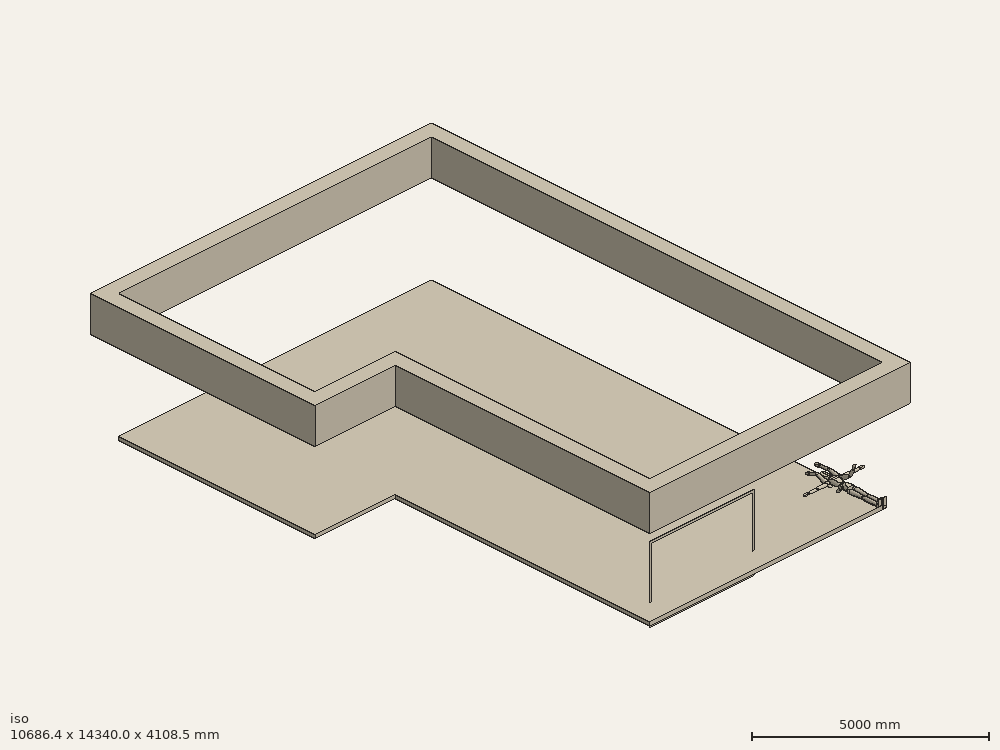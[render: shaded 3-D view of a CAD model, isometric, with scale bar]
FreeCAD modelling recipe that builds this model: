
FCSTD DOCUMENT  (FreeCAD 1.0R39109 (Git))
Label: 69
License: All rights reserved
LicenseURL: http://en.wikipedia.org/wiki/All_rights_reserved
objects: Sketcher::SketchObject×156, PartDesign::CoordinateSystem×87, PartDesign::Fillet×81, PartDesign::Groove×78, PartDesign::Revolution×75, PartDesign::Body×45, PartDesign::Pocket×27, Part::FeaturePython×6, PartDesign::Pad×6, App::Part×3, App::FeaturePython×2, Part::Part2DObjectPython×2, TechDraw::DrawSVGTemplate×1, TechDraw::DrawViewImage×1, TechDraw::DrawViewArch×1, TechDraw::DrawPage×1, App::Link×1, Assembly::JointGroup×1, Assembly::AssemblyObject×1
note: 1254 computed .brp shape members not serialized (recipe doc carries the construction recipe); baked Part::Feature solids carry a one-line shape summary decoded from their .brp
EXTERNAL_REF file=shed_shelves.FCStd obj=Assembly

FEATURE [Sketcher::SketchObject] Sketch
  ArcFitTolerance = 0
  FullyConstrained = true
  MakeInternals = false
  sketch-geometry (6):
    g0: LineSegment StartX=-9360 StartY=7620 StartZ=0 EndX=-9360 EndY=13500 EndZ=0
    g1: LineSegment StartX=-9360 StartY=13500 StartZ=0 EndX=0 EndY=13500 EndZ=0
    g2: LineSegment StartX=0 StartY=13500 StartZ=0 EndX=0 EndY=0 EndZ=0
    g3: LineSegment StartX=0 StartY=0 StartZ=0 EndX=-6960 EndY=0 EndZ=0
    g4: LineSegment StartX=-6960 StartY=0 StartZ=0 EndX=-6960 EndY=7620 EndZ=0
    g5: LineSegment StartX=-6960 StartY=7620 StartZ=0 EndX=-9360 EndY=7620 EndZ=0
  constraints (17):
    c: Vertical(g0)
    c: Horizontal(g1)
    c: Coincident(g1,g2)
    c: Vertical(g2)
    c: Coincident(g2,g3)
    c: Horizontal(g3)
    c: Coincident(g3,g4)
    c: Vertical(g4)
    c: Coincident(g4,g5)
    c: Horizontal(g5)
    c: Coincident(g5,g0)
    c: Coincident(g0,g1)
    c: DistanceX(g3,g3) = 6960
    c: Coincident(g2,g-1)
    c: DistanceY(g0,g0) = 5880
    c: DistanceX(g5,g5) = 2400
    c: DistanceY(g2,g2) = 13500
FEATURE [Part::FeaturePython] Wall001  label="Wall_Outer"  # Arch/BIM 166 (typed FeaturePython)
  Align = 1
  ArchSketchData = true
  Area = 114300000
  Base = -> Sketch
  BlockHeight = 0
  BlockLength = 0
  CountBroken = 0
  CountEntire = 0
  Face = 0
  Height = 2500
  HorizontalArea = 19908000
  IfcType = 166
  Joint = 0
  Length = 45720
  MakeBlocks = false
  MoveBase = false
  MoveWithHost = false
  Normal = (0,0,0)
  OffsetFirst = 0
  OffsetSecond = 0
  PerimeterLength = 94800
  PredefinedType = 0
  VerticalArea = 237000000
  Width = 420
FEATURE [Sketcher::SketchObject] Sketch001
  ArcFitTolerance = 0
  ExternalGeometry = -> [Sketch]
  FullyConstrained = true
  MakeInternals = false
  expr: Constraints[42] = .Constraints.a + 10 cm
  sketch-geometry (16):
    g0: LineSegment StartX=-2960 StartY=11375 StartZ=0 EndX=-2960 EndY=7865 EndZ=0
    g1: LineSegment StartX=-2960 StartY=7865 StartZ=0 EndX=0 EndY=7865 EndZ=0
    g2: LineSegment StartX=-2960 StartY=10365 StartZ=0 EndX=0 EndY=10365 EndZ=0
    g3: LineSegment StartX=-2960 StartY=0 StartZ=0 EndX=-2960 EndY=3630 EndZ=0
    g4: LineSegment StartX=-2960 StartY=3630 StartZ=0 EndX=0 EndY=3630 EndZ=0
    g5: LineSegment StartX=-4540 StartY=13500 StartZ=0 EndX=-4540 EndY=11100 EndZ=0
    g6: LineSegment StartX=-4540 StartY=11100 StartZ=0 EndX=-7060 EndY=11100 EndZ=0
    g7: LineSegment StartX=-7060 StartY=11100 StartZ=0 EndX=-7060 EndY=7620 EndZ=0
    g8: LineSegment StartX=-4540 StartY=9765 StartZ=0 EndX=-7060 EndY=9765 EndZ=0
    g9: LineSegment StartX=-2960 StartY=11375 StartZ=0 EndX=-2355 EndY=11375 EndZ=0
    g10: LineSegment StartX=-2355 StartY=11375 StartZ=0 EndX=-2355 EndY=13500 EndZ=0
    g11: LineSegment StartX=-2355 StartY=12705 StartZ=0 EndX=-3060 EndY=12705 EndZ=0
    g12: LineSegment StartX=-4540 StartY=9765 StartZ=0 EndX=-4540 EndY=9000 EndZ=0
    g13: LineSegment StartX=-2200 StartY=7865 StartZ=0 EndX=-2200 EndY=8525 EndZ=0
    g14: LineSegment StartX=-1070 StartY=7865 StartZ=0 EndX=-1070 EndY=8375 EndZ=0
    g15: LineSegment StartX=0 StartY=9145 StartZ=0 EndX=-510 EndY=9145 EndZ=0
  constraints (60):
    c: Vertical(g0)
    c: Coincident(g1,g0)
    c: PointOnObject(g1,g-4)
    c: Horizontal(g1)
    c: PointOnObject(g2,g0)
    c: Horizontal(g2)
    c: PointOnObject(g2,g-4)
    c: PointOnObject(g3,g-3)
    c: Vertical(g3)
    c: Coincident(g4,g3)
    c: PointOnObject(g4,g-4)
    c: Horizontal(g4)
    c: Vertical(g3,g0)
    c: PointOnObject(g5,g-8)
    c: Vertical(g5)
    c: Coincident(g6,g5)
    c: Horizontal(g6)
    c: Coincident(g7,g6)
    c: Vertical(g7)
    c: PointOnObject(g7,g-6)
    c: Horizontal(g8)
    c: PointOnObject(g8,g7)
    c: Vertical(g8,g5)
    c: Horizontal(g9)
    c: Coincident(g0,g9)
    c: Coincident(g9,g10)
    c: PointOnObject(g10,g-8)
    c: Vertical(g10)
    c: PointOnObject(g11,g10)
    c: Horizontal(g11)
    c: DistanceX(g3,g-4) = 2960
    c: DistanceX(g-5,g3) = 4000
    c: DistanceY(g3,g3) = 3630
    c: Coincident(g12,g8)
    c: Vertical(g12)
    c: DistanceX(g8,g8) = 2520
    c: DistanceY(g12,g12) = 765
    c: DistanceY(g8,g5) = 1335
    c: DistanceX(g12,g2) = 1580
    c: DistanceX(g-6,g7) = -100
    c: DistanceX(g9,g9) = 605  'a'
    c: DistanceY(g0,g11) = 1330
    c: DistanceX(g11,g11) = 705
    c: DistanceY(g11,g10) = 795
    c: DistanceY(g5,g5) = 2400
    c: DistanceY(g2,g0) = 1010
    c: PointOnObject(g13,g1)
    c: Vertical(g13)
    c: PointOnObject(g14,g1)
    c: Vertical(g14)
    c: PointOnObject(g15,g-4)
    c: Horizontal(g15)
    c: DistanceX(g15,g15) = 510
    c: DistanceY(g14,g14) = 510
    c: DistanceY(g13,g13) = 660
    c: DistanceX(g0,g13) = 760
    c: DistanceX(g14,g15) = 1070
    c: DistanceY(g1,g15) = 1280
    c: DistanceY(g0,g2) = 2500
    c: DistanceY(g3,g0) = 4235
FEATURE [Part::FeaturePython] Wall002  label="Wall_Inner"  # Arch/BIM 166 (typed FeaturePython)
  Align = 1
  ArchSketchData = true
  Area = 82050000
  Base = -> Sketch001
  BlockHeight = 0
  BlockLength = 0
  CountBroken = 0
  CountEntire = 0
  Face = 0
  Height = 2500
  HorizontalArea = 0
  IfcType = 166
  Joint = 0
  Length = 32820
  MakeBlocks = false
  MoveBase = false
  MoveWithHost = false
  Normal = (0,0,0)
  OffsetFirst = 0
  OffsetSecond = 0
  PerimeterLength = 0
  PredefinedType = 0
  VerticalArea = 0
  Width = 100
FEATURE [Sketcher::SketchObject] Sketch004
  ArcFitTolerance = 0
  ExternalGeometry = -> [Wall001]
  FullyConstrained = false
  MakeInternals = false
  MapMode = 5
  Placement = pos=(0,567.773,0) rot=(1,0,0;1.5708rad)
  sketch-geometry (10):
    g0: LineSegment StartX=-42527.4 StartY=2392.27 StartZ=0 EndX=-39377.4 EndY=2392.27 EndZ=0
    g1: LineSegment StartX=-39377.4 StartY=2392.27 StartZ=0 EndX=-39377.4 EndY=0 EndZ=0
    g2: LineSegment StartX=-39377.4 StartY=0 StartZ=0 EndX=-42527.4 EndY=0 EndZ=0
    g3: LineSegment StartX=-42527.4 StartY=0 StartZ=0 EndX=-42527.4 EndY=2392.27 EndZ=0
    g4: LineSegment StartX=-42457.4 StartY=2322.27 StartZ=0 EndX=-39447.4 EndY=2322.27 EndZ=0
    g5: LineSegment StartX=-39447.4 StartY=2322.27 StartZ=0 EndX=-39447.4 EndY=70 EndZ=0
    g6: LineSegment StartX=-39447.4 StartY=70 StartZ=0 EndX=-42457.4 EndY=70 EndZ=0
    g7: LineSegment StartX=-42457.4 StartY=70 StartZ=0 EndX=-42457.4 EndY=2322.27 EndZ=0
    g8: GeomPoint [constr] X=-40952.4 Y=1196.13 Z=0
    g9: GeomPoint [constr] X=-40952.4 Y=1196.13 Z=0
  constraints (22):
    c: Coincident(g0,g1)
    c: Coincident(g1,g2)
    c: Coincident(g2,g3)
    c: Coincident(g3,g0)
    c: Horizontal(g0)
    c: Horizontal(g2)
    c: Vertical(g1)
    c: Vertical(g3)
    c: Coincident(g4,g5)
    c: Coincident(g5,g6)
    c: Coincident(g6,g7)
    c: Coincident(g7,g4)
    c: Horizontal(g4)
    c: Horizontal(g6)
    c: Vertical(g5)
    c: Vertical(g7)
    c: DistanceX(g4,g0) = 70
    c: DistanceY(g4,g0) = 70
    c: Symmetric(g2,g0,g9)
    c: Symmetric(g6,g4,g8)
    c: Coincident(g8,g9)
    c: DistanceX(g2,g2) = 3150
FEATURE [Sketcher::SketchObject] Sketch002
  ArcFitTolerance = 0
  ExternalGeometry = -> [Wall001]
  FullyConstrained = false
  MakeInternals = false
  MapMode = 5
  Placement = pos=(0,567.773,0) rot=(1,0,0;1.5708rad)
  sketch-geometry (22):
    g0: LineSegment StartX=-6400 StartY=-608.511 StartZ=0 EndX=-3250 EndY=-608.511 EndZ=0
    g1: LineSegment StartX=-3250 StartY=-608.511 StartZ=0 EndX=-3250 EndY=1501.64 EndZ=0
    g2: LineSegment StartX=-3250 StartY=1501.64 StartZ=0 EndX=-6400 EndY=1501.64 EndZ=0
    g3: LineSegment StartX=-6400 StartY=1501.64 StartZ=0 EndX=-6400 EndY=-608.511 EndZ=0
    g4: LineSegment StartX=-6330 StartY=1431.64 StartZ=0 EndX=-3320 EndY=1431.64 EndZ=0
    g5: LineSegment StartX=-3320 StartY=1431.64 StartZ=0 EndX=-3320 EndY=-538.511 EndZ=0
    g6: LineSegment StartX=-3320 StartY=-538.511 StartZ=0 EndX=-6330 EndY=-538.511 EndZ=0
    g7: LineSegment StartX=-6330 StartY=-538.511 StartZ=0 EndX=-6330 EndY=1431.64 EndZ=0
    g8: GeomPoint [constr] X=-4825 Y=446.564 Z=0
    g9: GeomPoint [constr] X=-4825 Y=446.564 Z=0
    g10: LineSegment StartX=-5469.54 StartY=1431.64 StartZ=0 EndX=-5329.54 EndY=1431.64 EndZ=0
    g11: LineSegment StartX=-5329.54 StartY=1431.64 StartZ=0 EndX=-5329.54 EndY=-538.511 EndZ=0
    g12: LineSegment StartX=-5329.54 StartY=-538.511 StartZ=0 EndX=-5469.54 EndY=-538.511 EndZ=0
    g13: LineSegment StartX=-5469.54 StartY=-538.511 StartZ=0 EndX=-5469.54 EndY=1431.64 EndZ=0
    g14: LineSegment StartX=-4500.16 StartY=1431.64 StartZ=0 EndX=-4360.16 EndY=1431.64 EndZ=0
    g15: LineSegment StartX=-4360.16 StartY=1431.64 StartZ=0 EndX=-4360.16 EndY=-538.511 EndZ=0
    g16: LineSegment StartX=-4360.16 StartY=-538.511 StartZ=0 EndX=-4500.16 EndY=-538.511 EndZ=0
    g17: LineSegment StartX=-4500.16 StartY=-538.511 StartZ=0 EndX=-4500.16 EndY=1431.64 EndZ=0
    g18: LineSegment StartX=-5469.54 StartY=394.079 StartZ=0 EndX=-6330 EndY=394.079 EndZ=0
    g19: LineSegment StartX=-6330 StartY=394.079 StartZ=0 EndX=-6330 EndY=534.079 EndZ=0
    g20: LineSegment StartX=-6330 StartY=534.079 StartZ=0 EndX=-5469.54 EndY=534.079 EndZ=0
    g21: LineSegment StartX=-5469.54 StartY=534.079 StartZ=0 EndX=-5469.54 EndY=394.079 EndZ=0
  constraints (59):
    c: Coincident(g0,g1)
    c: Coincident(g1,g2)
    c: Coincident(g2,g3)
    c: Coincident(g3,g0)
    c: Horizontal(g0)
    c: Horizontal(g2)
    c: Vertical(g1)
    c: Vertical(g3)
    c: Coincident(g4,g5)
    c: Coincident(g5,g6)
    c: Coincident(g6,g7)
    c: Coincident(g7,g4)
    c: Horizontal(g4)
    c: Horizontal(g6)
    c: Vertical(g5)
    c: Vertical(g7)
    c: Symmetric(g6,g4,g8)
    c: Symmetric(g1,g0,g9)
    c: Coincident(g9,g8)
    c: DistanceX(g4,g1) = 70
    c: DistanceY(g4,g1) = 70
    c: Coincident(g10,g11)
    c: Coincident(g11,g12)
    c: Coincident(g12,g13)
    c: Coincident(g13,g10)
    c: Horizontal(g10)
    c: Horizontal(g12)
    c: Vertical(g11)
    c: Vertical(g13)
    c: PointOnObject(g10,g4)
    c: PointOnObject(g11,g6)
    c: Coincident(g14,g15)
    c: Coincident(g15,g16)
    c: Coincident(g16,g17)
    c: Coincident(g17,g14)
    c: Horizontal(g14)
    c: Horizontal(g16)
    c: Vertical(g15)
    c: Vertical(g17)
    c: PointOnObject(g14,g4)
    c: PointOnObject(g15,g6)
    c: Coincident(g18,g19)
    c: Coincident(g19,g20)
    c: Coincident(g20,g21)
    c: Coincident(g21,g18)
    c: Horizontal(g18)
    c: Horizontal(g20)
    c: Vertical(g19)
    c: Vertical(g21)
    c: PointOnObject(g18,g13)
    c: PointOnObject(g19,g7)
    c: DistanceX(g12,g11) = 140
    c: DistanceX(g16,g15) = 140
    c: DistanceY(g18,g20) = 140
    c: DistanceX(g0,g0) = 3150
    c: DistanceX(g20,g20) = 860.46
    c: DistanceY(g0,g18) = 1002.59
    c: DistanceY(g3,g3) = 2110.15
    c: DistanceX(g15,g5) = 1040.16
FEATURE [Part::FeaturePython] Window  # Arch/BIM 170 (typed FeaturePython)
  Area = 0
  Base = -> Sketch002
  Frame = 0
  Height = 0
  HoleDepth = 0
  HoleWire = 0
  HorizontalArea = 0
  IfcData = attributes={"OverallHeight": {"value": 0.0}, "OverallWidth": {"value": 0.0}}
  IfcType = 170
  LouvreSpacing = 0
  LouvreWidth = 0
  MoveBase = false
  MoveWithHost = true
  Normal = (0,1,-2e-16)
  Opening = 0
  OverallHeight = 0
  OverallWidth = 0
  PartitioningType = 0
  PerimeterLength = 0
  PredefinedType = 0
  Preset = 0
  SymbolElevation = false
  SymbolPlan = false
  VerticalArea = 0
  Width = 0
  WindowParts = Default | Frame | Wire0,Wire1,Wire2,Wire3,Wire4 | 1 | 0
  expr: OverallHeight = .Height.Value
  expr: OverallWidth = .Width.Value
FEATURE [Part::FeaturePython] Structure  # Arch/BIM 172 (typed FeaturePython)
  Base = -> Sketch
  BaseMirror = false
  BaseOffsetX = 0
  BaseOffsetY = 0
  BasePerpendicularToTool = false
  BaseRotation = 0
  ComputedLength = 100
  FaceMaker = 0
  Height = 100
  HorizontalArea = 108072000
  IfcType = 172
  Length = 0
  MoveBase = false
  MoveWithHost = false
  Nodes = (2) [(-4091.11,7247.51,0),(-4091.11,7247.51,-100)]
  NodesOffset = 0
  Normal = (0,0,0)
  PerimeterLength = 45720
  PredefinedType = 0
  ToolOffsetFirst = 0
  ToolOffsetLast = 0
  VerticalArea = 4572000
  Width = 1000
FEATURE [Part::FeaturePython] Wall  label="Wall_Roof"  # Arch/BIM 166 (typed FeaturePython)
  Align = 1
  ArchSketchData = true
  Area = 45720000
  Base = -> Sketch
  BlockHeight = 0
  BlockLength = 0
  CountBroken = 0
  CountEntire = 0
  Face = 0
  Height = 1000
  HorizontalArea = 19908000
  IfcType = 166
  Joint = 0
  Length = 45720
  MakeBlocks = false
  MoveBase = false
  MoveWithHost = false
  Normal = (0,0,0)
  OffsetFirst = 0
  OffsetSecond = 0
  PerimeterLength = 94800
  Placement = pos=(0,0,2500) rot=(0,0,1;0rad)
  PredefinedType = 0
  VerticalArea = 94800000
  Width = 420
FEATURE [TechDraw::DrawSVGTemplate] Template
  Height = 304.8
  Orientation = 1
  Template = <path>
  Width = 457.2
FEATURE [TechDraw::DrawViewImage] ActiveView
  Height = 102.4
  ImageFile = <userpath>/.cache/FreeCAD/Cache/FreeCAD_Doc_a79d04ec-db21-4fb2-806d-f2524595e8da_78bda8_607707/PageActiveViewpjV7xk.png
  LockPosition = false
  Rotation = 0
  Scale = 0.5
  ScaleType = 2
  Width = 128
  X = 369.736
  Y = 89.5228
FEATURE [Sketcher::SketchObject] Sketch005
  ArcFitTolerance = 1e-06
  ExternalGeometry = -> [Wall]
  FullyConstrained = true
  MakeInternals = false
  sketch-geometry (3):
    g0: LineSegment StartX=-8800 StartY=13920 StartZ=0 EndX=-8800 EndY=16770 EndZ=0
    g1: LineSegment StartX=-8800 StartY=16770 StartZ=0 EndX=-7510 EndY=16770 EndZ=0
    g2: LineSegment StartX=-7510 StartY=16770 StartZ=0 EndX=-7510 EndY=13920 EndZ=0
  constraints (10):
    c: Distance(g0) = 2850
    c: Vertical(g0)
    c: Distance(g1) = 1290
    c: Horizontal(g1)
    c: Coincident(g1,g0)
    c: Coincident(g2,g1)
    c: Vertical(g2)
    c: Horizontal(g2,g0)
    c: Horizontal(g0,g-3)
    c: Distance(g0,g-3) = 980
FEATURE [Part::FeaturePython] Wall003  label="Wall_Shed"  # Arch/BIM 166 (typed FeaturePython)
  Align = 1
  ArchSketchData = true
  Area = 16146900
  Base = -> Sketch005
  BlockHeight = 0
  BlockLength = 0
  CountBroken = 0
  CountEntire = 0
  Face = 0
  Height = 2310
  HorizontalArea = 1.478e+06
  IfcData = attributes={"GlobalId": {"name": "GlobalId", "type": "IfcGloballyUniqueId", "is_enum": false, "enum_values": []}, "Description": {"... (+533 chars omitted),+1 more (map truncated)
  IfcType = 166
  Joint = 0
  Length = 6990
  MakeBlocks = false
  MoveBase = false
  MoveWithHost = false
  Normal = (0,0,0)
  OffsetFirst = 0
  OffsetSecond = 0
  PerimeterLength = 15180
  PredefinedType = 0
  VerticalArea = 35065800
  Width = 200
FEATURE [App::FeaturePython] Section  # WARN: FeaturePython — macro-defined, semantics opaque (R4)
  Clip = false
  Depth = 0
  Objects = -> [Wall001,Wall002,Wall003]
  OnlySolids = true
  Placement = pos=(-4687.81,6742.19,1250) rot=(0.759144,0.1826,0.624786;0rad)
  UseMaterialColorForFill = false
FEATURE [Part::Part2DObjectPython] Shape2DView  # Draft 2D object (typed FeaturePython)
  AutoUpdate = true
  Base = -> Section
  Clip = false
  FuseArch = false
  HiddenLines = false
  InPlace = true
  OnlySolids = false
  Projection = (0.361718,-0.400925,0.841677)
  ProjectionMode = 0
  SegmentLength = 0.05
  Tessellation = false
  VisibleOnly = false
FEATURE [Part::Part2DObjectPython] Shape2DView001  # Draft 2D object (typed FeaturePython)
  AutoUpdate = true
  Base = -> Section
  Clip = false
  FuseArch = false
  HiddenLines = false
  InPlace = true
  OnlySolids = false
  Placement = pos=(0,0,3051.7) rot=(0,0,1;0rad)
  Projection = (0.361718,-0.400925,0.841677)
  ProjectionMode = 0
  SegmentLength = 0.05
  Tessellation = false
  VisibleOnly = false
FEATURE [TechDraw::DrawViewArch] ArchView  label="TopViewStue"
  AllOn = false
  Caption = TopViewStue
  CutLineWidth = 0.5
  FillSpaces = true
  FontSize = 12
  JoinArch = false
  LineSpacing = 1
  LineWidth = 0.25
  LockPosition = false
  RenderMode = 2
  Rotation = 0
  Scale = 0.01
  ScaleType = 2
  ShowFill = false
  ShowHidden = false
  Source = -> Section
  Symbol = <blob: 39801 chars omitted>
  X = 81.0502
  Y = 207.25
  expr: Caption = Label
FEATURE [TechDraw::DrawPage] Page
  KeepUpdated = true
  NextBalloonIndex = 1
  ProjectionType = 0
  Scale = 0.01
  Template = -> Template
  Views = -> [ArchView,ActiveView]
FEATURE [Sketcher::SketchObject] Sketch006
  ArcFitTolerance = 0
  FullyConstrained = true
  MakeInternals = false
  MapMode = 5
  sketch-geometry (12):
    g0: LineSegment StartX=0 StartY=0 StartZ=0 EndX=90 EndY=0 EndZ=0
    g1: LineSegment StartX=90 StartY=0 StartZ=0 EndX=90 EndY=215 EndZ=0
    g2: LineSegment StartX=90 StartY=215 StartZ=0 EndX=0 EndY=215 EndZ=0
    g3: LineSegment StartX=0 StartY=215 StartZ=0 EndX=0 EndY=0 EndZ=0
    g4: LineSegment StartX=3.5 StartY=0 StartZ=0 EndX=86.5 EndY=0 EndZ=0
    g5: LineSegment StartX=86.5 StartY=0 StartZ=0 EndX=86.5 EndY=211.5 EndZ=0
    g6: LineSegment StartX=86.5 StartY=211.5 StartZ=0 EndX=3.5 EndY=211.5 EndZ=0
    g7: LineSegment StartX=3.5 StartY=211.5 StartZ=0 EndX=3.5 EndY=0 EndZ=0
    g8: LineSegment StartX=-2 StartY=0 StartZ=0 EndX=92 EndY=0 EndZ=0
    g9: LineSegment StartX=92 StartY=0 StartZ=0 EndX=92 EndY=217 EndZ=0
    g10: LineSegment StartX=92 StartY=217 StartZ=0 EndX=-2 EndY=217 EndZ=0
    g11: LineSegment StartX=-2 StartY=217 StartZ=0 EndX=-2 EndY=0 EndZ=0
  constraints (36):
    c: Coincident(g0,g1)
    c: Coincident(g1,g2)
    c: Coincident(g2,g3)
    c: Coincident(g3,g0)
    c: Horizontal(g0)
    c: Horizontal(g2)
    c: Vertical(g1)
    c: Vertical(g3)
    c: DistanceX(g0) = 0
    c: DistanceY(g0) = 0
    c: DistanceX(g0) = 90
    c: DistanceY(g1) = 215
    c: Coincident(g4,g5)
    c: Coincident(g5,g6)
    c: Coincident(g6,g7)
    c: Coincident(g7,g4)
    c: Horizontal(g4)
    c: Horizontal(g6)
    c: Vertical(g5)
    c: Vertical(g7)
    c: DistanceY(g6,g2) = 3.5
    c: DistanceX(g6,g2) = -3.5
    c: DistanceX(g5,g1) = 3.5
    c: DistanceY(g4,g0) = 0
    c: Coincident(g8,g9)
    c: Coincident(g9,g10)
    c: Coincident(g10,g11)
    c: Coincident(g11,g8)
    c: Horizontal(g8)
    c: Horizontal(g10)
    c: Vertical(g9)
    c: Vertical(g11)
    c: DistanceX(g2,g10) = -2
    c: DistanceX(g1,g9) = 2
    c: DistanceY(g2,g10) = 2
    c: DistanceY(g8,g0) = 0
FEATURE [PartDesign::CoordinateSystem] LCS_0
  AttacherType = Attacher::AttachEngine3D
  AttachmentSupport = -> [X_Axis020]
  MapMode = 2
FEATURE [Sketcher::SketchObject] Sketch061
  ArcFitTolerance = 0
  AttachmentSupport = -> [XY_Plane021]
  FullyConstrained = true
  MakeInternals = false
  MapMode = 5
  sketch-geometry (14):
    g0: LineSegment StartX=0 StartY=0 StartZ=0 EndX=0 EndY=296.299 EndZ=0
    g1-g7: Circle [constr] x7 (B-spline internal-alignment scaffolding for g8; pole/knot coordinates omitted)
    g8: BSplineCurve PolesCount=7 KnotsCount=5 Degree=3 IsPeriodic=0
    g9-g13: GeomPoint [constr] x5 (B-spline internal-alignment scaffolding for g8; pole/knot coordinates omitted)
  constraints (12):
    c: Coincident(g0,g-1)
    c: Vertical(g0)
    c: Weight(g1) = 1
    c: Coincident(g8,g0)
    c: Equal(g1, g2-g7) x6
    c: Coincident(g8,g0)
    c: InternalAlignment(g1-g7 -> g8) x7
    c: InternalAlignment(g9-g13 -> g8) x5
    c: Horizontal(g0,g2)
    c: Horizontal(g0,g6)
    c: Block(g0)
    c: Block(g8)
FEATURE [PartDesign::Revolution] Revolution033
  Angle = 360
  Angle2 = 60
  Axis = (0,1,0)
  Base = (0,0,0)
  Profile = -> Sketch061
  ReferenceAxis = -> Sketch061 [V_Axis]
  Reversed = true
  Suppressed = false
  Type = 0
FEATURE [PartDesign::CoordinateSystem] Local_CS033  label="Head/Neck LCS"
  AttacherType = Attacher::AttachEngine3D
  AttachmentSupport = -> [Revolution033]
  MapMode = 2
FEATURE [Sketcher::SketchObject] Sketch062
  ArcFitTolerance = 0
  AttachmentSupport = -> [XY_Plane022]
  FullyConstrained = true
  MakeInternals = false
  MapMode = 5
  sketch-geometry (18):
    g0: LineSegment StartX=0 StartY=322.019 StartZ=0 EndX=0 EndY=20.3719 EndZ=0
    g1-g9: Circle [constr] x9 (B-spline internal-alignment scaffolding for g10; pole/knot coordinates omitted)
    g10: BSplineCurve PolesCount=9 KnotsCount=7 Degree=3 IsPeriodic=0
    g11-g17: GeomPoint [constr] x7 (B-spline internal-alignment scaffolding for g10; pole/knot coordinates omitted)
  constraints (12):
    c: Vertical(g0)
    c: PointOnObject(g0,g-2)
    c: Weight(g1) = 1
    c: Coincident(g10,g0)
    c: Equal(g1, g2-g9) x8
    c: Coincident(g10,g0)
    c: InternalAlignment(g1-g9 -> g10) x9
    c: InternalAlignment(g11-g17 -> g10) x7
    c: Horizontal(g0,g2)
    c: Horizontal(g0,g8)
    c: Block(g0)
    c: Block(g10)
FEATURE [PartDesign::Revolution] Revolution034  label="Base shape"
  Angle = 360
  Angle2 = 60
  Axis = (0,1,0)
  Base = (0,0,0)
  Profile = -> Sketch062
  ReferenceAxis = -> Sketch062 [V_Axis]
  Reversed = true
  Suppressed = false
  Type = 0
FEATURE [PartDesign::CoordinateSystem] Local_CS028  label="Chest/Neck LCS"
  AttacherType = Attacher::AttachEngine3D
  AttachmentOffset = pos=(354,0,0) rot=(0,0,1;0rad)
  AttachmentSupport = -> [Revolution034]
  MapMode = 4
  Placement = pos=(0,354,0) rot=(0.57735,0.57735,0.57735;2.0944rad)
FEATURE [PartDesign::CoordinateSystem] Local_CS029  label="Chest/Waist LCS"
  AttacherType = Attacher::AttachEngine3D
  AttachmentSupport = -> [Revolution034]
  MapMode = 2
FEATURE [PartDesign::CoordinateSystem] Local_CS030  label="Chest/Left shoulder LCS"
  AttacherType = Attacher::AttachEngine3D
  AttachmentOffset = pos=(184,257,0) rot=(0,0,1;0rad)
  AttachmentSupport = -> [Revolution034]
  MapMode = 2
  Placement = pos=(184,257,0) rot=(0,0,1;0rad)
FEATURE [PartDesign::CoordinateSystem] Local_CS031  label="Chest/Right shoulder LCS"
  AttacherType = Attacher::AttachEngine3D
  AttachmentOffset = pos=(-184,257,0) rot=(0,0,1;0rad)
  AttachmentSupport = -> [Revolution034]
  MapMode = 2
  Placement = pos=(-184,257,0) rot=(0,0,1;0rad)
FEATURE [Sketcher::SketchObject] Sketch063
  ArcFitTolerance = 0
  AttachmentSupport = -> [XY_Plane021]
  FullyConstrained = true
  MakeInternals = false
  MapMode = 5
  sketch-geometry (2):
    g0: LineSegment StartX=-1.01e-14 StartY=55 StartZ=0 EndX=-1.01e-14 EndY=-55 EndZ=0
    g1: ArcOfCircle CenterX=0 CenterY=0 CenterZ=0 NormalX=0 NormalY=0 NormalZ=1 AngleXU=0 Radius=55 StartAngle=4.71239 EndAngle=7.85398
  constraints (6):
    c: Vertical(g0)
    c: Coincident(g1,g-1)
    c: Coincident(g1,g0)
    c: Coincident(g1,g0)
    c: PointOnObject(g0,g-2)
    c: Radius(g1) = 55
FEATURE [PartDesign::Groove] Groove026
  Angle = 360
  Angle2 = 60
  Axis = (0,1,0)
  Base = (0,0,0)
  BaseFeature = -> Revolution033
  Profile = -> Sketch063
  ReferenceAxis = -> Sketch063 [V_Axis]
  Suppressed = false
  Type = 0
FEATURE [Sketcher::SketchObject] Sketch064
  ArcFitTolerance = 0
  AttachmentSupport = -> [XZ_Plane021]
  FullyConstrained = true
  MakeInternals = false
  MapMode = 5
  Placement = pos=(0,0,0) rot=(1,0,0;1.5708rad)
  sketch-geometry (5):
    g0: LineSegment StartX=-125 StartY=125 StartZ=0 EndX=125 EndY=125 EndZ=0
    g1: LineSegment StartX=125 StartY=125 StartZ=0 EndX=125 EndY=50 EndZ=0
    g2: LineSegment StartX=125 StartY=50 StartZ=0 EndX=0 EndY=75 EndZ=0
    g3: LineSegment StartX=0 StartY=75 StartZ=0 EndX=-125 EndY=50 EndZ=0
    g4: LineSegment StartX=-125 StartY=50 StartZ=0 EndX=-125 EndY=125 EndZ=0
  constraints (15):
    c: Horizontal(g0)
    c: Coincident(g0,g1)
    c: Vertical(g1)
    c: Coincident(g1,g2)
    c: Coincident(g2,g3)
    c: Coincident(g3,g4)
    c: Coincident(g4,g0)
    c: Vertical(g4)
    c: Horizontal(g3,g1)
    c: PointOnObject(g2,g-2)
    c: DistanceX(g0,g0) = 250
    c: DistanceX(g0,g-1) = 125
    c: DistanceY(g4,g4) = 75
    c: DistanceY(g-1,g2) = 75
    c: DistanceY(g-1,g0) = 125
FEATURE [PartDesign::Pocket] Pocket009
  BaseFeature = -> Groove026
  Direction = (0,1,0.05)
  Length = 300
  Length2 = 5
  Profile = -> Sketch064
  ReferenceAxis = -> Sketch064 [N_Axis]
  Suppressed = false
  Type = 0
  UseCustomVector = true
FEATURE [PartDesign::Fillet] Fillet027
  Base = -> Pocket009 [Edge3]
  BaseFeature = -> Pocket009
  Radius = 3
  SupportTransform = false
  Suppressed = false
  UseAllEdges = false
FEATURE [PartDesign::Body] Body019  label="Head"
  AllowCompound = false
  Group = -> [Sketch061,Revolution033,Sketch063,Groove026,Sketch064,Pocket009,Fillet027,Local_CS033]
  Origin = -> Origin021
  Placement = pos=(0,1552,0) rot=(0,0,1;0rad)
  Tip = -> Fillet027
FEATURE [Sketcher::SketchObject] Sketch065
  ArcFitTolerance = 0
  AttachmentSupport = -> [YZ_Plane022]
  FullyConstrained = true
  MakeInternals = false
  MapMode = 5
  Placement = pos=(0,0,0) rot=(0.57735,0.57735,0.57735;2.0944rad)
  sketch-geometry (6):
    g0: LineSegment StartX=0 StartY=76.0576 StartZ=0 EndX=164.705 EndY=107.04 EndZ=0
    g1: LineSegment StartX=230.198 StartY=103.732 StartZ=0 EndX=327.121 EndY=75.1407 EndZ=0
    g2: LineSegment StartX=327.121 StartY=75.1407 StartZ=0 EndX=327.121 EndY=181.805 EndZ=0
    g3: LineSegment StartX=327.121 StartY=181.805 StartZ=0 EndX=0 EndY=181.805 EndZ=0
    g4: LineSegment StartX=0 StartY=181.805 StartZ=0 EndX=0 EndY=76.0576 EndZ=0
    g5: ArcOfCircle CenterX=190.587 CenterY=-30.5467 CenterZ=0 NormalX=0 NormalY=0 NormalZ=1 AngleXU=0 Radius=140 StartAngle=1.28394 EndAngle=1.75673
  constraints (14):
    c: Coincident(g1,g2)
    c: Vertical(g2)
    c: Coincident(g2,g3)
    c: Horizontal(g3)
    c: Coincident(g3,g4)
    c: Coincident(g4,g0)
    c: Vertical(g4)
    c: PointOnObject(g3,g-2)
    c: Tangent(g1,g5) = 1.5708
    c: Tangent(g0,g5) = 1.5708
    c: Radius(g5) = 140
    c: Block(g0)
    c: Block(g1)
    c: Block(g3)
FEATURE [PartDesign::Pocket] Pocket010  label="Front cut"
  BaseFeature = -> Revolution034
  Direction = (-1,0,0)
  Length = 5
  Length2 = 5
  Midplane = true
  Profile = -> Sketch065
  ReferenceAxis = -> Sketch065 [N_Axis]
  Suppressed = false
  Type = 1
FEATURE [Sketcher::SketchObject] Sketch066
  ArcFitTolerance = 0
  AttachmentSupport = -> [YZ_Plane022]
  FullyConstrained = true
  MakeInternals = false
  MapMode = 5
  Placement = pos=(0,0,0) rot=(0.57735,0.57735,0.57735;2.0944rad)
  sketch-geometry (8):
    g0: LineSegment StartX=0 StartY=-87.996 StartZ=0 EndX=81.1566 EndY=-77.888 EndZ=0
    g1: LineSegment StartX=139.259 StartY=-78.9913 StartZ=0 EndX=245.223 EndY=-96.2967 EndZ=0
    g2: LineSegment StartX=281.434 StartY=-93.8397 StartZ=0 EndX=341.01 EndY=-75.582 EndZ=0
    g3: LineSegment StartX=341.01 StartY=-75.582 StartZ=0 EndX=341.01 EndY=-197.004 EndZ=0
    g4: LineSegment StartX=341.01 StartY=-197.004 StartZ=0 EndX=0 EndY=-197.004 EndZ=0
    g5: LineSegment StartX=0 StartY=-197.004 StartZ=0 EndX=0 EndY=-87.996 EndZ=0
    g6: ArcOfCircle CenterX=106.373 CenterY=-280.353 CenterZ=0 NormalX=0 NormalY=0 NormalZ=1 AngleXU=0 Radius=204.029 StartAngle=1.40891 EndAngle=1.69471
    g7: ArcOfCircle CenterX=258.073 CenterY=-17.6116 CenterZ=0 NormalX=0 NormalY=0 NormalZ=1 AngleXU=0 Radius=79.7275 StartAngle=4.5505 EndAngle=5.00977
  constraints (16):
    c: Coincident(g2,g3)
    c: Coincident(g3,g4)
    c: Horizontal(g4)
    c: Coincident(g4,g5)
    c: Coincident(g5,g0)
    c: Vertical(g5)
    c: Vertical(g3)
    c: PointOnObject(g4,g-2)
    c: Tangent(g1,g6) = 1.5708
    c: Tangent(g0,g6) = 1.5708
    c: Tangent(g1,g7) = -1.5708
    c: Tangent(g2,g7) = -1.5708
    c: Block(g0)
    c: Block(g2)
    c: Block(g1)
    c: Block(g4)
FEATURE [PartDesign::Pocket] Pocket011  label="Back cut"
  BaseFeature = -> Pocket010
  Direction = (-1,0,0)
  Length = 5
  Length2 = 5
  Midplane = true
  Profile = -> Sketch066
  ReferenceAxis = -> Sketch066 [N_Axis]
  Suppressed = false
  Type = 1
FEATURE [Sketcher::SketchObject] Sketch067
  ArcFitTolerance = 0
  AttachmentSupport = -> [XY_Plane022]
  FullyConstrained = true
  MakeInternals = false
  MapMode = 5
  sketch-geometry (2):
    g0: LineSegment StartX=0 StartY=409 StartZ=0 EndX=0 EndY=299 EndZ=0
    g1: ArcOfCircle CenterX=0 CenterY=354 CenterZ=0 NormalX=0 NormalY=0 NormalZ=1 AngleXU=0 Radius=55 StartAngle=4.71239 EndAngle=7.85398
  constraints (7):
    c: Vertical(g0)
    c: PointOnObject(g1,g0)
    c: Coincident(g1,g0)
    c: PointOnObject(g1,g-2)
    c: Coincident(g1,g0)
    c: Radius(g1) = 55
    c: DistanceY(g-1,g1) = 354
FEATURE [PartDesign::Groove] Groove027  label="Neck cut"
  Angle = 360
  Angle2 = 60
  Axis = (0,1,0)
  Base = (0,0,0)
  BaseFeature = -> Pocket011
  Profile = -> Sketch067
  ReferenceAxis = -> Sketch067 [V_Axis]
  Suppressed = false
  Type = 0
FEATURE [PartDesign::Fillet] Fillet028  label="Neck fillet"
  Base = -> Groove027 [Edge1]
  BaseFeature = -> Groove027
  Radius = 6
  SupportTransform = false
  Suppressed = false
  UseAllEdges = false
FEATURE [Sketcher::SketchObject] Sketch068
  ArcFitTolerance = 0
  AttachmentSupport = -> [XY_Plane022]
  FullyConstrained = true
  MakeInternals = false
  MapMode = 5
  sketch-geometry (2):
    g0: LineSegment StartX=-1.38e-14 StartY=75 StartZ=0 EndX=-1.38e-14 EndY=-75 EndZ=0
    g1: ArcOfCircle CenterX=0 CenterY=0 CenterZ=0 NormalX=0 NormalY=0 NormalZ=1 AngleXU=0 Radius=75 StartAngle=4.71239 EndAngle=7.85398
  constraints (6):
    c: Vertical(g0)
    c: Coincident(g1,g-1)
    c: Coincident(g1,g0)
    c: Coincident(g1,g0)
    c: PointOnObject(g0,g-2)
    c: Radius(g1) = 75
FEATURE [PartDesign::Groove] Groove028  label="Waist cut"
  Angle = 360
  Angle2 = 60
  Axis = (0,1,0)
  Base = (0,0,0)
  BaseFeature = -> Fillet028
  Profile = -> Sketch068
  ReferenceAxis = -> Sketch068 [V_Axis]
  Suppressed = false
  Type = 0
FEATURE [PartDesign::Fillet] Fillet029  label="Waist fillet"
  Base = -> Groove028 [Edge3]
  BaseFeature = -> Groove028
  Radius = 5
  SupportTransform = false
  Suppressed = false
  UseAllEdges = false
FEATURE [Sketcher::SketchObject] Sketch069
  ArcFitTolerance = 0
  AttachmentSupport = -> [XY_Plane022]
  FullyConstrained = true
  MakeInternals = false
  MapMode = 5
  sketch-geometry (4):
    g0: LineSegment StartX=124 StartY=257 StartZ=0 EndX=244 EndY=257 EndZ=0
    g1: ArcOfCircle CenterX=184 CenterY=257 CenterZ=0 NormalX=0 NormalY=0 NormalZ=1 AngleXU=0 Radius=60 StartAngle=0 EndAngle=3.14159
    g2: LineSegment StartX=-244 StartY=257 StartZ=0 EndX=-124 EndY=257 EndZ=0
    g3: ArcOfCircle CenterX=-184 CenterY=257 CenterZ=0 NormalX=0 NormalY=0 NormalZ=1 AngleXU=0 Radius=60 StartAngle=4e-16 EndAngle=3.14159
  constraints (14):
    c: Horizontal(g0)
    c: PointOnObject(g1,g0)
    c: Coincident(g1,g0)
    c: Coincident(g1,g0)
    c: DistanceY(g-1,g1) = 257
    c: Radius(g1) = 60
    c: DistanceX(g-1,g1) = 184
    c: Horizontal(g2)
    c: PointOnObject(g3,g2)
    c: Coincident(g3,g2)
    c: Coincident(g3,g2)
    c: Horizontal(g2,g0)
    c: Radius(g3) = 60
    c: DistanceX(g3,g-1) = 184
FEATURE [PartDesign::Groove] Groove029  label="Shoulders cut"
  Angle = 360
  Angle2 = 60
  Axis = (1,0,0)
  Base = (124,257,0)
  BaseFeature = -> Fillet029
  Profile = -> Sketch069
  ReferenceAxis = -> Sketch069 [Edge1]
  Suppressed = false
  Type = 0
FEATURE [PartDesign::Fillet] Fillet030  label="Shoulders fillet"
  Base = -> Groove029 [Edge6,Edge3,Edge12,Edge13]
  BaseFeature = -> Groove029
  Radius = 6
  SupportTransform = false
  Suppressed = false
  UseAllEdges = false
FEATURE [PartDesign::Revolution] Revolution035  label="Neck add"
  Angle = 360
  Angle2 = 60
  Axis = (0,1,0)
  Base = (0,0,0)
  BaseFeature = -> Fillet030
  Profile = -> Sketch067
  ReferenceAxis = -> Sketch067 [V_Axis]
  Reversed = true
  Suppressed = false
  Type = 0
FEATURE [PartDesign::Revolution] Revolution036  label="waist add"
  Angle = 360
  Angle2 = 60
  Axis = (0,1,0)
  Base = (0,0,0)
  BaseFeature = -> Revolution035
  Profile = -> Sketch068
  ReferenceAxis = -> Sketch068 [V_Axis]
  Reversed = true
  Suppressed = false
  Type = 0
FEATURE [PartDesign::Revolution] Revolution037  label="Shoulders"
  Angle = 360
  Angle2 = 60
  Axis = (1,0,0)
  Base = (-244,257,0)
  BaseFeature = -> Revolution036
  Profile = -> Sketch069
  ReferenceAxis = -> Sketch069 [Edge3]
  Suppressed = false
  Type = 0
FEATURE [PartDesign::Body] Body020  label="Chest"
  AllowCompound = false
  Group = -> [Sketch062,Revolution034,Sketch065,Pocket010,Sketch066,Pocket011,Sketch067,Groove027,Fillet028,Sketch068,Groove028,Fillet029,Sketch069,Groove029,Fillet030,Revolution035,Revolution036,Revolution037,Local_CS028,Local_CS029,Local_CS030,Local_CS031]
  Origin = -> Origin022
  Placement = pos=(0,1198,0) rot=(0,0,1;0rad)
  Tip = -> Revolution037
FEATURE [Sketcher::SketchObject] Sketch070
  ArcFitTolerance = 0
  AttachmentSupport = -> [XY_Plane023]
  FullyConstrained = true
  MakeInternals = false
  MapMode = 5
  sketch-geometry (21):
    g0: LineSegment StartX=0 StartY=-29.4305 StartZ=0 EndX=0 EndY=-256.068 EndZ=0
    g1-g7: Circle [constr] x7 (B-spline internal-alignment scaffolding for g8; pole/knot coordinates omitted)
    g8: BSplineCurve PolesCount=7 KnotsCount=5 Degree=3 IsPeriodic=0
    g9-g13: GeomPoint [constr] x5 (B-spline internal-alignment scaffolding for g8; pole/knot coordinates omitted)
    g14-g17: Circle [constr] x4 (B-spline internal-alignment scaffolding for g18; pole/knot coordinates omitted)
    g18: BSplineCurve PolesCount=4 KnotsCount=2 Degree=3 IsPeriodic=0
    g19: GeomPoint [constr] X=118.087 Y=-247.149 Z=0
    g20: GeomPoint [constr] X=0 Y=-256.068 Z=0
  constraints (21):
    c: PointOnObject(g0,g-2)
    c: Vertical(g0)
    c: Weight(g1) = 1
    c: Coincident(g8,g0)
    c: Equal(g1, g2-g7) x6
    c: InternalAlignment(g1-g7 -> g8) x7
    c: InternalAlignment(g9-g13 -> g8) x5
    c: Weight(g14) = 1
    c: Coincident(g18,g8)
    c: Equal(g14,g15)
    c: Equal(g14,g16)
    c: Equal(g14,g17)
    c: Coincident(g18,g0)
    c: InternalAlignment(g14-g17 -> g18) x4
    c: InternalAlignment(g19,g18)
    c: InternalAlignment(g20,g18)
    c: Horizontal(g16,g0)
    c: Horizontal(g0,g2)
    c: Block(g0)
    c: Block(g8)
    c: Block(g18)
FEATURE [PartDesign::Revolution] Revolution038  label="Main body of hip"
  Angle = 360
  Angle2 = 60
  Axis = (0,1,0)
  Base = (0,0,0)
  Profile = -> Sketch070
  ReferenceAxis = -> Sketch070 [V_Axis]
  Reversed = true
  Suppressed = false
  Type = 0
FEATURE [PartDesign::CoordinateSystem] Local_CS032  label="Hip/Waist LCS"
  AttacherType = Attacher::AttachEngine3D
  AttachmentSupport = -> [Revolution038]
  MapMode = 2
FEATURE [PartDesign::CoordinateSystem] Local_CS034  label="Hip/Leg joint left"
  AttacherType = Attacher::AttachEngine3D
  AttachmentOffset = pos=(75,-298,0) rot=(0,0,1;0rad)
  AttachmentSupport = -> [Revolution038]
  MapMode = 2
  Placement = pos=(75,-298,0) rot=(0,0,1;0rad)
FEATURE [PartDesign::CoordinateSystem] Local_CS035  label="Hip/Leg joint right"
  AttacherType = Attacher::AttachEngine3D
  AttachmentOffset = pos=(-75,-298,0) rot=(0,0,1;0rad)
  AttachmentSupport = -> [Revolution038]
  MapMode = 2
  Placement = pos=(-75,-298,0) rot=(0,0,1;0rad)
FEATURE [Sketcher::SketchObject] Sketch071
  ArcFitTolerance = 0
  AttachmentSupport = -> [XY_Plane023]
  FullyConstrained = true
  MakeInternals = false
  MapMode = 5
  sketch-geometry (2):
    g0: LineSegment StartX=-1.38e-14 StartY=75 StartZ=0 EndX=-1.38e-14 EndY=-75 EndZ=0
    g1: ArcOfCircle CenterX=0 CenterY=0 CenterZ=0 NormalX=0 NormalY=0 NormalZ=1 AngleXU=0 Radius=75 StartAngle=4.71239 EndAngle=7.85398
  constraints (6):
    c: Vertical(g0)
    c: PointOnObject(g1,g0)
    c: Coincident(g1,g0)
    c: Coincident(g1,g0)
    c: Coincident(g1,g-1)
    c: Radius(g1) = 75
FEATURE [PartDesign::Groove] Groove030  label="Waist cut of hip"
  Angle = 360
  Angle2 = 60
  Axis = (0,1,0)
  Base = (0,0,0)
  BaseFeature = -> Revolution038
  Profile = -> Sketch071
  ReferenceAxis = -> Sketch071 [V_Axis]
  Suppressed = false
  Type = 0
FEATURE [PartDesign::Fillet] Fillet031  label="waist"
  Base = -> Groove030 [Edge4]
  BaseFeature = -> Groove030
  Radius = 6
  SupportTransform = false
  Suppressed = false
  UseAllEdges = false
FEATURE [Sketcher::SketchObject] Sketch072
  ArcFitTolerance = 0
  AttachmentSupport = -> [XY_Plane023]
  FullyConstrained = true
  MakeInternals = false
  MapMode = 5
  sketch-geometry (4):
    g0: LineSegment StartX=15 StartY=-298 StartZ=0 EndX=135 EndY=-298 EndZ=0
    g1: ArcOfCircle CenterX=75 CenterY=-298 CenterZ=0 NormalX=0 NormalY=0 NormalZ=1 AngleXU=0 Radius=60 StartAngle=0 EndAngle=3.14159
    g2: LineSegment StartX=-135 StartY=-298 StartZ=0 EndX=-15 EndY=-298 EndZ=0
    g3: ArcOfCircle CenterX=-75 CenterY=-298 CenterZ=0 NormalX=0 NormalY=0 NormalZ=1 AngleXU=0 Radius=60 StartAngle=3e-16 EndAngle=3.14159
  constraints (14):
    c: PointOnObject(g1,g0)
    c: Coincident(g1,g0)
    c: Coincident(g1,g0)
    c: Horizontal(g0)
    c: DistanceX(g-1,g1) = 75
    c: DistanceY(g1,g-1) = 298
    c: Radius(g1) = 60
    c: Horizontal(g2)
    c: PointOnObject(g3,g2)
    c: Coincident(g3,g2)
    c: Coincident(g3,g2)
    c: Horizontal(g2,g0)
    c: Equal(g3,g1)
    c: DistanceX(g3,g-1) = 75
FEATURE [PartDesign::Groove] Groove031  label="Hip joints cuts"
  Angle = 360
  Angle2 = 60
  Axis = (1,0,0)
  Base = (15,-298,0)
  BaseFeature = -> Fillet031
  Profile = -> Sketch072
  ReferenceAxis = -> Sketch072 [Edge1]
  Suppressed = false
  Type = 0
FEATURE [PartDesign::Revolution] Revolution039  label="Hip joints"
  Angle = 360
  Angle2 = 60
  Axis = (1,0,0)
  Base = (15,-298,0)
  BaseFeature = -> Groove031
  Profile = -> Sketch072
  ReferenceAxis = -> Sketch072 [Edge1]
  Reversed = true
  Suppressed = false
  Type = 0
FEATURE [Sketcher::SketchObject] Sketch073
  ArcFitTolerance = 0
  AttachmentSupport = -> [YZ_Plane023]
  FullyConstrained = true
  MakeInternals = false
  MapMode = 5
  Placement = pos=(0,0,0) rot=(0.57735,0.57735,0.57735;2.0944rad)
  sketch-geometry (4):
    g0: LineSegment StartX=-309.733 StartY=84.7574 StartZ=0 EndX=-36.256 EndY=111.745 EndZ=0
    g1: LineSegment StartX=-36.256 StartY=111.745 StartZ=0 EndX=-36.256 EndY=192.709 EndZ=0
    g2: LineSegment StartX=-36.256 StartY=192.709 StartZ=0 EndX=-309.733 EndY=192.709 EndZ=0
    g3: LineSegment StartX=-309.733 StartY=192.709 StartZ=0 EndX=-309.733 EndY=84.7574 EndZ=0
  constraints (9):
    c: Coincident(g0,g1)
    c: Coincident(g1,g2)
    c: Horizontal(g2)
    c: Coincident(g2,g3)
    c: Coincident(g3,g0)
    c: Vertical(g3)
    c: Vertical(g1)
    c: Block(g3)
    c: Block(g0)
FEATURE [PartDesign::Pocket] Pocket012  label="front cut"
  BaseFeature = -> Revolution039
  Direction = (-1,0,0)
  Length = 5
  Length2 = 5
  Midplane = true
  Profile = -> Sketch073
  ReferenceAxis = -> Sketch073 [N_Axis]
  Suppressed = false
  Type = 1
FEATURE [Sketcher::SketchObject] Sketch074
  ArcFitTolerance = 0
  AttachmentSupport = -> [YZ_Plane023]
  FullyConstrained = true
  MakeInternals = false
  MapMode = 5
  Placement = pos=(0,0,0) rot=(0.57735,0.57735,0.57735;2.0944rad)
  sketch-geometry (4):
    g0: LineSegment StartX=-276.336 StartY=-71.4724 StartZ=0 EndX=-109.323 EndY=-126.411 EndZ=0
    g1: LineSegment StartX=-109.323 StartY=-126.411 StartZ=0 EndX=-109.323 EndY=-220.905 EndZ=0
    g2: LineSegment StartX=-109.323 StartY=-220.905 StartZ=0 EndX=-276.336 EndY=-220.905 EndZ=0
    g3: LineSegment StartX=-276.336 StartY=-220.905 StartZ=0 EndX=-276.336 EndY=-71.4724 EndZ=0
  constraints (9):
    c: Coincident(g0,g1)
    c: Coincident(g1,g2)
    c: Horizontal(g2)
    c: Coincident(g2,g3)
    c: Coincident(g3,g0)
    c: Vertical(g3)
    c: Vertical(g1)
    c: Block(g0)
    c: Block(g2)
FEATURE [PartDesign::Pocket] Pocket013  label="rear cut"
  BaseFeature = -> Pocket012
  Direction = (-1,0,0)
  Length = 5
  Length2 = 5
  Midplane = true
  Profile = -> Sketch074
  ReferenceAxis = -> Sketch074 [N_Axis]
  Suppressed = false
  Type = 1
FEATURE [PartDesign::Body] Body021  label="Hip"
  AllowCompound = false
  Group = -> [Sketch070,Revolution038,Sketch071,Groove030,Fillet031,Sketch072,Groove031,Revolution039,Sketch073,Pocket012,Sketch074,Pocket013,Local_CS032,Local_CS034,Local_CS035]
  Origin = -> Origin023
  Placement = pos=(0,1198,0) rot=(0,0,1;0rad)
  Tip = -> Pocket013
FEATURE [Sketcher::SketchObject] Sketch075
  ArcFitTolerance = 0
  AttachmentSupport = -> [XY_Plane024]
  FullyConstrained = true
  MakeInternals = false
  MapMode = 5
  sketch-geometry (12):
    g0: LineSegment StartX=15.9442 StartY=0 StartZ=0 EndX=306.848 EndY=0 EndZ=0
    g1-g6: Circle [constr] x6 (B-spline internal-alignment scaffolding for g7; pole/knot coordinates omitted)
    g7: BSplineCurve PolesCount=6 KnotsCount=4 Degree=3 IsPeriodic=0
    g8-g11: GeomPoint [constr] x4 (B-spline internal-alignment scaffolding for g7; pole/knot coordinates omitted)
  constraints (9):
    c: PointOnObject(g0,g-1)
    c: Horizontal(g0)
    c: Weight(g1) = 1
    c: Coincident(g7,g0)
    c: Equal(g1, g2-g6) x5
    c: Coincident(g7,g0)
    c: InternalAlignment(g1-g6 -> g7) x6
    c: InternalAlignment(g8-g11 -> g7) x4
    c: Block(g7)
FEATURE [PartDesign::Revolution] Revolution040  label="L Upper limb"
  Angle = 360
  Angle2 = 60
  Axis = (1,0,0)
  Base = (0,0,0)
  Profile = -> Sketch075
  ReferenceAxis = -> Sketch075 [H_Axis]
  Suppressed = false
  Type = 0
FEATURE [PartDesign::CoordinateSystem] Local_CS036  label="Left upper limb/Shoulder LCS"
  AttacherType = Attacher::AttachEngine3D
  AttachmentSupport = -> [Revolution040]
  MapMode = 2
FEATURE [PartDesign::CoordinateSystem] Local_CS037  label="Left upper limb/Elbow LCS"
  AttacherType = Attacher::AttachEngine3D
  AttachmentOffset = pos=(320,0,0) rot=(0,0,1;0rad)
  AttachmentSupport = -> [Revolution040]
  MapMode = 2
  Placement = pos=(320,0,0) rot=(0,0,1;0rad)
FEATURE [Sketcher::SketchObject] Sketch076
  ArcFitTolerance = 0
  AttachmentSupport = -> [XY_Plane024]
  FullyConstrained = true
  MakeInternals = false
  MapMode = 5
  sketch-geometry (2):
    g0: LineSegment StartX=-60 StartY=0 StartZ=0 EndX=60 EndY=0 EndZ=0
    g1: ArcOfCircle CenterX=0 CenterY=0 CenterZ=0 NormalX=0 NormalY=0 NormalZ=1 AngleXU=0 Radius=60 StartAngle=0 EndAngle=3.14159
  constraints (6):
    c: Horizontal(g0)
    c: PointOnObject(g1,g0)
    c: Coincident(g1,g0)
    c: Coincident(g1,g0)
    c: Coincident(g1,g-1)
    c: Radius(g1) = 60
FEATURE [PartDesign::Groove] Groove032  label="L Sloulder cut"
  Angle = 360
  Angle2 = 60
  Axis = (1,0,0)
  Base = (0,0,0)
  BaseFeature = -> Revolution040
  Profile = -> Sketch076
  ReferenceAxis = -> Sketch076 [H_Axis]
  Reversed = true
  Suppressed = false
  Type = 0
FEATURE [PartDesign::Fillet] Fillet032  label="L Shoulder fillet"
  Base = -> Groove032 [Edge2]
  BaseFeature = -> Groove032
  Radius = 6
  SupportTransform = false
  Suppressed = false
  UseAllEdges = false
FEATURE [Sketcher::SketchObject] Sketch077
  ArcFitTolerance = 0
  AttachmentSupport = -> [XY_Plane024]
  FullyConstrained = true
  MakeInternals = false
  MapMode = 5
  sketch-geometry (2):
    g0: LineSegment StartX=285 StartY=4.3e-15 StartZ=0 EndX=355 EndY=4.3e-15 EndZ=0
    g1: ArcOfCircle CenterX=320 CenterY=0 CenterZ=0 NormalX=0 NormalY=0 NormalZ=1 AngleXU=0 Radius=35 StartAngle=0 EndAngle=3.14159
  constraints (7):
    c: Horizontal(g0)
    c: PointOnObject(g1,g0)
    c: Coincident(g1,g0)
    c: Coincident(g1,g0)
    c: Horizontal(g1,g-1)
    c: DistanceX(g-1,g1) = 320
    c: Radius(g1) = 35
FEATURE [PartDesign::Groove] Groove033  label="L Elbow cut"
  Angle = 360
  Angle2 = 60
  Axis = (1,0,0)
  Base = (0,0,0)
  BaseFeature = -> Fillet032
  Profile = -> Sketch077
  ReferenceAxis = -> Sketch077 [H_Axis]
  Reversed = true
  Suppressed = false
  Type = 0
FEATURE [PartDesign::Fillet] Fillet033  label="L Elbow fillet"
  Base = -> Groove033 [Edge1]
  BaseFeature = -> Groove033
  Radius = 3
  SupportTransform = false
  Suppressed = false
  UseAllEdges = false
FEATURE [PartDesign::Revolution] Revolution041  label="L Elbow"
  Angle = 360
  Angle2 = 60
  Axis = (1,0,0)
  Base = (0,0,0)
  BaseFeature = -> Fillet033
  Profile = -> Sketch077
  ReferenceAxis = -> Sketch077 [H_Axis]
  Suppressed = false
  Type = 0
FEATURE [PartDesign::Body] Body022  label="Left Upper limb"
  AllowCompound = false
  Group = -> [Sketch075,Revolution040,Sketch076,Groove032,Fillet032,Sketch077,Groove033,Fillet033,Revolution041,Local_CS036,Local_CS037]
  Origin = -> Origin024
  Placement = pos=(184,1455,0) rot=(0,0,1;0rad)
  Tip = -> Revolution041
FEATURE [Sketcher::SketchObject] Sketch078
  ArcFitTolerance = 0
  AttachmentSupport = -> [XY_Plane025]
  FullyConstrained = true
  MakeInternals = false
  MapMode = 5
  sketch-geometry (12):
    g0: LineSegment StartX=5.14795 StartY=0 StartZ=0 EndX=267.265 EndY=0 EndZ=0
    g1-g6: Circle [constr] x6 (B-spline internal-alignment scaffolding for g7; pole/knot coordinates omitted)
    g7: BSplineCurve PolesCount=6 KnotsCount=4 Degree=3 IsPeriodic=0
    g8-g11: GeomPoint [constr] x4 (B-spline internal-alignment scaffolding for g7; pole/knot coordinates omitted)
  constraints (9):
    c: PointOnObject(g0,g-1)
    c: Horizontal(g0)
    c: Weight(g1) = 1
    c: Coincident(g7,g0)
    c: Equal(g1, g2-g6) x5
    c: Coincident(g7,g0)
    c: InternalAlignment(g1-g6 -> g7) x6
    c: InternalAlignment(g8-g11 -> g7) x4
    c: Block(g7)
FEATURE [PartDesign::Revolution] Revolution042  label="Left Forearm main body"
  Angle = 360
  Angle2 = 60
  Axis = (1,0,0)
  Base = (0,0,0)
  Profile = -> Sketch078
  ReferenceAxis = -> Sketch078 [H_Axis]
  Suppressed = false
  Type = 0
FEATURE [PartDesign::CoordinateSystem] Local_CS038  label="Left Forearm/Elbow"
  AttacherType = Attacher::AttachEngine3D
  AttachmentSupport = -> [Revolution042]
  MapMode = 2
FEATURE [PartDesign::CoordinateSystem] Local_CS039  label="Left Forearm/Wrist"
  AttacherType = Attacher::AttachEngine3D
  AttachmentOffset = pos=(253,0,0) rot=(0,0,1;0rad)
  AttachmentSupport = -> [Revolution042]
  MapMode = 2
  Placement = pos=(253,0,0) rot=(0,0,1;0rad)
FEATURE [Sketcher::SketchObject] Sketch079
  ArcFitTolerance = 0
  AttachmentSupport = -> [XY_Plane025]
  FullyConstrained = true
  MakeInternals = false
  MapMode = 5
  sketch-geometry (2):
    g0: LineSegment StartX=-35 StartY=4.3e-15 StartZ=0 EndX=35 EndY=4.3e-15 EndZ=0
    g1: ArcOfCircle CenterX=0 CenterY=0 CenterZ=0 NormalX=0 NormalY=0 NormalZ=1 AngleXU=0 Radius=35 StartAngle=0 EndAngle=3.14159
  constraints (6):
    c: Horizontal(g0)
    c: PointOnObject(g1,g0)
    c: Coincident(g1,g0)
    c: Coincident(g1,g0)
    c: Coincident(g1,g-1)
    c: Radius(g1) = 35
FEATURE [PartDesign::Groove] Groove034  label="Left elbow cut"
  Angle = 360
  Angle2 = 60
  Axis = (1,0,0)
  Base = (0,0,0)
  BaseFeature = -> Revolution042
  Profile = -> Sketch079
  ReferenceAxis = -> Sketch079 [H_Axis]
  Reversed = true
  Suppressed = false
  Type = 0
FEATURE [PartDesign::Fillet] Fillet034  label="Left elbow fillet"
  Base = -> Groove034 [Edge2]
  BaseFeature = -> Groove034
  Radius = 3
  SupportTransform = false
  Suppressed = false
  UseAllEdges = false
FEATURE [Sketcher::SketchObject] Sketch080
  ArcFitTolerance = 0
  AttachmentSupport = -> [XY_Plane025]
  FullyConstrained = true
  MakeInternals = false
  MapMode = 5
  sketch-geometry (2):
    g0: LineSegment StartX=228 StartY=0 StartZ=0 EndX=278 EndY=0 EndZ=0
    g1: ArcOfCircle CenterX=253 CenterY=0 CenterZ=0 NormalX=0 NormalY=0 NormalZ=1 AngleXU=0 Radius=25 StartAngle=-9e-16 EndAngle=3.14159
  constraints (7):
    c: Horizontal(g0)
    c: PointOnObject(g1,g0)
    c: Coincident(g1,g0)
    c: Coincident(g1,g0)
    c: Horizontal(g1,g-1)
    c: DistanceX(g-1,g1) = 253
    c: Radius(g1) = 25
FEATURE [PartDesign::Groove] Groove035  label="Left wrist cut"
  Angle = 360
  Angle2 = 60
  Axis = (1,0,0)
  Base = (0,0,0)
  BaseFeature = -> Fillet034
  Profile = -> Sketch080
  ReferenceAxis = -> Sketch080 [H_Axis]
  Reversed = true
  Suppressed = false
  Type = 0
FEATURE [PartDesign::Fillet] Fillet035  label="Left wrist fillet"
  Base = -> Groove035 [Edge1]
  BaseFeature = -> Groove035
  Radius = 3
  SupportTransform = false
  Suppressed = false
  UseAllEdges = false
FEATURE [PartDesign::Revolution] Revolution043  label="Left wrist"
  Angle = 360
  Angle2 = 60
  Axis = (1,0,0)
  Base = (0,0,0)
  BaseFeature = -> Fillet035
  Profile = -> Sketch080
  ReferenceAxis = -> Sketch080 [H_Axis]
  Suppressed = false
  Type = 0
FEATURE [PartDesign::Body] Body023  label="Left Forearm"
  AllowCompound = false
  Group = -> [Sketch078,Revolution042,Sketch079,Groove034,Fillet034,Sketch080,Groove035,Fillet035,Revolution043,Local_CS038,Local_CS039]
  Origin = -> Origin025
  Placement = pos=(504,1455,0) rot=(0,0,1;0rad)
  Tip = -> Revolution043
FEATURE [Sketcher::SketchObject] Sketch081
  ArcFitTolerance = 0
  AttachmentSupport = -> [XY_Plane026]
  FullyConstrained = true
  MakeInternals = false
  MapMode = 5
  sketch-geometry (10):
    g0: LineSegment StartX=6.14917 StartY=0 StartZ=0 EndX=149.382 EndY=0 EndZ=0
    g1-g5: Circle [constr] x5 (B-spline internal-alignment scaffolding for g6; pole/knot coordinates omitted)
    g6: BSplineCurve PolesCount=5 KnotsCount=3 Degree=3 IsPeriodic=0
    g7: GeomPoint [constr] X=6.14917 Y=0 Z=0
    g8: GeomPoint [constr] X=80.1264 Y=42.7238 Z=0
    g9: GeomPoint [constr] X=149.382 Y=0 Z=0
  constraints (12):
    c: PointOnObject(g0,g-1)
    c: Horizontal(g0)
    c: Weight(g1) = 1
    c: Coincident(g6,g0)
    c: Equal(g1, g2-g5) x4
    c: Coincident(g6,g0)
    c: InternalAlignment(g1-g5 -> g6) x5
    c: InternalAlignment(g7,g6)
    c: InternalAlignment(g8,g6)
    c: InternalAlignment(g9,g6)
    c: Vertical(g0,g4)
    c: Block(g6)
FEATURE [PartDesign::Revolution] Revolution044  label="L hand main body"
  Angle = 360
  Angle2 = 60
  Axis = (1,0,0)
  Base = (0,0,0)
  Profile = -> Sketch081
  ReferenceAxis = -> Sketch081 [H_Axis]
  Suppressed = false
  Type = 0
FEATURE [PartDesign::CoordinateSystem] Local_CS040  label="Left Hand/Wrist LCS"
  AttacherType = Attacher::AttachEngine3D
  AttachmentSupport = -> [Revolution044]
  MapMode = 2
FEATURE [Sketcher::SketchObject] Sketch082
  ArcFitTolerance = 0
  AttachmentSupport = -> [XY_Plane026]
  FullyConstrained = true
  MakeInternals = false
  MapMode = 5
  sketch-geometry (2):
    g0: LineSegment StartX=-25 StartY=3.1e-15 StartZ=0 EndX=25 EndY=3.1e-15 EndZ=0
    g1: ArcOfCircle CenterX=0 CenterY=0 CenterZ=0 NormalX=0 NormalY=0 NormalZ=1 AngleXU=0 Radius=25 StartAngle=0 EndAngle=3.14159
  constraints (6):
    c: Horizontal(g0)
    c: PointOnObject(g1,g0)
    c: Coincident(g1,g0)
    c: Coincident(g1,g0)
    c: Coincident(g1,g-1)
    c: Radius(g1) = 25
FEATURE [PartDesign::Groove] Groove036  label="wrist cut001"
  Angle = 360
  Angle2 = 60
  Axis = (1,0,0)
  Base = (0,0,0)
  BaseFeature = -> Revolution044
  Profile = -> Sketch082
  ReferenceAxis = -> Sketch082 [H_Axis]
  Reversed = true
  Suppressed = false
  Type = 0
FEATURE [PartDesign::Fillet] Fillet036  label="wrist fillet001"
  Base = -> Groove036 [Edge1]
  BaseFeature = -> Groove036
  Radius = 3
  SupportTransform = false
  Suppressed = false
  UseAllEdges = false
FEATURE [Sketcher::SketchObject] Sketch083
  ArcFitTolerance = 0
  AttachmentSupport = -> [YZ_Plane026]
  FullyConstrained = true
  MakeInternals = false
  MapMode = 5
  Placement = pos=(0,0,0) rot=(0.57735,0.57735,0.57735;2.0944rad)
  sketch-geometry (3):
    g0: ArcOfCircle CenterX=0 CenterY=125.857 CenterZ=0 NormalX=0 NormalY=0 NormalZ=1 AngleXU=0 Radius=99.8092 StartAngle=3.99571 EndAngle=5.39163
    g1: LineSegment StartX=-65.5632 StartY=50.6013 StartZ=0 EndX=0 EndY=125.857 EndZ=0
    g2: LineSegment StartX=0 StartY=125.857 StartZ=0 EndX=62.7007 EndY=48.2002 EndZ=0
  constraints (6):
    c: PointOnObject(g0,g-2)
    c: Coincident(g1,g0)
    c: Coincident(g1,g0)
    c: Coincident(g2,g0)
    c: Coincident(g2,g0)
    c: Block(g0)
FEATURE [PartDesign::Pocket] Pocket014
  BaseFeature = -> Fillet036
  Direction = (1,0,0)
  Length = 5
  Length2 = 5
  Profile = -> Sketch083
  ReferenceAxis = -> Sketch083 [N_Axis]
  Suppressed = false
  Type = 1
  UseCustomVector = true
FEATURE [Sketcher::SketchObject] Sketch084
  ArcFitTolerance = 0
  AttachmentSupport = -> [YZ_Plane026]
  FullyConstrained = true
  MakeInternals = false
  MapMode = 5
  Placement = pos=(0,0,0) rot=(0.57735,0.57735,0.57735;2.0944rad)
  sketch-geometry (4):
    g0: ArcOfCircle CenterX=0 CenterY=78.6838 CenterZ=0 NormalX=0 NormalY=0 NormalZ=1 AngleXU=0 Radius=107.987 StartAngle=3.91888 EndAngle=5.56935
    g1: LineSegment StartX=81.6221 StartY=7.98042 StartZ=0 EndX=81.6221 EndY=-69.912 EndZ=0
    g2: LineSegment StartX=81.6221 StartY=-69.912 StartZ=0 EndX=-76.9748 EndY=-69.912 EndZ=0
    g3: LineSegment StartX=-76.9748 StartY=-69.912 StartZ=0 EndX=-76.9748 EndY=2.94733 EndZ=0
  constraints (10):
    c: PointOnObject(g0,g-2)
    c: Coincident(g0,g1)
    c: Coincident(g1,g2)
    c: Horizontal(g2)
    c: Coincident(g2,g3)
    c: Coincident(g3,g0)
    c: Vertical(g3)
    c: Vertical(g1)
    c: Block(g0)
    c: Block(g2)
FEATURE [PartDesign::Pocket] Pocket015
  BaseFeature = -> Pocket014
  Direction = (1,0,0)
  Length = 5
  Length2 = 5
  Profile = -> Sketch084
  ReferenceAxis = -> Sketch084 [N_Axis]
  Suppressed = false
  Type = 1
  UseCustomVector = true
FEATURE [PartDesign::Body] Body024  label="Left hand"
  AllowCompound = false
  Group = -> [Sketch081,Revolution044,Sketch082,Groove036,Fillet036,Sketch083,Pocket014,Sketch084,Pocket015,Local_CS040]
  Origin = -> Origin026
  Placement = pos=(757,1455,0) rot=(0,0,1;0rad)
  Tip = -> Pocket015
FEATURE [Sketcher::SketchObject] Sketch085
  ArcFitTolerance = 0
  AttachmentSupport = -> [XY_Plane027]
  FullyConstrained = true
  MakeInternals = false
  MapMode = 5
  sketch-geometry (12):
    g0: LineSegment StartX=15.9442 StartY=0 StartZ=0 EndX=306.848 EndY=0 EndZ=0
    g1-g6: Circle [constr] x6 (B-spline internal-alignment scaffolding for g7; pole/knot coordinates omitted)
    g7: BSplineCurve PolesCount=6 KnotsCount=4 Degree=3 IsPeriodic=0
    g8-g11: GeomPoint [constr] x4 (B-spline internal-alignment scaffolding for g7; pole/knot coordinates omitted)
  constraints (9):
    c: PointOnObject(g0,g-1)
    c: Horizontal(g0)
    c: Weight(g1) = 1
    c: Coincident(g7,g0)
    c: Equal(g1, g2-g6) x5
    c: Coincident(g7,g0)
    c: InternalAlignment(g1-g6 -> g7) x6
    c: InternalAlignment(g8-g11 -> g7) x4
    c: Block(g7)
FEATURE [PartDesign::Revolution] Revolution045  label="R Upper limb"
  Angle = 360
  Angle2 = 60
  Axis = (1,0,0)
  Base = (0,0,0)
  Profile = -> Sketch085
  ReferenceAxis = -> Sketch085 [H_Axis]
  Suppressed = false
  Type = 0
FEATURE [PartDesign::CoordinateSystem] Local_CS041  label="Right upper limb/Shoulder LCS"
  AttacherType = Attacher::AttachEngine3D
  AttachmentOffset = pos=(0,0,0) rot=(0,0,1;3.14159rad)
  AttachmentSupport = -> [Revolution045]
  MapMode = 2
  Placement = pos=(0,0,0) rot=(0,0,1;3.14159rad)
FEATURE [PartDesign::CoordinateSystem] Local_CS042  label="Right upper limb/Elbow LCS"
  AttacherType = Attacher::AttachEngine3D
  AttachmentOffset = pos=(320,0,0) rot=(0,0,1;3.14159rad)
  AttachmentSupport = -> [Revolution045]
  MapMode = 2
  Placement = pos=(320,0,0) rot=(0,0,1;3.14159rad)
FEATURE [Sketcher::SketchObject] Sketch086
  ArcFitTolerance = 0
  AttachmentSupport = -> [XY_Plane027]
  FullyConstrained = true
  MakeInternals = false
  MapMode = 5
  sketch-geometry (2):
    g0: LineSegment StartX=-60 StartY=0 StartZ=0 EndX=60 EndY=0 EndZ=0
    g1: ArcOfCircle CenterX=0 CenterY=0 CenterZ=0 NormalX=0 NormalY=0 NormalZ=1 AngleXU=0 Radius=60 StartAngle=0 EndAngle=3.14159
  constraints (6):
    c: Horizontal(g0)
    c: PointOnObject(g1,g0)
    c: Coincident(g1,g0)
    c: Coincident(g1,g0)
    c: Coincident(g1,g-1)
    c: Radius(g1) = 60
FEATURE [PartDesign::Groove] Groove037  label="R Sloulder cut"
  Angle = 360
  Angle2 = 60
  Axis = (1,0,0)
  Base = (0,0,0)
  BaseFeature = -> Revolution045
  Profile = -> Sketch086
  ReferenceAxis = -> Sketch086 [H_Axis]
  Reversed = true
  Suppressed = false
  Type = 0
FEATURE [PartDesign::Fillet] Fillet037  label="R Shoulder fillet"
  Base = -> Groove037 [Edge2]
  BaseFeature = -> Groove037
  Radius = 6
  SupportTransform = false
  Suppressed = false
  UseAllEdges = false
FEATURE [Sketcher::SketchObject] Sketch087
  ArcFitTolerance = 0
  AttachmentSupport = -> [XY_Plane027]
  FullyConstrained = true
  MakeInternals = false
  MapMode = 5
  sketch-geometry (2):
    g0: LineSegment StartX=285 StartY=0 StartZ=0 EndX=355 EndY=0 EndZ=0
    g1: ArcOfCircle CenterX=320 CenterY=0 CenterZ=0 NormalX=0 NormalY=0 NormalZ=1 AngleXU=0 Radius=35 StartAngle=0 EndAngle=3.14159
  constraints (7):
    c: Horizontal(g0)
    c: PointOnObject(g1,g0)
    c: Coincident(g1,g0)
    c: Coincident(g1,g0)
    c: Horizontal(g1,g-1)
    c: DistanceX(g-1,g1) = 320
    c: Radius(g1) = 35
FEATURE [PartDesign::Groove] Groove038  label="R Elbow cut"
  Angle = 360
  Angle2 = 60
  Axis = (1,0,0)
  Base = (0,0,0)
  BaseFeature = -> Fillet037
  Profile = -> Sketch087
  ReferenceAxis = -> Sketch087 [H_Axis]
  Reversed = true
  Suppressed = false
  Type = 0
FEATURE [PartDesign::Fillet] Fillet038  label="R Elbow fillet"
  Base = -> Groove038 [Edge1]
  BaseFeature = -> Groove038
  Radius = 3
  SupportTransform = false
  Suppressed = false
  UseAllEdges = false
FEATURE [PartDesign::Revolution] Revolution046  label="R Elbow"
  Angle = 360
  Angle2 = 60
  Axis = (1,0,0)
  Base = (0,0,0)
  BaseFeature = -> Fillet038
  Profile = -> Sketch087
  ReferenceAxis = -> Sketch087 [H_Axis]
  Suppressed = false
  Type = 0
FEATURE [PartDesign::Body] Body025  label="Right Upper limb"
  AllowCompound = false
  Group = -> [Sketch085,Revolution045,Sketch086,Groove037,Fillet037,Sketch087,Groove038,Fillet038,Revolution046,Local_CS041,Local_CS042]
  Origin = -> Origin027
  Placement = pos=(-184,1455,0) rot=(0,0,1;3.14159rad)
  Tip = -> Revolution046
FEATURE [Sketcher::SketchObject] Sketch088
  ArcFitTolerance = 0
  AttachmentSupport = -> [XY_Plane028]
  FullyConstrained = true
  MakeInternals = false
  MapMode = 5
  sketch-geometry (12):
    g0: LineSegment StartX=5.14795 StartY=0 StartZ=0 EndX=267.265 EndY=0 EndZ=0
    g1-g6: Circle [constr] x6 (B-spline internal-alignment scaffolding for g7; pole/knot coordinates omitted)
    g7: BSplineCurve PolesCount=6 KnotsCount=4 Degree=3 IsPeriodic=0
    g8-g11: GeomPoint [constr] x4 (B-spline internal-alignment scaffolding for g7; pole/knot coordinates omitted)
  constraints (9):
    c: PointOnObject(g0,g-1)
    c: Horizontal(g0)
    c: Weight(g1) = 1
    c: Coincident(g7,g0)
    c: Equal(g1, g2-g6) x5
    c: Coincident(g7,g0)
    c: InternalAlignment(g1-g6 -> g7) x6
    c: InternalAlignment(g8-g11 -> g7) x4
    c: Block(g7)
FEATURE [PartDesign::Revolution] Revolution047  label="Right Forearm main body"
  Angle = 360
  Angle2 = 60
  Axis = (1,0,0)
  Base = (0,0,0)
  Profile = -> Sketch088
  ReferenceAxis = -> Sketch088 [H_Axis]
  Suppressed = false
  Type = 0
FEATURE [PartDesign::CoordinateSystem] Local_CS043  label="Right Forearm/Elbow"
  AttacherType = Attacher::AttachEngine3D
  AttachmentOffset = pos=(0,0,0) rot=(0,0,1;3.14159rad)
  AttachmentSupport = -> [Revolution047]
  MapMode = 2
  Placement = pos=(0,0,0) rot=(0,0,1;3.14159rad)
FEATURE [PartDesign::CoordinateSystem] Local_CS044  label="Right Forearm/Wrist"
  AttacherType = Attacher::AttachEngine3D
  AttachmentOffset = pos=(253,0,0) rot=(0,0,1;3.14159rad)
  AttachmentSupport = -> [Revolution047]
  MapMode = 2
  Placement = pos=(253,0,0) rot=(0,0,1;3.14159rad)
FEATURE [Sketcher::SketchObject] Sketch089
  ArcFitTolerance = 0
  AttachmentSupport = -> [XY_Plane028]
  FullyConstrained = true
  MakeInternals = false
  MapMode = 5
  sketch-geometry (2):
    g0: LineSegment StartX=-35 StartY=4.3e-15 StartZ=0 EndX=35 EndY=4.3e-15 EndZ=0
    g1: ArcOfCircle CenterX=0 CenterY=0 CenterZ=0 NormalX=0 NormalY=0 NormalZ=1 AngleXU=0 Radius=35 StartAngle=0 EndAngle=3.14159
  constraints (6):
    c: Horizontal(g0)
    c: PointOnObject(g1,g0)
    c: Coincident(g1,g0)
    c: Coincident(g1,g0)
    c: Coincident(g1,g-1)
    c: Radius(g1) = 35
FEATURE [PartDesign::Groove] Groove039  label="Right elbow cut"
  Angle = 360
  Angle2 = 60
  Axis = (1,0,0)
  Base = (0,0,0)
  BaseFeature = -> Revolution047
  Profile = -> Sketch089
  ReferenceAxis = -> Sketch089 [H_Axis]
  Reversed = true
  Suppressed = false
  Type = 0
FEATURE [PartDesign::Fillet] Fillet039  label="Right elbow fillet"
  Base = -> Groove039 [Edge2]
  BaseFeature = -> Groove039
  Radius = 3
  SupportTransform = false
  Suppressed = false
  UseAllEdges = false
FEATURE [Sketcher::SketchObject] Sketch090
  ArcFitTolerance = 0
  AttachmentSupport = -> [XY_Plane028]
  FullyConstrained = true
  MakeInternals = false
  MapMode = 5
  sketch-geometry (2):
    g0: LineSegment StartX=228 StartY=0 StartZ=0 EndX=278 EndY=0 EndZ=0
    g1: ArcOfCircle CenterX=253 CenterY=0 CenterZ=0 NormalX=0 NormalY=0 NormalZ=1 AngleXU=0 Radius=25 StartAngle=-9e-16 EndAngle=3.14159
  constraints (7):
    c: Horizontal(g0)
    c: PointOnObject(g1,g0)
    c: Coincident(g1,g0)
    c: Coincident(g1,g0)
    c: Horizontal(g1,g-1)
    c: DistanceX(g-1,g1) = 253
    c: Radius(g1) = 25
FEATURE [PartDesign::Groove] Groove040  label="Right wrist cut"
  Angle = 360
  Angle2 = 60
  Axis = (1,0,0)
  Base = (0,0,0)
  BaseFeature = -> Fillet039
  Profile = -> Sketch090
  ReferenceAxis = -> Sketch090 [H_Axis]
  Reversed = true
  Suppressed = false
  Type = 0
FEATURE [PartDesign::Fillet] Fillet040  label="Right wrist fillet"
  Base = -> Groove040 [Edge1]
  BaseFeature = -> Groove040
  Radius = 3
  SupportTransform = false
  Suppressed = false
  UseAllEdges = false
FEATURE [PartDesign::Revolution] Revolution048  label="Right wrist"
  Angle = 360
  Angle2 = 60
  Axis = (1,0,0)
  Base = (0,0,0)
  BaseFeature = -> Fillet040
  Profile = -> Sketch090
  ReferenceAxis = -> Sketch090 [H_Axis]
  Suppressed = false
  Type = 0
FEATURE [PartDesign::Body] Body026  label="Right Forearm"
  AllowCompound = false
  Group = -> [Sketch088,Revolution047,Sketch089,Groove039,Fillet039,Sketch090,Groove040,Fillet040,Revolution048,Local_CS043,Local_CS044]
  Origin = -> Origin028
  Placement = pos=(-504,1455,0) rot=(0,0,1;3.14159rad)
  Tip = -> Revolution048
FEATURE [Sketcher::SketchObject] Sketch091
  ArcFitTolerance = 0
  AttachmentSupport = -> [XY_Plane029]
  FullyConstrained = true
  MakeInternals = false
  MapMode = 5
  sketch-geometry (10):
    g0: LineSegment StartX=6.14917 StartY=0 StartZ=0 EndX=149.382 EndY=0 EndZ=0
    g1-g5: Circle [constr] x5 (B-spline internal-alignment scaffolding for g6; pole/knot coordinates omitted)
    g6: BSplineCurve PolesCount=5 KnotsCount=3 Degree=3 IsPeriodic=0
    g7: GeomPoint [constr] X=6.14917 Y=0 Z=0
    g8: GeomPoint [constr] X=80.1264 Y=42.7238 Z=0
    g9: GeomPoint [constr] X=149.382 Y=0 Z=0
  constraints (12):
    c: PointOnObject(g0,g-1)
    c: Horizontal(g0)
    c: Weight(g1) = 1
    c: Coincident(g6,g0)
    c: Equal(g1, g2-g5) x4
    c: Coincident(g6,g0)
    c: InternalAlignment(g1-g5 -> g6) x5
    c: InternalAlignment(g7,g6)
    c: InternalAlignment(g8,g6)
    c: InternalAlignment(g9,g6)
    c: Vertical(g0,g4)
    c: Block(g6)
FEATURE [PartDesign::Revolution] Revolution049  label="R hand main body"
  Angle = 360
  Angle2 = 60
  Axis = (1,0,0)
  Base = (0,0,0)
  Profile = -> Sketch091
  ReferenceAxis = -> Sketch091 [H_Axis]
  Suppressed = false
  Type = 0
FEATURE [PartDesign::CoordinateSystem] Local_CS045  label="Right Hand/Wrist LCS"
  AttacherType = Attacher::AttachEngine3D
  AttachmentOffset = pos=(0,0,0) rot=(0,0,1;3.14159rad)
  AttachmentSupport = -> [Revolution049]
  MapMode = 2
  Placement = pos=(0,0,0) rot=(0,0,1;3.14159rad)
FEATURE [Sketcher::SketchObject] Sketch092
  ArcFitTolerance = 0
  AttachmentSupport = -> [XY_Plane029]
  FullyConstrained = true
  MakeInternals = false
  MapMode = 5
  sketch-geometry (2):
    g0: LineSegment StartX=-25 StartY=0 StartZ=0 EndX=25 EndY=0 EndZ=0
    g1: ArcOfCircle CenterX=0 CenterY=0 CenterZ=0 NormalX=0 NormalY=0 NormalZ=1 AngleXU=0 Radius=25 StartAngle=0 EndAngle=3.14159
  constraints (6):
    c: Horizontal(g0)
    c: PointOnObject(g1,g0)
    c: Coincident(g1,g0)
    c: Coincident(g1,g0)
    c: Coincident(g1,g-1)
    c: Radius(g1) = 25
FEATURE [PartDesign::Groove] Groove041  label="wrist cut"
  Angle = 360
  Angle2 = 60
  Axis = (1,0,0)
  Base = (0,0,0)
  BaseFeature = -> Revolution049
  Profile = -> Sketch092
  ReferenceAxis = -> Sketch092 [H_Axis]
  Reversed = true
  Suppressed = false
  Type = 0
FEATURE [PartDesign::Fillet] Fillet041  label="wrist fillet"
  Base = -> Groove041 [Edge1]
  BaseFeature = -> Groove041
  Radius = 3
  SupportTransform = false
  Suppressed = false
  UseAllEdges = false
FEATURE [Sketcher::SketchObject] Sketch093
  ArcFitTolerance = 0
  AttachmentSupport = -> [YZ_Plane029]
  FullyConstrained = true
  MakeInternals = false
  MapMode = 5
  Placement = pos=(0,0,0) rot=(0.57735,0.57735,0.57735;2.0944rad)
  sketch-geometry (3):
    g0: ArcOfCircle CenterX=0 CenterY=125.857 CenterZ=0 NormalX=0 NormalY=0 NormalZ=1 AngleXU=0 Radius=99.8092 StartAngle=3.99571 EndAngle=5.39163
    g1: LineSegment StartX=-65.5632 StartY=50.6013 StartZ=0 EndX=0 EndY=125.857 EndZ=0
    g2: LineSegment StartX=0 StartY=125.857 StartZ=0 EndX=62.7007 EndY=48.2002 EndZ=0
  constraints (6):
    c: PointOnObject(g0,g-2)
    c: Coincident(g1,g0)
    c: Coincident(g1,g0)
    c: Coincident(g2,g0)
    c: Coincident(g2,g0)
    c: Block(g0)
FEATURE [PartDesign::Pocket] Pocket016
  BaseFeature = -> Fillet041
  Direction = (1,0,0)
  Length = 5
  Length2 = 5
  Profile = -> Sketch093
  ReferenceAxis = -> Sketch093 [N_Axis]
  Suppressed = false
  Type = 1
  UseCustomVector = true
FEATURE [Sketcher::SketchObject] Sketch094
  ArcFitTolerance = 0
  AttachmentSupport = -> [YZ_Plane029]
  FullyConstrained = true
  MakeInternals = false
  MapMode = 5
  Placement = pos=(0,0,0) rot=(0.57735,0.57735,0.57735;2.0944rad)
  sketch-geometry (4):
    g0: ArcOfCircle CenterX=0 CenterY=78.6838 CenterZ=0 NormalX=0 NormalY=0 NormalZ=1 AngleXU=0 Radius=107.987 StartAngle=3.91888 EndAngle=5.56935
    g1: LineSegment StartX=81.6221 StartY=7.98042 StartZ=0 EndX=81.6221 EndY=-69.912 EndZ=0
    g2: LineSegment StartX=81.6221 StartY=-69.912 StartZ=0 EndX=-76.9748 EndY=-69.912 EndZ=0
    g3: LineSegment StartX=-76.9748 StartY=-69.912 StartZ=0 EndX=-76.9748 EndY=2.94733 EndZ=0
  constraints (10):
    c: PointOnObject(g0,g-2)
    c: Coincident(g0,g1)
    c: Coincident(g1,g2)
    c: Horizontal(g2)
    c: Coincident(g2,g3)
    c: Coincident(g3,g0)
    c: Vertical(g3)
    c: Vertical(g1)
    c: Block(g0)
    c: Block(g2)
FEATURE [PartDesign::Pocket] Pocket017
  BaseFeature = -> Pocket016
  Direction = (1,0,0)
  Length = 5
  Length2 = 5
  Profile = -> Sketch094
  ReferenceAxis = -> Sketch094 [N_Axis]
  Suppressed = false
  Type = 1
  UseCustomVector = true
FEATURE [PartDesign::Body] Body027  label="Right hand"
  AllowCompound = false
  Group = -> [Sketch091,Revolution049,Sketch092,Groove041,Fillet041,Sketch093,Pocket016,Sketch094,Pocket017,Local_CS045]
  Origin = -> Origin029
  Placement = pos=(-757,1455,0) rot=(0,0,1;3.14159rad)
  Tip = -> Pocket017
FEATURE [Sketcher::SketchObject] Sketch095
  ArcFitTolerance = 0
  AttachmentSupport = -> [XY_Plane030]
  FullyConstrained = true
  MakeInternals = false
  MapMode = 5
  sketch-geometry (14):
    g0: LineSegment StartX=0 StartY=-29.246 StartZ=0 EndX=0 EndY=-395.97 EndZ=0
    g1-g7: Circle [constr] x7 (B-spline internal-alignment scaffolding for g8; pole/knot coordinates omitted)
    g8: BSplineCurve PolesCount=7 KnotsCount=5 Degree=3 IsPeriodic=0
    g9-g13: GeomPoint [constr] x5 (B-spline internal-alignment scaffolding for g8; pole/knot coordinates omitted)
  constraints (11):
    c: PointOnObject(g0,g-2)
    c: Vertical(g0)
    c: Weight(g1) = 1
    c: Coincident(g8,g0)
    c: Equal(g1, g2-g7) x6
    c: Coincident(g8,g0)
    c: InternalAlignment(g1-g7 -> g8) x7
    c: InternalAlignment(g9-g13 -> g8) x5
    c: Horizontal(g0,g6)
    c: Horizontal(g0,g2)
    c: Block(g8)
FEATURE [PartDesign::Revolution] Revolution050  label="L Thigh main body"
  Angle = 360
  Angle2 = 60
  Axis = (0,1,0)
  Base = (0,0,0)
  Profile = -> Sketch095
  ReferenceAxis = -> Sketch095 [V_Axis]
  Reversed = true
  Suppressed = false
  Type = 0
FEATURE [PartDesign::CoordinateSystem] Local_CS046  label="Left Thigh/Big joint LCS"
  AttacherType = Attacher::AttachEngine3D
  AttachmentSupport = -> [Revolution050]
  MapMode = 2
FEATURE [PartDesign::CoordinateSystem] Local_CS047  label="Left Thigh/Knee LCS"
  AttacherType = Attacher::AttachEngine3D
  AttachmentOffset = pos=(0,-403,0) rot=(0,0,1;0rad)
  AttachmentSupport = -> [Revolution050]
  MapMode = 2
  Placement = pos=(0,-403,0) rot=(0,0,1;0rad)
FEATURE [Sketcher::SketchObject] Sketch096
  ArcFitTolerance = 0
  AttachmentSupport = -> [XY_Plane030]
  FullyConstrained = true
  MakeInternals = false
  MapMode = 5
  sketch-geometry (2):
    g0: LineSegment StartX=-1.1e-14 StartY=60 StartZ=0 EndX=-1.1e-14 EndY=-60 EndZ=0
    g1: ArcOfCircle CenterX=0 CenterY=0 CenterZ=0 NormalX=0 NormalY=0 NormalZ=1 AngleXU=0 Radius=60 StartAngle=4.71239 EndAngle=7.85398
  constraints (6):
    c: Vertical(g0)
    c: PointOnObject(g1,g0)
    c: Coincident(g1,g0)
    c: Coincident(g1,g0)
    c: Coincident(g1,g-1)
    c: Radius(g1) = 60
FEATURE [PartDesign::Groove] Groove042  label="L Big joint"
  Angle = 360
  Angle2 = 60
  Axis = (0,1,0)
  Base = (0,0,0)
  BaseFeature = -> Revolution050
  Profile = -> Sketch096
  ReferenceAxis = -> Sketch096 [V_Axis]
  Suppressed = false
  Type = 0
FEATURE [PartDesign::Fillet] Fillet042
  Base = -> Groove042 [Edge1]
  BaseFeature = -> Groove042
  Radius = 6
  SupportTransform = false
  Suppressed = false
  UseAllEdges = false
FEATURE [Sketcher::SketchObject] Sketch097
  ArcFitTolerance = 0
  AttachmentSupport = -> [XY_Plane030]
  FullyConstrained = true
  MakeInternals = false
  MapMode = 5
  sketch-geometry (2):
    g0: LineSegment StartX=-6.4e-15 StartY=-368 StartZ=0 EndX=-6.4e-15 EndY=-438 EndZ=0
    g1: ArcOfCircle CenterX=0 CenterY=-403 CenterZ=0 NormalX=0 NormalY=0 NormalZ=1 AngleXU=0 Radius=35 StartAngle=4.71239 EndAngle=7.85398
  constraints (7):
    c: Vertical(g0)
    c: PointOnObject(g1,g0)
    c: Coincident(g1,g0)
    c: Coincident(g1,g0)
    c: PointOnObject(g1,g-2)
    c: DistanceY(g1,g-1) = 403
    c: Radius(g1) = 35
FEATURE [PartDesign::Groove] Groove043  label="L Knee cut"
  Angle = 360
  Angle2 = 60
  Axis = (0,1,0)
  Base = (0,0,0)
  BaseFeature = -> Fillet042
  Profile = -> Sketch097
  ReferenceAxis = -> Sketch097 [V_Axis]
  Suppressed = false
  Type = 0
FEATURE [PartDesign::Fillet] Fillet043
  Base = -> Groove043 [Edge1]
  BaseFeature = -> Groove043
  Radius = 3
  SupportTransform = false
  Suppressed = false
  UseAllEdges = false
FEATURE [PartDesign::Revolution] Revolution051  label="L Knee"
  Angle = 360
  Angle2 = 60
  Axis = (0,1,0)
  Base = (0,0,0)
  BaseFeature = -> Fillet043
  Profile = -> Sketch097
  ReferenceAxis = -> Sketch097 [V_Axis]
  Reversed = true
  Suppressed = false
  Type = 0
FEATURE [PartDesign::Body] Body028  label="Left Thigh"
  AllowCompound = false
  Group = -> [Sketch095,Revolution050,Sketch096,Groove042,Fillet042,Sketch097,Groove043,Fillet043,Revolution051,Local_CS046,Local_CS047]
  Origin = -> Origin030
  Placement = pos=(75,900,0) rot=(0,0,1;0rad)
  Tip = -> Revolution051
FEATURE [Sketcher::SketchObject] Sketch098
  ArcFitTolerance = 0
  AttachmentSupport = -> [XY_Plane031]
  FullyConstrained = true
  MakeInternals = false
  MapMode = 5
  sketch-geometry (14):
    g0: LineSegment StartX=0 StartY=0 StartZ=0 EndX=0 EndY=-428.766 EndZ=0
    g1-g7: Circle [constr] x7 (B-spline internal-alignment scaffolding for g8; pole/knot coordinates omitted)
    g8: BSplineCurve PolesCount=7 KnotsCount=5 Degree=3 IsPeriodic=0
    g9-g13: GeomPoint [constr] x5 (B-spline internal-alignment scaffolding for g8; pole/knot coordinates omitted)
  constraints (9):
    c: Vertical(g0)
    c: PointOnObject(g0,g-2)
    c: Weight(g1) = 1
    c: Coincident(g8,g0)
    c: Equal(g1, g2-g7) x6
    c: Coincident(g8,g0)
    c: InternalAlignment(g1-g7 -> g8) x7
    c: InternalAlignment(g9-g13 -> g8) x5
    c: Block(g8)
FEATURE [PartDesign::Revolution] Revolution052  label="L Shin main body"
  Angle = 360
  Angle2 = 60
  Axis = (0,1,0)
  Base = (0,0,0)
  Profile = -> Sketch098
  ReferenceAxis = -> Sketch098 [V_Axis]
  Reversed = true
  Suppressed = false
  Type = 0
FEATURE [PartDesign::CoordinateSystem] Local_CS048  label="Left Shin/Knee"
  AttacherType = Attacher::AttachEngine3D
  AttachmentSupport = -> [Revolution052]
  MapMode = 2
FEATURE [PartDesign::CoordinateSystem] Local_CS049  label="Left Shin/Ankle"
  AttacherType = Attacher::AttachEngine3D
  AttachmentOffset = pos=(0,-435,0) rot=(0,0,1;0rad)
  AttachmentSupport = -> [Revolution052]
  MapMode = 2
  Placement = pos=(0,-435,0) rot=(0,0,1;0rad)
FEATURE [Sketcher::SketchObject] Sketch099
  ArcFitTolerance = 0
  AttachmentSupport = -> [XY_Plane031]
  FullyConstrained = true
  MakeInternals = false
  MapMode = 5
  sketch-geometry (2):
    g0: LineSegment StartX=0 StartY=35 StartZ=0 EndX=0 EndY=-35 EndZ=0
    g1: ArcOfCircle CenterX=0 CenterY=0 CenterZ=0 NormalX=0 NormalY=0 NormalZ=1 AngleXU=0 Radius=35 StartAngle=4.71239 EndAngle=7.85398
  constraints (6):
    c: PointOnObject(g1,g0)
    c: Coincident(g1,g0)
    c: Coincident(g1,g0)
    c: Vertical(g0)
    c: Coincident(g1,g-1)
    c: Radius(g1) = 35
FEATURE [PartDesign::Groove] Groove044  label="L knee cut"
  Angle = 360
  Angle2 = 60
  Axis = (0,1,0)
  Base = (0,0,0)
  BaseFeature = -> Revolution052
  Profile = -> Sketch099
  ReferenceAxis = -> Sketch099 [V_Axis]
  Suppressed = false
  Type = 0
FEATURE [PartDesign::Fillet] Fillet044
  Base = -> Groove044 [Edge1]
  BaseFeature = -> Groove044
  Radius = 3
  SupportTransform = false
  Suppressed = false
  UseAllEdges = false
FEATURE [Sketcher::SketchObject] Sketch100
  ArcFitTolerance = 0
  AttachmentSupport = -> [XY_Plane031]
  FullyConstrained = true
  MakeInternals = false
  MapMode = 5
  sketch-geometry (2):
    g0: LineSegment StartX=0 StartY=-410 StartZ=0 EndX=0 EndY=-460 EndZ=0
    g1: ArcOfCircle CenterX=0 CenterY=-435 CenterZ=0 NormalX=0 NormalY=0 NormalZ=1 AngleXU=0 Radius=25 StartAngle=4.71239 EndAngle=7.85398
  constraints (7):
    c: Vertical(g0)
    c: PointOnObject(g1,g0)
    c: Coincident(g1,g0)
    c: Coincident(g1,g0)
    c: PointOnObject(g1,g-2)
    c: DistanceY(g1,g-1) = 435
    c: Radius(g1) = 25
FEATURE [PartDesign::Groove] Groove045  label="L Ankle cut"
  Angle = 360
  Angle2 = 60
  Axis = (0,1,0)
  Base = (0,0,0)
  BaseFeature = -> Fillet044
  Profile = -> Sketch100
  ReferenceAxis = -> Sketch100 [V_Axis]
  Suppressed = false
  Type = 0
FEATURE [PartDesign::Fillet] Fillet045
  Base = -> Groove045 [Edge3]
  BaseFeature = -> Groove045
  Radius = 3
  SupportTransform = false
  Suppressed = false
  UseAllEdges = false
FEATURE [PartDesign::Revolution] Revolution053  label="L Ankle"
  Angle = 360
  Angle2 = 60
  Axis = (0,1,0)
  Base = (0,0,0)
  BaseFeature = -> Fillet045
  Profile = -> Sketch100
  ReferenceAxis = -> Sketch100 [V_Axis]
  Reversed = true
  Suppressed = false
  Type = 0
FEATURE [PartDesign::Body] Body029  label="Left Shin"
  AllowCompound = false
  Group = -> [Sketch098,Revolution052,Sketch099,Groove044,Fillet044,Sketch100,Groove045,Fillet045,Revolution053,Local_CS048,Local_CS049]
  Origin = -> Origin031
  Placement = pos=(75,497,0) rot=(0,0,1;0rad)
  Tip = -> Revolution053
FEATURE [Sketcher::SketchObject] Sketch101
  ArcFitTolerance = 0
  AttachmentSupport = -> [YZ_Plane032]
  FullyConstrained = true
  MakeInternals = false
  MapMode = 5
  Placement = pos=(0,0,0) rot=(0.57735,0.57735,0.57735;2.0944rad)
  sketch-geometry (18):
    g0: LineSegment StartX=-62 StartY=180 StartZ=0 EndX=-62 EndY=-40 EndZ=0
    g1-g9: Circle [constr] x9 (B-spline internal-alignment scaffolding for g10; pole/knot coordinates omitted)
    g10: BSplineCurve PolesCount=9 KnotsCount=7 Degree=3 IsPeriodic=0
    g11-g17: GeomPoint [constr] x7 (B-spline internal-alignment scaffolding for g10; pole/knot coordinates omitted)
  constraints (13):
    c: Vertical(g0)
    c: DistanceX(g0,g-1) = 62
    c: DistanceY(g0,g-1) = 40
    c: DistanceY(g0,g0) = 220
    c: Weight(g1) = 1
    c: Coincident(g10,g0)
    c: Equal(g1, g2-g9) x8
    c: Coincident(g10,g0)
    c: InternalAlignment(g1-g9 -> g10) x9
    c: InternalAlignment(g11-g17 -> g10) x7
    c: Horizontal(g0,g8)
    c: Horizontal(g0,g2)
    c: Block(g10)
FEATURE [PartDesign::Pad] Pad002  label="L foot main body"
  Direction = (1,0,0)
  Length = 100
  Length2 = 10
  Midplane = true
  Placement = pos=(0,0,0) rot=(1,1,1;2.0944rad)
  Profile = -> Sketch101
  ReferenceAxis = -> Sketch101 [N_Axis]
  Suppressed = false
  Type = 0
FEATURE [PartDesign::Fillet] Fillet046
  Base = -> Pad002 [Edge4,Edge6,Edge1,Edge5,Edge2]
  BaseFeature = -> Pad002
  Placement = pos=(0,0,0) rot=(1,1,1;2.0944rad)
  Radius = 6
  SupportTransform = false
  Suppressed = false
  UseAllEdges = false
FEATURE [PartDesign::CoordinateSystem] Local_CS050  label="Left Foot/Ankle"
  AttacherType = Attacher::AttachEngine3D
  AttachmentSupport = -> [Pad002]
  MapMode = 2
  Placement = pos=(0,0,0) rot=(0.57735,0.57735,0.57735;2.0944rad)
FEATURE [Sketcher::SketchObject] Sketch102
  ArcFitTolerance = 0
  AttachmentSupport = -> [XY_Plane032]
  FullyConstrained = true
  MakeInternals = false
  MapMode = 5
  sketch-geometry (2):
    g0: LineSegment StartX=7.7e-15 StartY=25 StartZ=0 EndX=7.7e-15 EndY=-25 EndZ=0
    g1: ArcOfCircle CenterX=0 CenterY=0 CenterZ=0 NormalX=0 NormalY=0 NormalZ=1 AngleXU=0 Radius=25 StartAngle=4.71239 EndAngle=7.85398
  constraints (6):
    c: Vertical(g0)
    c: PointOnObject(g1,g0)
    c: Coincident(g1,g0)
    c: Coincident(g1,g0)
    c: Coincident(g1,g-1)
    c: Radius(g1) = 25
FEATURE [PartDesign::Groove] Groove046  label="Ankle cut"
  Angle = 360
  Angle2 = 60
  Axis = (0,1,0)
  Base = (0,0,0)
  BaseFeature = -> Fillet046
  Placement = pos=(0,0,0) rot=(1,1,1;2.0944rad)
  Profile = -> Sketch102
  ReferenceAxis = -> Sketch102 [V_Axis]
  Suppressed = false
  Type = 0
FEATURE [PartDesign::Fillet] Fillet047
  Base = -> Groove046 [Edge20,Edge19]
  BaseFeature = -> Groove046
  Placement = pos=(0,0,0) rot=(1,1,1;2.0944rad)
  Radius = 3
  SupportTransform = false
  Suppressed = false
  UseAllEdges = false
FEATURE [PartDesign::Body] Body030  label="Left foot"
  AllowCompound = false
  Group = -> [Sketch101,Pad002,Fillet046,Sketch102,Groove046,Fillet047,Local_CS050]
  Origin = -> Origin032
  Placement = pos=(75,62,0) rot=(0,0,1;0rad)
  Tip = -> Fillet047
FEATURE [Sketcher::SketchObject] Sketch103
  ArcFitTolerance = 0
  AttachmentSupport = -> [XY_Plane033]
  FullyConstrained = true
  MakeInternals = false
  MapMode = 5
  sketch-geometry (14):
    g0: LineSegment StartX=0 StartY=-29.246 StartZ=0 EndX=0 EndY=-395.97 EndZ=0
    g1-g7: Circle [constr] x7 (B-spline internal-alignment scaffolding for g8; pole/knot coordinates omitted)
    g8: BSplineCurve PolesCount=7 KnotsCount=5 Degree=3 IsPeriodic=0
    g9-g13: GeomPoint [constr] x5 (B-spline internal-alignment scaffolding for g8; pole/knot coordinates omitted)
  constraints (11):
    c: PointOnObject(g0,g-2)
    c: Vertical(g0)
    c: Weight(g1) = 1
    c: Coincident(g8,g0)
    c: Equal(g1, g2-g7) x6
    c: Coincident(g8,g0)
    c: InternalAlignment(g1-g7 -> g8) x7
    c: InternalAlignment(g9-g13 -> g8) x5
    c: Horizontal(g0,g6)
    c: Horizontal(g0,g2)
    c: Block(g8)
FEATURE [PartDesign::Revolution] Revolution054  label="R Thigh main body"
  Angle = 360
  Angle2 = 60
  Axis = (0,1,0)
  Base = (0,0,0)
  Profile = -> Sketch103
  ReferenceAxis = -> Sketch103 [V_Axis]
  Reversed = true
  Suppressed = false
  Type = 0
FEATURE [PartDesign::CoordinateSystem] Local_CS051  label="Right Thigh/Big joint LCS"
  AttacherType = Attacher::AttachEngine3D
  AttachmentSupport = -> [Revolution054]
  MapMode = 2
FEATURE [PartDesign::CoordinateSystem] Local_CS052  label="Right Thigh/Knee LCS"
  AttacherType = Attacher::AttachEngine3D
  AttachmentOffset = pos=(0,-403,0) rot=(0,0,1;0rad)
  AttachmentSupport = -> [Revolution054]
  MapMode = 2
  Placement = pos=(0,-403,0) rot=(0,0,1;0rad)
FEATURE [Sketcher::SketchObject] Sketch104
  ArcFitTolerance = 0
  AttachmentSupport = -> [XY_Plane033]
  FullyConstrained = true
  MakeInternals = false
  MapMode = 5
  sketch-geometry (2):
    g0: LineSegment StartX=1.84e-14 StartY=60 StartZ=0 EndX=1.84e-14 EndY=-60 EndZ=0
    g1: ArcOfCircle CenterX=0 CenterY=0 CenterZ=0 NormalX=0 NormalY=0 NormalZ=1 AngleXU=0 Radius=60 StartAngle=4.71239 EndAngle=7.85398
  constraints (6):
    c: Vertical(g0)
    c: PointOnObject(g1,g0)
    c: Coincident(g1,g0)
    c: Coincident(g1,g0)
    c: Coincident(g1,g-1)
    c: Radius(g1) = 60
FEATURE [PartDesign::Groove] Groove047  label="R Big joint"
  Angle = 360
  Angle2 = 60
  Axis = (0,1,0)
  Base = (0,0,0)
  BaseFeature = -> Revolution054
  Profile = -> Sketch104
  ReferenceAxis = -> Sketch104 [V_Axis]
  Suppressed = false
  Type = 0
FEATURE [PartDesign::Fillet] Fillet048
  Base = -> Groove047 [Edge1]
  BaseFeature = -> Groove047
  Radius = 6
  SupportTransform = false
  Suppressed = false
  UseAllEdges = false
FEATURE [Sketcher::SketchObject] Sketch105
  ArcFitTolerance = 0
  AttachmentSupport = -> [XY_Plane033]
  FullyConstrained = true
  MakeInternals = false
  MapMode = 5
  sketch-geometry (2):
    g0: LineSegment StartX=-6.4e-15 StartY=-368 StartZ=0 EndX=-6.4e-15 EndY=-438 EndZ=0
    g1: ArcOfCircle CenterX=0 CenterY=-403 CenterZ=0 NormalX=0 NormalY=0 NormalZ=1 AngleXU=0 Radius=35 StartAngle=4.71239 EndAngle=7.85398
  constraints (7):
    c: Vertical(g0)
    c: PointOnObject(g1,g0)
    c: Coincident(g1,g0)
    c: Coincident(g1,g0)
    c: PointOnObject(g1,g-2)
    c: DistanceY(g1,g-1) = 403
    c: Radius(g1) = 35
FEATURE [PartDesign::Groove] Groove048  label="R Knee cut"
  Angle = 360
  Angle2 = 60
  Axis = (0,1,0)
  Base = (0,0,0)
  BaseFeature = -> Fillet048
  Profile = -> Sketch105
  ReferenceAxis = -> Sketch105 [V_Axis]
  Suppressed = false
  Type = 0
FEATURE [PartDesign::Fillet] Fillet049
  Base = -> Groove048 [Edge1]
  BaseFeature = -> Groove048
  Radius = 3
  SupportTransform = false
  Suppressed = false
  UseAllEdges = false
FEATURE [PartDesign::Revolution] Revolution055  label="R Knee"
  Angle = 360
  Angle2 = 60
  Axis = (0,1,0)
  Base = (0,0,0)
  BaseFeature = -> Fillet049
  Profile = -> Sketch105
  ReferenceAxis = -> Sketch105 [V_Axis]
  Reversed = true
  Suppressed = false
  Type = 0
FEATURE [PartDesign::Body] Body031  label="Right Thigh"
  AllowCompound = false
  Group = -> [Sketch103,Revolution054,Sketch104,Groove047,Fillet048,Sketch105,Groove048,Fillet049,Revolution055,Local_CS051,Local_CS052]
  Origin = -> Origin033
  Placement = pos=(-75,900,0) rot=(0,0,1;0rad)
  Tip = -> Revolution055
FEATURE [Sketcher::SketchObject] Sketch106
  ArcFitTolerance = 0
  AttachmentSupport = -> [XY_Plane034]
  FullyConstrained = true
  MakeInternals = false
  MapMode = 5
  sketch-geometry (14):
    g0: LineSegment StartX=0 StartY=0 StartZ=0 EndX=0 EndY=-428.766 EndZ=0
    g1-g7: Circle [constr] x7 (B-spline internal-alignment scaffolding for g8; pole/knot coordinates omitted)
    g8: BSplineCurve PolesCount=7 KnotsCount=5 Degree=3 IsPeriodic=0
    g9-g13: GeomPoint [constr] x5 (B-spline internal-alignment scaffolding for g8; pole/knot coordinates omitted)
  constraints (9):
    c: Vertical(g0)
    c: PointOnObject(g0,g-2)
    c: Weight(g1) = 1
    c: Coincident(g8,g0)
    c: Equal(g1, g2-g7) x6
    c: Coincident(g8,g0)
    c: InternalAlignment(g1-g7 -> g8) x7
    c: InternalAlignment(g9-g13 -> g8) x5
    c: Block(g8)
FEATURE [PartDesign::Revolution] Revolution056  label="R Shin main body"
  Angle = 360
  Angle2 = 60
  Axis = (0,1,0)
  Base = (0,0,0)
  Profile = -> Sketch106
  ReferenceAxis = -> Sketch106 [V_Axis]
  Reversed = true
  Suppressed = false
  Type = 0
FEATURE [PartDesign::CoordinateSystem] Local_CS053  label="Right Shin/Knee"
  AttacherType = Attacher::AttachEngine3D
  AttachmentSupport = -> [Revolution056]
  MapMode = 2
FEATURE [PartDesign::CoordinateSystem] Local_CS054  label="Right Shin/Ankle"
  AttacherType = Attacher::AttachEngine3D
  AttachmentOffset = pos=(0,-435,0) rot=(0,0,1;0rad)
  AttachmentSupport = -> [Revolution056]
  MapMode = 2
  Placement = pos=(0,-435,0) rot=(0,0,1;0rad)
FEATURE [Sketcher::SketchObject] Sketch107
  ArcFitTolerance = 0
  AttachmentSupport = -> [XY_Plane034]
  FullyConstrained = true
  MakeInternals = false
  MapMode = 5
  sketch-geometry (2):
    g0: LineSegment StartX=-6.4e-15 StartY=35 StartZ=0 EndX=-6.4e-15 EndY=-35 EndZ=0
    g1: ArcOfCircle CenterX=0 CenterY=0 CenterZ=0 NormalX=0 NormalY=0 NormalZ=1 AngleXU=0 Radius=35 StartAngle=4.71239 EndAngle=7.85398
  constraints (6):
    c: PointOnObject(g1,g0)
    c: Coincident(g1,g0)
    c: Coincident(g1,g0)
    c: Vertical(g0)
    c: Coincident(g1,g-1)
    c: Radius(g1) = 35
FEATURE [PartDesign::Groove] Groove049  label="R knee cut"
  Angle = 360
  Angle2 = 60
  Axis = (0,1,0)
  Base = (0,0,0)
  BaseFeature = -> Revolution056
  Profile = -> Sketch107
  ReferenceAxis = -> Sketch107 [V_Axis]
  Suppressed = false
  Type = 0
FEATURE [PartDesign::Fillet] Fillet050
  Base = -> Groove049 [Edge1]
  BaseFeature = -> Groove049
  Radius = 3
  SupportTransform = false
  Suppressed = false
  UseAllEdges = false
FEATURE [Sketcher::SketchObject] Sketch108
  ArcFitTolerance = 0
  AttachmentSupport = -> [XY_Plane034]
  FullyConstrained = true
  MakeInternals = false
  MapMode = 5
  sketch-geometry (2):
    g0: LineSegment StartX=-4.6e-15 StartY=-410 StartZ=0 EndX=-4.6e-15 EndY=-460 EndZ=0
    g1: ArcOfCircle CenterX=0 CenterY=-435 CenterZ=0 NormalX=0 NormalY=0 NormalZ=1 AngleXU=0 Radius=25 StartAngle=4.71239 EndAngle=7.85398
  constraints (7):
    c: Vertical(g0)
    c: PointOnObject(g1,g0)
    c: Coincident(g1,g0)
    c: Coincident(g1,g0)
    c: PointOnObject(g1,g-2)
    c: DistanceY(g1,g-1) = 435
    c: Radius(g1) = 25
FEATURE [PartDesign::Groove] Groove050  label="R Ankle cut"
  Angle = 360
  Angle2 = 60
  Axis = (0,1,0)
  Base = (0,0,0)
  BaseFeature = -> Fillet050
  Profile = -> Sketch108
  ReferenceAxis = -> Sketch108 [V_Axis]
  Suppressed = false
  Type = 0
FEATURE [PartDesign::Fillet] Fillet051
  Base = -> Groove050 [Edge3]
  BaseFeature = -> Groove050
  Radius = 3
  SupportTransform = false
  Suppressed = false
  UseAllEdges = false
FEATURE [PartDesign::Revolution] Revolution057  label="R Ankle"
  Angle = 360
  Angle2 = 60
  Axis = (0,1,0)
  Base = (0,0,0)
  BaseFeature = -> Fillet051
  Profile = -> Sketch108
  ReferenceAxis = -> Sketch108 [V_Axis]
  Reversed = true
  Suppressed = false
  Type = 0
FEATURE [PartDesign::Body] Body032  label="Right Shin"
  AllowCompound = false
  Group = -> [Sketch106,Revolution056,Sketch107,Groove049,Fillet050,Sketch108,Groove050,Fillet051,Revolution057,Local_CS053,Local_CS054]
  Origin = -> Origin034
  Placement = pos=(-75,497,0) rot=(0,0,1;0rad)
  Tip = -> Revolution057
FEATURE [Sketcher::SketchObject] Sketch109
  ArcFitTolerance = 0
  AttachmentSupport = -> [YZ_Plane035]
  FullyConstrained = true
  MakeInternals = false
  MapMode = 5
  Placement = pos=(0,0,0) rot=(0.57735,0.57735,0.57735;2.0944rad)
  sketch-geometry (18):
    g0: LineSegment StartX=-62 StartY=180 StartZ=0 EndX=-62 EndY=-40 EndZ=0
    g1-g9: Circle [constr] x9 (B-spline internal-alignment scaffolding for g10; pole/knot coordinates omitted)
    g10: BSplineCurve PolesCount=9 KnotsCount=7 Degree=3 IsPeriodic=0
    g11-g17: GeomPoint [constr] x7 (B-spline internal-alignment scaffolding for g10; pole/knot coordinates omitted)
  constraints (13):
    c: Vertical(g0)
    c: DistanceX(g0,g-1) = 62
    c: DistanceY(g0,g-1) = 40
    c: DistanceY(g0,g0) = 220
    c: Weight(g1) = 1
    c: Coincident(g10,g0)
    c: Equal(g1, g2-g9) x8
    c: Coincident(g10,g0)
    c: InternalAlignment(g1-g9 -> g10) x9
    c: InternalAlignment(g11-g17 -> g10) x7
    c: Horizontal(g0,g8)
    c: Horizontal(g0,g2)
    c: Block(g10)
FEATURE [PartDesign::Pad] Pad003  label="R foot main body"
  Direction = (1,0,0)
  Length = 100
  Length2 = 10
  Midplane = true
  Placement = pos=(0,0,0) rot=(1,1,1;2.0944rad)
  Profile = -> Sketch109
  ReferenceAxis = -> Sketch109 [N_Axis]
  Suppressed = false
  Type = 0
FEATURE [PartDesign::Fillet] Fillet052
  Base = -> Pad003 [Edge4,Edge6,Edge1,Edge5,Edge2]
  BaseFeature = -> Pad003
  Placement = pos=(0,0,0) rot=(1,1,1;2.0944rad)
  Radius = 6
  SupportTransform = false
  Suppressed = false
  UseAllEdges = false
FEATURE [PartDesign::CoordinateSystem] Local_CS055  label="Right Foot/Ankle"
  AttacherType = Attacher::AttachEngine3D
  AttachmentSupport = -> [Pad003]
  MapMode = 2
  Placement = pos=(0,0,0) rot=(0.57735,0.57735,0.57735;2.0944rad)
FEATURE [Sketcher::SketchObject] Sketch110
  ArcFitTolerance = 0
  AttachmentSupport = -> [XY_Plane035]
  FullyConstrained = true
  MakeInternals = false
  MapMode = 5
  sketch-geometry (2):
    g0: LineSegment StartX=7.7e-15 StartY=25 StartZ=0 EndX=7.7e-15 EndY=-25 EndZ=0
    g1: ArcOfCircle CenterX=0 CenterY=0 CenterZ=0 NormalX=0 NormalY=0 NormalZ=1 AngleXU=0 Radius=25 StartAngle=4.71239 EndAngle=7.85398
  constraints (6):
    c: Vertical(g0)
    c: PointOnObject(g1,g0)
    c: Coincident(g1,g0)
    c: Coincident(g1,g0)
    c: Coincident(g1,g-1)
    c: Radius(g1) = 25
FEATURE [PartDesign::Groove] Groove051  label="Ankle cut003"
  Angle = 360
  Angle2 = 60
  Axis = (0,1,0)
  Base = (0,0,0)
  BaseFeature = -> Fillet052
  Placement = pos=(0,0,0) rot=(1,1,1;2.0944rad)
  Profile = -> Sketch110
  ReferenceAxis = -> Sketch110 [V_Axis]
  Suppressed = false
  Type = 0
FEATURE [PartDesign::Fillet] Fillet053
  Base = -> Groove051 [Edge20,Edge19]
  BaseFeature = -> Groove051
  Placement = pos=(0,0,0) rot=(1,1,1;2.0944rad)
  Radius = 3
  SupportTransform = false
  Suppressed = false
  UseAllEdges = false
FEATURE [PartDesign::Body] Body033  label="Right foot"
  AllowCompound = false
  Group = -> [Sketch109,Pad003,Fillet052,Sketch110,Groove051,Fillet053,Local_CS055]
  Origin = -> Origin035
  Placement = pos=(-75,62,0) rot=(0,0,1;0rad)
  Tip = -> Fillet053
FEATURE [App::Part] Part_2  label="Mannequin_mp-dummy-1850m-standing-000"
  Group = -> [LCS_0,Body019,Body020,Body021,Body022,Body023,Body024,Body025,Body026,Body027,Body028,Body029,Body030,Body031,Body032,Body033]
  Origin = -> Origin020
  Placement = pos=(-1246.5,11619,-2.5799e-12) rot=(0,-0.707107,-0.707107;3.14159rad)
FEATURE [PartDesign::CoordinateSystem] LCS_001
  AttacherType = Attacher::AttachEngine3D
  AttachmentSupport = -> [X_Axis036]
  MapMode = 2
FEATURE [Sketcher::SketchObject] Sketch111
  ArcFitTolerance = 0
  AttachmentSupport = -> [XY_Plane037]
  FullyConstrained = true
  MakeInternals = false
  MapMode = 5
  sketch-geometry (14):
    g0: LineSegment StartX=0 StartY=0 StartZ=0 EndX=0 EndY=296.299 EndZ=0
    g1-g7: Circle [constr] x7 (B-spline internal-alignment scaffolding for g8; pole/knot coordinates omitted)
    g8: BSplineCurve PolesCount=7 KnotsCount=5 Degree=3 IsPeriodic=0
    g9-g13: GeomPoint [constr] x5 (B-spline internal-alignment scaffolding for g8; pole/knot coordinates omitted)
  constraints (12):
    c: Coincident(g0,g-1)
    c: Vertical(g0)
    c: Weight(g1) = 1
    c: Coincident(g8,g0)
    c: Equal(g1, g2-g7) x6
    c: Coincident(g8,g0)
    c: InternalAlignment(g1-g7 -> g8) x7
    c: InternalAlignment(g9-g13 -> g8) x5
    c: Horizontal(g0,g2)
    c: Horizontal(g0,g6)
    c: Block(g0)
    c: Block(g8)
FEATURE [PartDesign::Revolution] Revolution058
  Angle = 360
  Angle2 = 60
  Axis = (0,1,0)
  Base = (0,0,0)
  Profile = -> Sketch111
  ReferenceAxis = -> Sketch111 [V_Axis]
  Reversed = true
  Suppressed = false
  Type = 0
FEATURE [PartDesign::CoordinateSystem] Local_CS061  label="Head/Neck LCS001"
  AttacherType = Attacher::AttachEngine3D
  AttachmentSupport = -> [Revolution058]
  MapMode = 2
FEATURE [Sketcher::SketchObject] Sketch112
  ArcFitTolerance = 0
  AttachmentSupport = -> [XY_Plane038]
  FullyConstrained = true
  MakeInternals = false
  MapMode = 5
  sketch-geometry (18):
    g0: LineSegment StartX=0 StartY=322.019 StartZ=0 EndX=0 EndY=20.3719 EndZ=0
    g1-g9: Circle [constr] x9 (B-spline internal-alignment scaffolding for g10; pole/knot coordinates omitted)
    g10: BSplineCurve PolesCount=9 KnotsCount=7 Degree=3 IsPeriodic=0
    g11-g17: GeomPoint [constr] x7 (B-spline internal-alignment scaffolding for g10; pole/knot coordinates omitted)
  constraints (12):
    c: Vertical(g0)
    c: PointOnObject(g0,g-2)
    c: Weight(g1) = 1
    c: Coincident(g10,g0)
    c: Equal(g1, g2-g9) x8
    c: Coincident(g10,g0)
    c: InternalAlignment(g1-g9 -> g10) x9
    c: InternalAlignment(g11-g17 -> g10) x7
    c: Horizontal(g0,g2)
    c: Horizontal(g0,g8)
    c: Block(g0)
    c: Block(g10)
FEATURE [PartDesign::Revolution] Revolution059  label="Base shape001"
  Angle = 360
  Angle2 = 60
  Axis = (0,1,0)
  Base = (0,0,0)
  Profile = -> Sketch112
  ReferenceAxis = -> Sketch112 [V_Axis]
  Reversed = true
  Suppressed = false
  Type = 0
FEATURE [PartDesign::CoordinateSystem] Local_CS056  label="Chest/Neck LCS001"
  AttacherType = Attacher::AttachEngine3D
  AttachmentOffset = pos=(354,0,0) rot=(0,0,1;0rad)
  AttachmentSupport = -> [Revolution059]
  MapMode = 4
  Placement = pos=(0,354,0) rot=(0.57735,0.57735,0.57735;2.0944rad)
FEATURE [PartDesign::CoordinateSystem] Local_CS057  label="Chest/Waist LCS001"
  AttacherType = Attacher::AttachEngine3D
  AttachmentSupport = -> [Revolution059]
  MapMode = 2
FEATURE [PartDesign::CoordinateSystem] Local_CS058  label="Chest/Left shoulder LCS001"
  AttacherType = Attacher::AttachEngine3D
  AttachmentOffset = pos=(184,257,0) rot=(0,0,1;0rad)
  AttachmentSupport = -> [Revolution059]
  MapMode = 2
  Placement = pos=(184,257,0) rot=(0,0,1;0rad)
FEATURE [PartDesign::CoordinateSystem] Local_CS059  label="Chest/Right shoulder LCS001"
  AttacherType = Attacher::AttachEngine3D
  AttachmentOffset = pos=(-184,257,0) rot=(0,0,1;0rad)
  AttachmentSupport = -> [Revolution059]
  MapMode = 2
  Placement = pos=(-184,257,0) rot=(0,0,1;0rad)
FEATURE [Sketcher::SketchObject] Sketch113
  ArcFitTolerance = 0
  AttachmentSupport = -> [XY_Plane037]
  FullyConstrained = true
  MakeInternals = false
  MapMode = 5
  sketch-geometry (2):
    g0: LineSegment StartX=-1.01e-14 StartY=55 StartZ=0 EndX=-1.01e-14 EndY=-55 EndZ=0
    g1: ArcOfCircle CenterX=0 CenterY=0 CenterZ=0 NormalX=0 NormalY=0 NormalZ=1 AngleXU=0 Radius=55 StartAngle=4.71239 EndAngle=7.85398
  constraints (6):
    c: Vertical(g0)
    c: Coincident(g1,g-1)
    c: Coincident(g1,g0)
    c: Coincident(g1,g0)
    c: PointOnObject(g0,g-2)
    c: Radius(g1) = 55
FEATURE [PartDesign::Groove] Groove052
  Angle = 360
  Angle2 = 60
  Axis = (0,1,0)
  Base = (0,0,0)
  BaseFeature = -> Revolution058
  Profile = -> Sketch113
  ReferenceAxis = -> Sketch113 [V_Axis]
  Suppressed = false
  Type = 0
FEATURE [Sketcher::SketchObject] Sketch114
  ArcFitTolerance = 0
  AttachmentSupport = -> [XZ_Plane037]
  FullyConstrained = true
  MakeInternals = false
  MapMode = 5
  Placement = pos=(0,0,0) rot=(1,0,0;1.5708rad)
  sketch-geometry (5):
    g0: LineSegment StartX=-125 StartY=125 StartZ=0 EndX=125 EndY=125 EndZ=0
    g1: LineSegment StartX=125 StartY=125 StartZ=0 EndX=125 EndY=50 EndZ=0
    g2: LineSegment StartX=125 StartY=50 StartZ=0 EndX=0 EndY=75 EndZ=0
    g3: LineSegment StartX=0 StartY=75 StartZ=0 EndX=-125 EndY=50 EndZ=0
    g4: LineSegment StartX=-125 StartY=50 StartZ=0 EndX=-125 EndY=125 EndZ=0
  constraints (15):
    c: Horizontal(g0)
    c: Coincident(g0,g1)
    c: Vertical(g1)
    c: Coincident(g1,g2)
    c: Coincident(g2,g3)
    c: Coincident(g3,g4)
    c: Coincident(g4,g0)
    c: Vertical(g4)
    c: Horizontal(g3,g1)
    c: PointOnObject(g2,g-2)
    c: DistanceX(g0,g0) = 250
    c: DistanceX(g0,g-1) = 125
    c: DistanceY(g4,g4) = 75
    c: DistanceY(g-1,g2) = 75
    c: DistanceY(g-1,g0) = 125
FEATURE [PartDesign::Pocket] Pocket018
  BaseFeature = -> Groove052
  Direction = (0,1,0.05)
  Length = 300
  Length2 = 5
  Profile = -> Sketch114
  ReferenceAxis = -> Sketch114 [N_Axis]
  Suppressed = false
  Type = 0
  UseCustomVector = true
FEATURE [PartDesign::Fillet] Fillet054
  Base = -> Pocket018 [Edge3]
  BaseFeature = -> Pocket018
  Radius = 3
  SupportTransform = false
  Suppressed = false
  UseAllEdges = false
FEATURE [PartDesign::Body] Body034  label="Head001"
  AllowCompound = false
  Group = -> [Sketch111,Revolution058,Sketch113,Groove052,Sketch114,Pocket018,Fillet054,Local_CS061]
  Origin = -> Origin037
  Placement = pos=(-2.274e-13,1550.8,12.7426) rot=(-1,0,0;0.663225rad)
  Tip = -> Fillet054
FEATURE [Sketcher::SketchObject] Sketch115
  ArcFitTolerance = 0
  AttachmentSupport = -> [YZ_Plane038]
  FullyConstrained = true
  MakeInternals = false
  MapMode = 5
  Placement = pos=(0,0,0) rot=(0.57735,0.57735,0.57735;2.0944rad)
  sketch-geometry (6):
    g0: LineSegment StartX=0 StartY=76.0576 StartZ=0 EndX=164.705 EndY=107.04 EndZ=0
    g1: LineSegment StartX=230.198 StartY=103.732 StartZ=0 EndX=327.121 EndY=75.1407 EndZ=0
    g2: LineSegment StartX=327.121 StartY=75.1407 StartZ=0 EndX=327.121 EndY=181.805 EndZ=0
    g3: LineSegment StartX=327.121 StartY=181.805 StartZ=0 EndX=0 EndY=181.805 EndZ=0
    g4: LineSegment StartX=0 StartY=181.805 StartZ=0 EndX=0 EndY=76.0576 EndZ=0
    g5: ArcOfCircle CenterX=190.587 CenterY=-30.5467 CenterZ=0 NormalX=0 NormalY=0 NormalZ=1 AngleXU=0 Radius=140 StartAngle=1.28394 EndAngle=1.75673
  constraints (14):
    c: Coincident(g1,g2)
    c: Vertical(g2)
    c: Coincident(g2,g3)
    c: Horizontal(g3)
    c: Coincident(g3,g4)
    c: Coincident(g4,g0)
    c: Vertical(g4)
    c: PointOnObject(g3,g-2)
    c: Tangent(g1,g5) = 1.5708
    c: Tangent(g0,g5) = 1.5708
    c: Radius(g5) = 140
    c: Block(g0)
    c: Block(g1)
    c: Block(g3)
FEATURE [PartDesign::Pocket] Pocket019  label="Front cut001"
  BaseFeature = -> Revolution059
  Direction = (-1,0,0)
  Length = 5
  Length2 = 5
  Midplane = true
  Profile = -> Sketch115
  ReferenceAxis = -> Sketch115 [N_Axis]
  Suppressed = false
  Type = 1
FEATURE [Sketcher::SketchObject] Sketch116
  ArcFitTolerance = 0
  AttachmentSupport = -> [YZ_Plane038]
  FullyConstrained = true
  MakeInternals = false
  MapMode = 5
  Placement = pos=(0,0,0) rot=(0.57735,0.57735,0.57735;2.0944rad)
  sketch-geometry (8):
    g0: LineSegment StartX=0 StartY=-87.996 StartZ=0 EndX=81.1566 EndY=-77.888 EndZ=0
    g1: LineSegment StartX=139.259 StartY=-78.9913 StartZ=0 EndX=245.223 EndY=-96.2967 EndZ=0
    g2: LineSegment StartX=281.434 StartY=-93.8397 StartZ=0 EndX=341.01 EndY=-75.582 EndZ=0
    g3: LineSegment StartX=341.01 StartY=-75.582 StartZ=0 EndX=341.01 EndY=-197.004 EndZ=0
    g4: LineSegment StartX=341.01 StartY=-197.004 StartZ=0 EndX=0 EndY=-197.004 EndZ=0
    g5: LineSegment StartX=0 StartY=-197.004 StartZ=0 EndX=0 EndY=-87.996 EndZ=0
    g6: ArcOfCircle CenterX=106.373 CenterY=-280.353 CenterZ=0 NormalX=0 NormalY=0 NormalZ=1 AngleXU=0 Radius=204.029 StartAngle=1.40891 EndAngle=1.69471
    g7: ArcOfCircle CenterX=258.073 CenterY=-17.6116 CenterZ=0 NormalX=0 NormalY=0 NormalZ=1 AngleXU=0 Radius=79.7275 StartAngle=4.5505 EndAngle=5.00977
  constraints (16):
    c: Coincident(g2,g3)
    c: Coincident(g3,g4)
    c: Horizontal(g4)
    c: Coincident(g4,g5)
    c: Coincident(g5,g0)
    c: Vertical(g5)
    c: Vertical(g3)
    c: PointOnObject(g4,g-2)
    c: Tangent(g1,g6) = 1.5708
    c: Tangent(g0,g6) = 1.5708
    c: Tangent(g1,g7) = -1.5708
    c: Tangent(g2,g7) = -1.5708
    c: Block(g0)
    c: Block(g2)
    c: Block(g1)
    c: Block(g4)
FEATURE [PartDesign::Pocket] Pocket020  label="Back cut001"
  BaseFeature = -> Pocket019
  Direction = (-1,0,0)
  Length = 5
  Length2 = 5
  Midplane = true
  Profile = -> Sketch116
  ReferenceAxis = -> Sketch116 [N_Axis]
  Suppressed = false
  Type = 1
FEATURE [Sketcher::SketchObject] Sketch117
  ArcFitTolerance = 0
  AttachmentSupport = -> [XY_Plane038]
  FullyConstrained = true
  MakeInternals = false
  MapMode = 5
  sketch-geometry (2):
    g0: LineSegment StartX=1.68e-14 StartY=409 StartZ=0 EndX=1.68e-14 EndY=299 EndZ=0
    g1: ArcOfCircle CenterX=0 CenterY=354 CenterZ=0 NormalX=0 NormalY=0 NormalZ=1 AngleXU=0 Radius=55 StartAngle=4.71239 EndAngle=7.85398
  constraints (7):
    c: Vertical(g0)
    c: PointOnObject(g1,g0)
    c: Coincident(g1,g0)
    c: PointOnObject(g1,g-2)
    c: Coincident(g1,g0)
    c: Radius(g1) = 55
    c: DistanceY(g-1,g1) = 354
FEATURE [PartDesign::Groove] Groove053  label="Neck cut001"
  Angle = 360
  Angle2 = 60
  Axis = (0,1,0)
  Base = (0,0,0)
  BaseFeature = -> Pocket020
  Profile = -> Sketch117
  ReferenceAxis = -> Sketch117 [V_Axis]
  Suppressed = false
  Type = 0
FEATURE [PartDesign::Fillet] Fillet055  label="Neck fillet001"
  Base = -> Groove053 [Edge1]
  BaseFeature = -> Groove053
  Radius = 6
  SupportTransform = false
  Suppressed = false
  UseAllEdges = false
FEATURE [Sketcher::SketchObject] Sketch118
  ArcFitTolerance = 0
  AttachmentSupport = -> [XY_Plane038]
  FullyConstrained = true
  MakeInternals = false
  MapMode = 5
  sketch-geometry (2):
    g0: LineSegment StartX=2.3e-14 StartY=75 StartZ=0 EndX=2.3e-14 EndY=-75 EndZ=0
    g1: ArcOfCircle CenterX=0 CenterY=0 CenterZ=0 NormalX=0 NormalY=0 NormalZ=1 AngleXU=0 Radius=75 StartAngle=4.71239 EndAngle=7.85398
  constraints (6):
    c: Vertical(g0)
    c: Coincident(g1,g-1)
    c: Coincident(g1,g0)
    c: Coincident(g1,g0)
    c: PointOnObject(g0,g-2)
    c: Radius(g1) = 75
FEATURE [PartDesign::Groove] Groove054  label="Waist cut001"
  Angle = 360
  Angle2 = 60
  Axis = (0,1,0)
  Base = (0,0,0)
  BaseFeature = -> Fillet055
  Profile = -> Sketch118
  ReferenceAxis = -> Sketch118 [V_Axis]
  Suppressed = false
  Type = 0
FEATURE [PartDesign::Fillet] Fillet056  label="Waist fillet001"
  Base = -> Groove054 [Edge3]
  BaseFeature = -> Groove054
  Radius = 5
  SupportTransform = false
  Suppressed = false
  UseAllEdges = false
FEATURE [Sketcher::SketchObject] Sketch119
  ArcFitTolerance = 0
  AttachmentSupport = -> [XY_Plane038]
  FullyConstrained = true
  MakeInternals = false
  MapMode = 5
  sketch-geometry (4):
    g0: LineSegment StartX=124 StartY=257 StartZ=0 EndX=244 EndY=257 EndZ=0
    g1: ArcOfCircle CenterX=184 CenterY=257 CenterZ=0 NormalX=0 NormalY=0 NormalZ=1 AngleXU=0 Radius=60 StartAngle=0 EndAngle=3.14159
    g2: LineSegment StartX=-244 StartY=257 StartZ=0 EndX=-124 EndY=257 EndZ=0
    g3: ArcOfCircle CenterX=-184 CenterY=257 CenterZ=0 NormalX=0 NormalY=0 NormalZ=1 AngleXU=0 Radius=60 StartAngle=4e-16 EndAngle=3.14159
  constraints (14):
    c: Horizontal(g0)
    c: PointOnObject(g1,g0)
    c: Coincident(g1,g0)
    c: Coincident(g1,g0)
    c: DistanceY(g-1,g1) = 257
    c: Radius(g1) = 60
    c: DistanceX(g-1,g1) = 184
    c: Horizontal(g2)
    c: PointOnObject(g3,g2)
    c: Coincident(g3,g2)
    c: Coincident(g3,g2)
    c: Horizontal(g2,g0)
    c: Radius(g3) = 60
    c: DistanceX(g3,g-1) = 184
FEATURE [PartDesign::Groove] Groove055  label="Shoulders cut001"
  Angle = 360
  Angle2 = 60
  Axis = (1,0,0)
  Base = (124,257,0)
  BaseFeature = -> Fillet056
  Profile = -> Sketch119
  ReferenceAxis = -> Sketch119 [Edge1]
  Suppressed = false
  Type = 0
FEATURE [PartDesign::Fillet] Fillet057  label="Shoulders fillet001"
  Base = -> Groove055 [Edge6,Edge3,Edge12,Edge13]
  BaseFeature = -> Groove055
  Radius = 6
  SupportTransform = false
  Suppressed = false
  UseAllEdges = false
FEATURE [PartDesign::Revolution] Revolution060  label="Neck add001"
  Angle = 360
  Angle2 = 60
  Axis = (0,1,0)
  Base = (0,0,0)
  BaseFeature = -> Fillet057
  Profile = -> Sketch117
  ReferenceAxis = -> Sketch117 [V_Axis]
  Reversed = true
  Suppressed = false
  Type = 0
FEATURE [PartDesign::Revolution] Revolution061  label="waist add001"
  Angle = 360
  Angle2 = 60
  Axis = (0,1,0)
  Base = (0,0,0)
  BaseFeature = -> Revolution060
  Profile = -> Sketch118
  ReferenceAxis = -> Sketch118 [V_Axis]
  Reversed = true
  Suppressed = false
  Type = 0
FEATURE [PartDesign::Revolution] Revolution062  label="Shoulders001"
  Angle = 360
  Angle2 = 60
  Axis = (1,0,0)
  Base = (-244,257,0)
  BaseFeature = -> Revolution061
  Profile = -> Sketch119
  ReferenceAxis = -> Sketch119 [Edge3]
  Suppressed = false
  Type = 0
FEATURE [PartDesign::Body] Body035  label="Chest001"
  AllowCompound = false
  Group = -> [Sketch112,Revolution059,Sketch115,Pocket019,Sketch116,Pocket020,Sketch117,Groove053,Fillet055,Sketch118,Groove054,Fillet056,Sketch119,Groove055,Fillet057,Revolution060,Revolution061,Revolution062,Local_CS056,Local_CS057,Local_CS058,Local_CS059]
  Origin = -> Origin038
  Placement = pos=(-2.274e-13,1197.02,0.388141) rot=(1,0,0;0.034907rad)
  Tip = -> Revolution062
FEATURE [Sketcher::SketchObject] Sketch120
  ArcFitTolerance = 0
  AttachmentSupport = -> [XY_Plane039]
  FullyConstrained = true
  MakeInternals = false
  MapMode = 5
  sketch-geometry (21):
    g0: LineSegment StartX=0 StartY=-29.4305 StartZ=0 EndX=0 EndY=-256.068 EndZ=0
    g1-g7: Circle [constr] x7 (B-spline internal-alignment scaffolding for g8; pole/knot coordinates omitted)
    g8: BSplineCurve PolesCount=7 KnotsCount=5 Degree=3 IsPeriodic=0
    g9-g13: GeomPoint [constr] x5 (B-spline internal-alignment scaffolding for g8; pole/knot coordinates omitted)
    g14-g17: Circle [constr] x4 (B-spline internal-alignment scaffolding for g18; pole/knot coordinates omitted)
    g18: BSplineCurve PolesCount=4 KnotsCount=2 Degree=3 IsPeriodic=0
    g19: GeomPoint [constr] X=118.087 Y=-247.149 Z=0
    g20: GeomPoint [constr] X=0 Y=-256.068 Z=0
  constraints (21):
    c: PointOnObject(g0,g-2)
    c: Vertical(g0)
    c: Weight(g1) = 1
    c: Coincident(g8,g0)
    c: Equal(g1, g2-g7) x6
    c: InternalAlignment(g1-g7 -> g8) x7
    c: InternalAlignment(g9-g13 -> g8) x5
    c: Weight(g14) = 1
    c: Coincident(g18,g8)
    c: Equal(g14,g15)
    c: Equal(g14,g16)
    c: Equal(g14,g17)
    c: Coincident(g18,g0)
    c: InternalAlignment(g14-g17 -> g18) x4
    c: InternalAlignment(g19,g18)
    c: InternalAlignment(g20,g18)
    c: Horizontal(g16,g0)
    c: Horizontal(g0,g2)
    c: Block(g0)
    c: Block(g8)
    c: Block(g18)
FEATURE [PartDesign::Revolution] Revolution063  label="Main body of hip001"
  Angle = 360
  Angle2 = 60
  Axis = (0,1,0)
  Base = (0,0,0)
  Profile = -> Sketch120
  ReferenceAxis = -> Sketch120 [V_Axis]
  Reversed = true
  Suppressed = false
  Type = 0
FEATURE [PartDesign::CoordinateSystem] Local_CS060  label="Hip/Waist LCS001"
  AttacherType = Attacher::AttachEngine3D
  AttachmentSupport = -> [Revolution063]
  MapMode = 2
FEATURE [PartDesign::CoordinateSystem] Local_CS062  label="Hip/Leg joint left001"
  AttacherType = Attacher::AttachEngine3D
  AttachmentOffset = pos=(75,-298,0) rot=(0,0,1;0rad)
  AttachmentSupport = -> [Revolution063]
  MapMode = 2
  Placement = pos=(75,-298,0) rot=(0,0,1;0rad)
FEATURE [PartDesign::CoordinateSystem] Local_CS063  label="Hip/Leg joint right001"
  AttacherType = Attacher::AttachEngine3D
  AttachmentOffset = pos=(-75,-298,0) rot=(0,0,1;0rad)
  AttachmentSupport = -> [Revolution063]
  MapMode = 2
  Placement = pos=(-75,-298,0) rot=(0,0,1;0rad)
FEATURE [Sketcher::SketchObject] Sketch121
  ArcFitTolerance = 0
  AttachmentSupport = -> [XY_Plane039]
  FullyConstrained = true
  MakeInternals = false
  MapMode = 5
  sketch-geometry (2):
    g0: LineSegment StartX=2.3e-14 StartY=75 StartZ=0 EndX=2.3e-14 EndY=-75 EndZ=0
    g1: ArcOfCircle CenterX=0 CenterY=0 CenterZ=0 NormalX=0 NormalY=0 NormalZ=1 AngleXU=0 Radius=75 StartAngle=4.71239 EndAngle=7.85398
  constraints (6):
    c: Vertical(g0)
    c: PointOnObject(g1,g0)
    c: Coincident(g1,g0)
    c: Coincident(g1,g0)
    c: Coincident(g1,g-1)
    c: Radius(g1) = 75
FEATURE [PartDesign::Groove] Groove056  label="Waist cut of hip001"
  Angle = 360
  Angle2 = 60
  Axis = (0,1,0)
  Base = (0,0,0)
  BaseFeature = -> Revolution063
  Profile = -> Sketch121
  ReferenceAxis = -> Sketch121 [V_Axis]
  Suppressed = false
  Type = 0
FEATURE [PartDesign::Fillet] Fillet058  label="waist001"
  Base = -> Groove056 [Edge4]
  BaseFeature = -> Groove056
  Radius = 6
  SupportTransform = false
  Suppressed = false
  UseAllEdges = false
FEATURE [Sketcher::SketchObject] Sketch122
  ArcFitTolerance = 0
  AttachmentSupport = -> [XY_Plane039]
  FullyConstrained = true
  MakeInternals = false
  MapMode = 5
  sketch-geometry (4):
    g0: LineSegment StartX=15 StartY=-298 StartZ=0 EndX=135 EndY=-298 EndZ=0
    g1: ArcOfCircle CenterX=75 CenterY=-298 CenterZ=0 NormalX=0 NormalY=0 NormalZ=1 AngleXU=0 Radius=60 StartAngle=0 EndAngle=3.14159
    g2: LineSegment StartX=-135 StartY=-298 StartZ=0 EndX=-15 EndY=-298 EndZ=0
    g3: ArcOfCircle CenterX=-75 CenterY=-298 CenterZ=0 NormalX=0 NormalY=0 NormalZ=1 AngleXU=0 Radius=60 StartAngle=3e-16 EndAngle=3.14159
  constraints (14):
    c: PointOnObject(g1,g0)
    c: Coincident(g1,g0)
    c: Coincident(g1,g0)
    c: Horizontal(g0)
    c: DistanceX(g-1,g1) = 75
    c: DistanceY(g1,g-1) = 298
    c: Radius(g1) = 60
    c: Horizontal(g2)
    c: PointOnObject(g3,g2)
    c: Coincident(g3,g2)
    c: Coincident(g3,g2)
    c: Horizontal(g2,g0)
    c: Equal(g3,g1)
    c: DistanceX(g3,g-1) = 75
FEATURE [PartDesign::Groove] Groove057  label="Hip joints cuts001"
  Angle = 360
  Angle2 = 60
  Axis = (1,0,0)
  Base = (15,-298,0)
  BaseFeature = -> Fillet058
  Profile = -> Sketch122
  ReferenceAxis = -> Sketch122 [Edge1]
  Suppressed = false
  Type = 0
FEATURE [PartDesign::Revolution] Revolution064  label="Hip joints001"
  Angle = 360
  Angle2 = 60
  Axis = (1,0,0)
  Base = (15,-298,0)
  BaseFeature = -> Groove057
  Profile = -> Sketch122
  ReferenceAxis = -> Sketch122 [Edge1]
  Reversed = true
  Suppressed = false
  Type = 0
FEATURE [Sketcher::SketchObject] Sketch123
  ArcFitTolerance = 0
  AttachmentSupport = -> [YZ_Plane039]
  FullyConstrained = true
  MakeInternals = false
  MapMode = 5
  Placement = pos=(0,0,0) rot=(0.57735,0.57735,0.57735;2.0944rad)
  sketch-geometry (4):
    g0: LineSegment StartX=-309.733 StartY=84.7574 StartZ=0 EndX=-36.256 EndY=111.745 EndZ=0
    g1: LineSegment StartX=-36.256 StartY=111.745 StartZ=0 EndX=-36.256 EndY=192.709 EndZ=0
    g2: LineSegment StartX=-36.256 StartY=192.709 StartZ=0 EndX=-309.733 EndY=192.709 EndZ=0
    g3: LineSegment StartX=-309.733 StartY=192.709 StartZ=0 EndX=-309.733 EndY=84.7574 EndZ=0
  constraints (9):
    c: Coincident(g0,g1)
    c: Coincident(g1,g2)
    c: Horizontal(g2)
    c: Coincident(g2,g3)
    c: Coincident(g3,g0)
    c: Vertical(g3)
    c: Vertical(g1)
    c: Block(g3)
    c: Block(g0)
FEATURE [PartDesign::Pocket] Pocket021  label="front cut001"
  BaseFeature = -> Revolution064
  Direction = (-1,0,0)
  Length = 5
  Length2 = 5
  Midplane = true
  Profile = -> Sketch123
  ReferenceAxis = -> Sketch123 [N_Axis]
  Suppressed = false
  Type = 1
FEATURE [Sketcher::SketchObject] Sketch124
  ArcFitTolerance = 0
  AttachmentSupport = -> [YZ_Plane039]
  FullyConstrained = true
  MakeInternals = false
  MapMode = 5
  Placement = pos=(0,0,0) rot=(0.57735,0.57735,0.57735;2.0944rad)
  sketch-geometry (4):
    g0: LineSegment StartX=-276.336 StartY=-71.4724 StartZ=0 EndX=-109.323 EndY=-126.411 EndZ=0
    g1: LineSegment StartX=-109.323 StartY=-126.411 StartZ=0 EndX=-109.323 EndY=-220.905 EndZ=0
    g2: LineSegment StartX=-109.323 StartY=-220.905 StartZ=0 EndX=-276.336 EndY=-220.905 EndZ=0
    g3: LineSegment StartX=-276.336 StartY=-220.905 StartZ=0 EndX=-276.336 EndY=-71.4724 EndZ=0
  constraints (9):
    c: Coincident(g0,g1)
    c: Coincident(g1,g2)
    c: Horizontal(g2)
    c: Coincident(g2,g3)
    c: Coincident(g3,g0)
    c: Vertical(g3)
    c: Vertical(g1)
    c: Block(g0)
    c: Block(g2)
FEATURE [PartDesign::Pocket] Pocket022  label="rear cut001"
  BaseFeature = -> Pocket021
  Direction = (-1,0,0)
  Length = 5
  Length2 = 5
  Midplane = true
  Profile = -> Sketch124
  ReferenceAxis = -> Sketch124 [N_Axis]
  Suppressed = false
  Type = 1
FEATURE [PartDesign::Body] Body036  label="Hip001"
  AllowCompound = false
  Group = -> [Sketch120,Revolution063,Sketch121,Groove056,Fillet058,Sketch122,Groove057,Revolution064,Sketch123,Pocket021,Sketch124,Pocket022,Local_CS060,Local_CS062,Local_CS063]
  Origin = -> Origin039
  Placement = pos=(2.274e-13,1197.02,0.388141) rot=(0,0,1;0rad)
  Tip = -> Pocket022
FEATURE [Sketcher::SketchObject] Sketch125
  ArcFitTolerance = 0
  AttachmentSupport = -> [XY_Plane040]
  FullyConstrained = true
  MakeInternals = false
  MapMode = 5
  sketch-geometry (12):
    g0: LineSegment StartX=15.9442 StartY=0 StartZ=0 EndX=306.848 EndY=0 EndZ=0
    g1-g6: Circle [constr] x6 (B-spline internal-alignment scaffolding for g7; pole/knot coordinates omitted)
    g7: BSplineCurve PolesCount=6 KnotsCount=4 Degree=3 IsPeriodic=0
    g8-g11: GeomPoint [constr] x4 (B-spline internal-alignment scaffolding for g7; pole/knot coordinates omitted)
  constraints (9):
    c: PointOnObject(g0,g-1)
    c: Horizontal(g0)
    c: Weight(g1) = 1
    c: Coincident(g7,g0)
    c: Equal(g1, g2-g6) x5
    c: Coincident(g7,g0)
    c: InternalAlignment(g1-g6 -> g7) x6
    c: InternalAlignment(g8-g11 -> g7) x4
    c: Block(g7)
FEATURE [PartDesign::Revolution] Revolution065  label="L Upper limb001"
  Angle = 360
  Angle2 = 60
  Axis = (1,0,0)
  Base = (0,0,0)
  Profile = -> Sketch125
  ReferenceAxis = -> Sketch125 [H_Axis]
  Suppressed = false
  Type = 0
FEATURE [PartDesign::CoordinateSystem] Local_CS064  label="Left upper limb/Shoulder LCS001"
  AttacherType = Attacher::AttachEngine3D
  AttachmentSupport = -> [Revolution065]
  MapMode = 2
FEATURE [PartDesign::CoordinateSystem] Local_CS065  label="Left upper limb/Elbow LCS001"
  AttacherType = Attacher::AttachEngine3D
  AttachmentOffset = pos=(320,0,0) rot=(0,0,1;0rad)
  AttachmentSupport = -> [Revolution065]
  MapMode = 2
  Placement = pos=(320,0,0) rot=(0,0,1;0rad)
FEATURE [Sketcher::SketchObject] Sketch126
  ArcFitTolerance = 0
  AttachmentSupport = -> [XY_Plane040]
  FullyConstrained = true
  MakeInternals = false
  MapMode = 5
  sketch-geometry (2):
    g0: LineSegment StartX=-60 StartY=0 StartZ=0 EndX=60 EndY=0 EndZ=0
    g1: ArcOfCircle CenterX=0 CenterY=0 CenterZ=0 NormalX=0 NormalY=0 NormalZ=1 AngleXU=0 Radius=60 StartAngle=0 EndAngle=3.14159
  constraints (6):
    c: Horizontal(g0)
    c: PointOnObject(g1,g0)
    c: Coincident(g1,g0)
    c: Coincident(g1,g0)
    c: Coincident(g1,g-1)
    c: Radius(g1) = 60
FEATURE [PartDesign::Groove] Groove058  label="L Sloulder cut001"
  Angle = 360
  Angle2 = 60
  Axis = (1,0,0)
  Base = (0,0,0)
  BaseFeature = -> Revolution065
  Profile = -> Sketch126
  ReferenceAxis = -> Sketch126 [H_Axis]
  Reversed = true
  Suppressed = false
  Type = 0
FEATURE [PartDesign::Fillet] Fillet059  label="L Shoulder fillet001"
  Base = -> Groove058 [Edge2]
  BaseFeature = -> Groove058
  Radius = 6
  SupportTransform = false
  Suppressed = false
  UseAllEdges = false
FEATURE [Sketcher::SketchObject] Sketch127
  ArcFitTolerance = 0
  AttachmentSupport = -> [XY_Plane040]
  FullyConstrained = true
  MakeInternals = false
  MapMode = 5
  sketch-geometry (2):
    g0: LineSegment StartX=285 StartY=0 StartZ=0 EndX=355 EndY=0 EndZ=0
    g1: ArcOfCircle CenterX=320 CenterY=0 CenterZ=0 NormalX=0 NormalY=0 NormalZ=1 AngleXU=0 Radius=35 StartAngle=0 EndAngle=3.14159
  constraints (7):
    c: Horizontal(g0)
    c: PointOnObject(g1,g0)
    c: Coincident(g1,g0)
    c: Coincident(g1,g0)
    c: Horizontal(g1,g-1)
    c: DistanceX(g-1,g1) = 320
    c: Radius(g1) = 35
FEATURE [PartDesign::Groove] Groove059  label="L Elbow cut001"
  Angle = 360
  Angle2 = 60
  Axis = (1,0,0)
  Base = (0,0,0)
  BaseFeature = -> Fillet059
  Profile = -> Sketch127
  ReferenceAxis = -> Sketch127 [H_Axis]
  Reversed = true
  Suppressed = false
  Type = 0
FEATURE [PartDesign::Fillet] Fillet060  label="L Elbow fillet001"
  Base = -> Groove059 [Edge1]
  BaseFeature = -> Groove059
  Radius = 3
  SupportTransform = false
  Suppressed = false
  UseAllEdges = false
FEATURE [PartDesign::Revolution] Revolution066  label="L Elbow001"
  Angle = 360
  Angle2 = 60
  Axis = (1,0,0)
  Base = (0,0,0)
  BaseFeature = -> Fillet060
  Profile = -> Sketch127
  ReferenceAxis = -> Sketch127 [H_Axis]
  Suppressed = false
  Type = 0
FEATURE [PartDesign::Body] Body037  label="Left Upper limb001"
  AllowCompound = false
  Group = -> [Sketch125,Revolution065,Sketch126,Groove058,Fillet059,Sketch127,Groove059,Fillet060,Revolution066,Local_CS064,Local_CS065]
  Origin = -> Origin040
  Placement = pos=(184,1453.86,9.35731) rot=(0.698473,0.710589,0.084853;3.3173rad)
  Tip = -> Revolution066
FEATURE [Sketcher::SketchObject] Sketch128
  ArcFitTolerance = 0
  AttachmentSupport = -> [XY_Plane041]
  FullyConstrained = true
  MakeInternals = false
  MapMode = 5
  sketch-geometry (12):
    g0: LineSegment StartX=5.14795 StartY=0 StartZ=0 EndX=267.265 EndY=0 EndZ=0
    g1-g6: Circle [constr] x6 (B-spline internal-alignment scaffolding for g7; pole/knot coordinates omitted)
    g7: BSplineCurve PolesCount=6 KnotsCount=4 Degree=3 IsPeriodic=0
    g8-g11: GeomPoint [constr] x4 (B-spline internal-alignment scaffolding for g7; pole/knot coordinates omitted)
  constraints (9):
    c: PointOnObject(g0,g-1)
    c: Horizontal(g0)
    c: Weight(g1) = 1
    c: Coincident(g7,g0)
    c: Equal(g1, g2-g6) x5
    c: Coincident(g7,g0)
    c: InternalAlignment(g1-g6 -> g7) x6
    c: InternalAlignment(g8-g11 -> g7) x4
    c: Block(g7)
FEATURE [PartDesign::Revolution] Revolution067  label="Left Forearm main body001"
  Angle = 360
  Angle2 = 60
  Axis = (1,0,0)
  Base = (0,0,0)
  Profile = -> Sketch128
  ReferenceAxis = -> Sketch128 [H_Axis]
  Suppressed = false
  Type = 0
FEATURE [PartDesign::CoordinateSystem] Local_CS066  label="Left Forearm/Elbow001"
  AttacherType = Attacher::AttachEngine3D
  AttachmentSupport = -> [Revolution067]
  MapMode = 2
FEATURE [PartDesign::CoordinateSystem] Local_CS067  label="Left Forearm/Wrist001"
  AttacherType = Attacher::AttachEngine3D
  AttachmentOffset = pos=(253,0,0) rot=(0,0,1;0rad)
  AttachmentSupport = -> [Revolution067]
  MapMode = 2
  Placement = pos=(253,0,0) rot=(0,0,1;0rad)
FEATURE [Sketcher::SketchObject] Sketch129
  ArcFitTolerance = 0
  AttachmentSupport = -> [XY_Plane041]
  FullyConstrained = true
  MakeInternals = false
  MapMode = 5
  sketch-geometry (2):
    g0: LineSegment StartX=-35 StartY=0 StartZ=0 EndX=35 EndY=0 EndZ=0
    g1: ArcOfCircle CenterX=0 CenterY=0 CenterZ=0 NormalX=0 NormalY=0 NormalZ=1 AngleXU=0 Radius=35 StartAngle=0 EndAngle=3.14159
  constraints (6):
    c: Horizontal(g0)
    c: PointOnObject(g1,g0)
    c: Coincident(g1,g0)
    c: Coincident(g1,g0)
    c: Coincident(g1,g-1)
    c: Radius(g1) = 35
FEATURE [PartDesign::Groove] Groove060  label="Left elbow cut001"
  Angle = 360
  Angle2 = 60
  Axis = (1,0,0)
  Base = (0,0,0)
  BaseFeature = -> Revolution067
  Profile = -> Sketch129
  ReferenceAxis = -> Sketch129 [H_Axis]
  Reversed = true
  Suppressed = false
  Type = 0
FEATURE [PartDesign::Fillet] Fillet061  label="Left elbow fillet001"
  Base = -> Groove060 [Edge2]
  BaseFeature = -> Groove060
  Radius = 3
  SupportTransform = false
  Suppressed = false
  UseAllEdges = false
FEATURE [Sketcher::SketchObject] Sketch130
  ArcFitTolerance = 0
  AttachmentSupport = -> [XY_Plane041]
  FullyConstrained = true
  MakeInternals = false
  MapMode = 5
  sketch-geometry (2):
    g0: LineSegment StartX=228 StartY=-3.5608e-12 StartZ=0 EndX=278 EndY=-3.5608e-12 EndZ=0
    g1: ArcOfCircle CenterX=253 CenterY=0 CenterZ=0 NormalX=0 NormalY=0 NormalZ=1 AngleXU=0 Radius=25 StartAngle=-9e-16 EndAngle=3.14159
  constraints (7):
    c: Horizontal(g0)
    c: PointOnObject(g1,g0)
    c: Coincident(g1,g0)
    c: Coincident(g1,g0)
    c: Horizontal(g1,g-1)
    c: DistanceX(g-1,g1) = 253
    c: Radius(g1) = 25
FEATURE [PartDesign::Groove] Groove061  label="Left wrist cut001"
  Angle = 360
  Angle2 = 60
  Axis = (1,0,0)
  Base = (0,0,0)
  BaseFeature = -> Fillet061
  Profile = -> Sketch130
  ReferenceAxis = -> Sketch130 [H_Axis]
  Reversed = true
  Suppressed = false
  Type = 0
FEATURE [PartDesign::Fillet] Fillet062  label="Left wrist fillet001"
  Base = -> Groove061 [Edge1]
  BaseFeature = -> Groove061
  Radius = 3
  SupportTransform = false
  Suppressed = false
  UseAllEdges = false
FEATURE [PartDesign::Revolution] Revolution068  label="Left wrist001"
  Angle = 360
  Angle2 = 60
  Axis = (1,0,0)
  Base = (0,0,0)
  BaseFeature = -> Fillet062
  Profile = -> Sketch130
  ReferenceAxis = -> Sketch130 [H_Axis]
  Suppressed = false
  Type = 0
FEATURE [PartDesign::Body] Body038  label="Left Forearm001"
  AllowCompound = false
  Group = -> [Sketch128,Revolution067,Sketch129,Groove060,Fillet061,Sketch130,Groove061,Fillet062,Revolution068,Local_CS066,Local_CS067]
  Origin = -> Origin041
  Placement = pos=(178.756,1764.32,86.7457) rot=(-0.55282,-0.581384,0.596978;2.13844rad)
  Tip = -> Revolution068
FEATURE [Sketcher::SketchObject] Sketch131
  ArcFitTolerance = 0
  AttachmentSupport = -> [XY_Plane042]
  FullyConstrained = true
  MakeInternals = false
  MapMode = 5
  sketch-geometry (10):
    g0: LineSegment StartX=6.14917 StartY=0 StartZ=0 EndX=149.382 EndY=0 EndZ=0
    g1-g5: Circle [constr] x5 (B-spline internal-alignment scaffolding for g6; pole/knot coordinates omitted)
    g6: BSplineCurve PolesCount=5 KnotsCount=3 Degree=3 IsPeriodic=0
    g7: GeomPoint [constr] X=6.14917 Y=0 Z=0
    g8: GeomPoint [constr] X=80.1264 Y=42.7238 Z=0
    g9: GeomPoint [constr] X=149.382 Y=0 Z=0
  constraints (12):
    c: PointOnObject(g0,g-1)
    c: Horizontal(g0)
    c: Weight(g1) = 1
    c: Coincident(g6,g0)
    c: Equal(g1, g2-g5) x4
    c: Coincident(g6,g0)
    c: InternalAlignment(g1-g5 -> g6) x5
    c: InternalAlignment(g7,g6)
    c: InternalAlignment(g8,g6)
    c: InternalAlignment(g9,g6)
    c: Vertical(g0,g4)
    c: Block(g6)
FEATURE [PartDesign::Revolution] Revolution069  label="L hand main body001"
  Angle = 360
  Angle2 = 60
  Axis = (1,0,0)
  Base = (0,0,0)
  Profile = -> Sketch131
  ReferenceAxis = -> Sketch131 [H_Axis]
  Suppressed = false
  Type = 0
FEATURE [PartDesign::CoordinateSystem] Local_CS068  label="Left Hand/Wrist LCS001"
  AttacherType = Attacher::AttachEngine3D
  AttachmentSupport = -> [Revolution069]
  MapMode = 2
FEATURE [Sketcher::SketchObject] Sketch132
  ArcFitTolerance = 0
  AttachmentSupport = -> [XY_Plane042]
  FullyConstrained = true
  MakeInternals = false
  MapMode = 5
  sketch-geometry (2):
    g0: LineSegment StartX=-25 StartY=0 StartZ=0 EndX=25 EndY=0 EndZ=0
    g1: ArcOfCircle CenterX=0 CenterY=0 CenterZ=0 NormalX=0 NormalY=0 NormalZ=1 AngleXU=0 Radius=25 StartAngle=0 EndAngle=3.14159
  constraints (6):
    c: Horizontal(g0)
    c: PointOnObject(g1,g0)
    c: Coincident(g1,g0)
    c: Coincident(g1,g0)
    c: Coincident(g1,g-1)
    c: Radius(g1) = 25
FEATURE [PartDesign::Groove] Groove062  label="wrist cut002"
  Angle = 360
  Angle2 = 60
  Axis = (1,0,0)
  Base = (0,0,0)
  BaseFeature = -> Revolution069
  Profile = -> Sketch132
  ReferenceAxis = -> Sketch132 [H_Axis]
  Reversed = true
  Suppressed = false
  Type = 0
FEATURE [PartDesign::Fillet] Fillet063  label="wrist fillet002"
  Base = -> Groove062 [Edge1]
  BaseFeature = -> Groove062
  Radius = 3
  SupportTransform = false
  Suppressed = false
  UseAllEdges = false
FEATURE [Sketcher::SketchObject] Sketch133
  ArcFitTolerance = 0
  AttachmentSupport = -> [YZ_Plane042]
  FullyConstrained = true
  MakeInternals = false
  MapMode = 5
  Placement = pos=(0,0,0) rot=(0.57735,0.57735,0.57735;2.0944rad)
  sketch-geometry (3):
    g0: ArcOfCircle CenterX=0 CenterY=125.857 CenterZ=0 NormalX=0 NormalY=0 NormalZ=1 AngleXU=0 Radius=99.8092 StartAngle=3.99571 EndAngle=5.39163
    g1: LineSegment StartX=-65.5632 StartY=50.6013 StartZ=0 EndX=0 EndY=125.857 EndZ=0
    g2: LineSegment StartX=0 StartY=125.857 StartZ=0 EndX=62.7007 EndY=48.2002 EndZ=0
  constraints (6):
    c: PointOnObject(g0,g-2)
    c: Coincident(g1,g0)
    c: Coincident(g1,g0)
    c: Coincident(g2,g0)
    c: Coincident(g2,g0)
    c: Block(g0)
FEATURE [PartDesign::Pocket] Pocket023
  BaseFeature = -> Fillet063
  Direction = (1,0,0)
  Length = 5
  Length2 = 5
  Profile = -> Sketch133
  ReferenceAxis = -> Sketch133 [N_Axis]
  Suppressed = false
  Type = 1
  UseCustomVector = true
FEATURE [Sketcher::SketchObject] Sketch134
  ArcFitTolerance = 0
  AttachmentSupport = -> [YZ_Plane042]
  FullyConstrained = true
  MakeInternals = false
  MapMode = 5
  Placement = pos=(0,0,0) rot=(0.57735,0.57735,0.57735;2.0944rad)
  sketch-geometry (4):
    g0: ArcOfCircle CenterX=0 CenterY=78.6838 CenterZ=0 NormalX=0 NormalY=0 NormalZ=1 AngleXU=0 Radius=107.987 StartAngle=3.91888 EndAngle=5.56935
    g1: LineSegment StartX=81.6221 StartY=7.98042 StartZ=0 EndX=81.6221 EndY=-69.912 EndZ=0
    g2: LineSegment StartX=81.6221 StartY=-69.912 StartZ=0 EndX=-76.9748 EndY=-69.912 EndZ=0
    g3: LineSegment StartX=-76.9748 StartY=-69.912 StartZ=0 EndX=-76.9748 EndY=2.94733 EndZ=0
  constraints (10):
    c: PointOnObject(g0,g-2)
    c: Coincident(g0,g1)
    c: Coincident(g1,g2)
    c: Horizontal(g2)
    c: Coincident(g2,g3)
    c: Coincident(g3,g0)
    c: Vertical(g3)
    c: Vertical(g1)
    c: Block(g0)
    c: Block(g2)
FEATURE [PartDesign::Pocket] Pocket024
  BaseFeature = -> Pocket023
  Direction = (1,0,0)
  Length = 5
  Length2 = 5
  Profile = -> Sketch134
  ReferenceAxis = -> Sketch134 [N_Axis]
  Suppressed = false
  Type = 1
  UseCustomVector = true
FEATURE [PartDesign::Body] Body039  label="Left hand001"
  AllowCompound = false
  Group = -> [Sketch131,Revolution069,Sketch132,Groove062,Fillet063,Sketch133,Pocket023,Sketch134,Pocket024,Local_CS068]
  Origin = -> Origin042
  Placement = pos=(161.621,2016.7,82.3811) rot=(-0.568687,-0.575808,0.587401;2.1932rad)
  Tip = -> Pocket024
FEATURE [Sketcher::SketchObject] Sketch135
  ArcFitTolerance = 0
  AttachmentSupport = -> [XY_Plane043]
  FullyConstrained = true
  MakeInternals = false
  MapMode = 5
  sketch-geometry (12):
    g0: LineSegment StartX=15.9442 StartY=0 StartZ=0 EndX=306.848 EndY=0 EndZ=0
    g1-g6: Circle [constr] x6 (B-spline internal-alignment scaffolding for g7; pole/knot coordinates omitted)
    g7: BSplineCurve PolesCount=6 KnotsCount=4 Degree=3 IsPeriodic=0
    g8-g11: GeomPoint [constr] x4 (B-spline internal-alignment scaffolding for g7; pole/knot coordinates omitted)
  constraints (9):
    c: PointOnObject(g0,g-1)
    c: Horizontal(g0)
    c: Weight(g1) = 1
    c: Coincident(g7,g0)
    c: Equal(g1, g2-g6) x5
    c: Coincident(g7,g0)
    c: InternalAlignment(g1-g6 -> g7) x6
    c: InternalAlignment(g8-g11 -> g7) x4
    c: Block(g7)
FEATURE [PartDesign::Revolution] Revolution070  label="R Upper limb001"
  Angle = 360
  Angle2 = 60
  Axis = (1,0,0)
  Base = (0,0,0)
  Profile = -> Sketch135
  ReferenceAxis = -> Sketch135 [H_Axis]
  Suppressed = false
  Type = 0
FEATURE [PartDesign::CoordinateSystem] Local_CS069  label="Right upper limb/Shoulder LCS001"
  AttacherType = Attacher::AttachEngine3D
  AttachmentOffset = pos=(0,0,0) rot=(0,0,1;3.14159rad)
  AttachmentSupport = -> [Revolution070]
  MapMode = 2
  Placement = pos=(0,0,0) rot=(0,0,1;3.14159rad)
FEATURE [PartDesign::CoordinateSystem] Local_CS070  label="Right upper limb/Elbow LCS001"
  AttacherType = Attacher::AttachEngine3D
  AttachmentOffset = pos=(320,0,0) rot=(0,0,1;3.14159rad)
  AttachmentSupport = -> [Revolution070]
  MapMode = 2
  Placement = pos=(320,0,0) rot=(0,0,1;3.14159rad)
FEATURE [Sketcher::SketchObject] Sketch136
  ArcFitTolerance = 0
  AttachmentSupport = -> [XY_Plane043]
  FullyConstrained = true
  MakeInternals = false
  MapMode = 5
  sketch-geometry (2):
    g0: LineSegment StartX=-60 StartY=7.3e-15 StartZ=0 EndX=60 EndY=7.3e-15 EndZ=0
    g1: ArcOfCircle CenterX=0 CenterY=0 CenterZ=0 NormalX=0 NormalY=0 NormalZ=1 AngleXU=0 Radius=60 StartAngle=0 EndAngle=3.14159
  constraints (6):
    c: Horizontal(g0)
    c: PointOnObject(g1,g0)
    c: Coincident(g1,g0)
    c: Coincident(g1,g0)
    c: Coincident(g1,g-1)
    c: Radius(g1) = 60
FEATURE [PartDesign::Groove] Groove063  label="R Sloulder cut001"
  Angle = 360
  Angle2 = 60
  Axis = (1,0,0)
  Base = (0,0,0)
  BaseFeature = -> Revolution070
  Profile = -> Sketch136
  ReferenceAxis = -> Sketch136 [H_Axis]
  Reversed = true
  Suppressed = false
  Type = 0
FEATURE [PartDesign::Fillet] Fillet064  label="R Shoulder fillet001"
  Base = -> Groove063 [Edge2]
  BaseFeature = -> Groove063
  Radius = 6
  SupportTransform = false
  Suppressed = false
  UseAllEdges = false
FEATURE [Sketcher::SketchObject] Sketch137
  ArcFitTolerance = 0
  AttachmentSupport = -> [XY_Plane043]
  FullyConstrained = true
  MakeInternals = false
  MapMode = 5
  sketch-geometry (2):
    g0: LineSegment StartX=285 StartY=4.3e-15 StartZ=0 EndX=355 EndY=4.3e-15 EndZ=0
    g1: ArcOfCircle CenterX=320 CenterY=0 CenterZ=0 NormalX=0 NormalY=0 NormalZ=1 AngleXU=0 Radius=35 StartAngle=0 EndAngle=3.14159
  constraints (7):
    c: Horizontal(g0)
    c: PointOnObject(g1,g0)
    c: Coincident(g1,g0)
    c: Coincident(g1,g0)
    c: Horizontal(g1,g-1)
    c: DistanceX(g-1,g1) = 320
    c: Radius(g1) = 35
FEATURE [PartDesign::Groove] Groove064  label="R Elbow cut001"
  Angle = 360
  Angle2 = 60
  Axis = (1,0,0)
  Base = (0,0,0)
  BaseFeature = -> Fillet064
  Profile = -> Sketch137
  ReferenceAxis = -> Sketch137 [H_Axis]
  Reversed = true
  Suppressed = false
  Type = 0
FEATURE [PartDesign::Fillet] Fillet065  label="R Elbow fillet001"
  Base = -> Groove064 [Edge1]
  BaseFeature = -> Groove064
  Radius = 3
  SupportTransform = false
  Suppressed = false
  UseAllEdges = false
FEATURE [PartDesign::Revolution] Revolution071  label="R Elbow001"
  Angle = 360
  Angle2 = 60
  Axis = (1,0,0)
  Base = (0,0,0)
  BaseFeature = -> Fillet065
  Profile = -> Sketch137
  ReferenceAxis = -> Sketch137 [H_Axis]
  Suppressed = false
  Type = 0
FEATURE [PartDesign::Body] Body040  label="Right Upper limb001"
  AllowCompound = false
  Group = -> [Sketch135,Revolution070,Sketch136,Groove063,Fillet064,Sketch137,Groove064,Fillet065,Revolution071,Local_CS069,Local_CS070]
  Origin = -> Origin043
  Placement = pos=(-184,1453.86,9.35731) rot=(0.684832,0.710819,0.160444;3.40911rad)
  Tip = -> Revolution071
FEATURE [Sketcher::SketchObject] Sketch138
  ArcFitTolerance = 0
  AttachmentSupport = -> [XY_Plane044]
  FullyConstrained = true
  MakeInternals = false
  MapMode = 5
  sketch-geometry (12):
    g0: LineSegment StartX=5.14795 StartY=0 StartZ=0 EndX=267.265 EndY=0 EndZ=0
    g1-g6: Circle [constr] x6 (B-spline internal-alignment scaffolding for g7; pole/knot coordinates omitted)
    g7: BSplineCurve PolesCount=6 KnotsCount=4 Degree=3 IsPeriodic=0
    g8-g11: GeomPoint [constr] x4 (B-spline internal-alignment scaffolding for g7; pole/knot coordinates omitted)
  constraints (9):
    c: PointOnObject(g0,g-1)
    c: Horizontal(g0)
    c: Weight(g1) = 1
    c: Coincident(g7,g0)
    c: Equal(g1, g2-g6) x5
    c: Coincident(g7,g0)
    c: InternalAlignment(g1-g6 -> g7) x6
    c: InternalAlignment(g8-g11 -> g7) x4
    c: Block(g7)
FEATURE [PartDesign::Revolution] Revolution072  label="Right Forearm main body001"
  Angle = 360
  Angle2 = 60
  Axis = (1,0,0)
  Base = (0,0,0)
  Profile = -> Sketch138
  ReferenceAxis = -> Sketch138 [H_Axis]
  Suppressed = false
  Type = 0
FEATURE [PartDesign::CoordinateSystem] Local_CS071  label="Right Forearm/Elbow001"
  AttacherType = Attacher::AttachEngine3D
  AttachmentOffset = pos=(0,0,0) rot=(0,0,1;3.14159rad)
  AttachmentSupport = -> [Revolution072]
  MapMode = 2
  Placement = pos=(0,0,0) rot=(0,0,1;3.14159rad)
FEATURE [PartDesign::CoordinateSystem] Local_CS072  label="Right Forearm/Wrist001"
  AttacherType = Attacher::AttachEngine3D
  AttachmentOffset = pos=(253,0,0) rot=(0,0,1;3.14159rad)
  AttachmentSupport = -> [Revolution072]
  MapMode = 2
  Placement = pos=(253,0,0) rot=(0,0,1;3.14159rad)
FEATURE [Sketcher::SketchObject] Sketch139
  ArcFitTolerance = 0
  AttachmentSupport = -> [XY_Plane044]
  FullyConstrained = true
  MakeInternals = false
  MapMode = 5
  sketch-geometry (2):
    g0: LineSegment StartX=-35 StartY=4.3e-15 StartZ=0 EndX=35 EndY=4.3e-15 EndZ=0
    g1: ArcOfCircle CenterX=0 CenterY=0 CenterZ=0 NormalX=0 NormalY=0 NormalZ=1 AngleXU=0 Radius=35 StartAngle=0 EndAngle=3.14159
  constraints (6):
    c: Horizontal(g0)
    c: PointOnObject(g1,g0)
    c: Coincident(g1,g0)
    c: Coincident(g1,g0)
    c: Coincident(g1,g-1)
    c: Radius(g1) = 35
FEATURE [PartDesign::Groove] Groove065  label="Right elbow cut001"
  Angle = 360
  Angle2 = 60
  Axis = (1,0,0)
  Base = (0,0,0)
  BaseFeature = -> Revolution072
  Profile = -> Sketch139
  ReferenceAxis = -> Sketch139 [H_Axis]
  Reversed = true
  Suppressed = false
  Type = 0
FEATURE [PartDesign::Fillet] Fillet066  label="Right elbow fillet001"
  Base = -> Groove065 [Edge2]
  BaseFeature = -> Groove065
  Radius = 3
  SupportTransform = false
  Suppressed = false
  UseAllEdges = false
FEATURE [Sketcher::SketchObject] Sketch140
  ArcFitTolerance = 0
  AttachmentSupport = -> [XY_Plane044]
  FullyConstrained = true
  MakeInternals = false
  MapMode = 5
  sketch-geometry (2):
    g0: LineSegment StartX=228 StartY=-3.5608e-12 StartZ=0 EndX=278 EndY=-3.5608e-12 EndZ=0
    g1: ArcOfCircle CenterX=253 CenterY=0 CenterZ=0 NormalX=0 NormalY=0 NormalZ=1 AngleXU=0 Radius=25 StartAngle=-9e-16 EndAngle=3.14159
  constraints (7):
    c: Horizontal(g0)
    c: PointOnObject(g1,g0)
    c: Coincident(g1,g0)
    c: Coincident(g1,g0)
    c: Horizontal(g1,g-1)
    c: DistanceX(g-1,g1) = 253
    c: Radius(g1) = 25
FEATURE [PartDesign::Groove] Groove066  label="Right wrist cut001"
  Angle = 360
  Angle2 = 60
  Axis = (1,0,0)
  Base = (0,0,0)
  BaseFeature = -> Fillet066
  Profile = -> Sketch140
  ReferenceAxis = -> Sketch140 [H_Axis]
  Reversed = true
  Suppressed = false
  Type = 0
FEATURE [PartDesign::Fillet] Fillet067  label="Right wrist fillet001"
  Base = -> Groove066 [Edge1]
  BaseFeature = -> Groove066
  Radius = 3
  SupportTransform = false
  Suppressed = false
  UseAllEdges = false
FEATURE [PartDesign::Revolution] Revolution073  label="Right wrist001"
  Angle = 360
  Angle2 = 60
  Axis = (1,0,0)
  Base = (0,0,0)
  BaseFeature = -> Fillet067
  Profile = -> Sketch140
  ReferenceAxis = -> Sketch140 [H_Axis]
  Suppressed = false
  Type = 0
FEATURE [PartDesign::Body] Body041  label="Right Forearm001"
  AllowCompound = false
  Group = -> [Sketch138,Revolution072,Sketch139,Groove065,Fillet066,Sketch140,Groove066,Fillet067,Revolution073,Local_CS071,Local_CS072]
  Origin = -> Origin044
  Placement = pos=(-197.799,1746.3,138.556) rot=(-0.504823,-0.708144,-0.493645;4.45019rad)
  Tip = -> Revolution073
FEATURE [Sketcher::SketchObject] Sketch141
  ArcFitTolerance = 0
  AttachmentSupport = -> [XY_Plane045]
  FullyConstrained = true
  MakeInternals = false
  MapMode = 5
  sketch-geometry (10):
    g0: LineSegment StartX=6.14917 StartY=0 StartZ=0 EndX=149.382 EndY=0 EndZ=0
    g1-g5: Circle [constr] x5 (B-spline internal-alignment scaffolding for g6; pole/knot coordinates omitted)
    g6: BSplineCurve PolesCount=5 KnotsCount=3 Degree=3 IsPeriodic=0
    g7: GeomPoint [constr] X=6.14917 Y=0 Z=0
    g8: GeomPoint [constr] X=80.1264 Y=42.7238 Z=0
    g9: GeomPoint [constr] X=149.382 Y=0 Z=0
  constraints (12):
    c: PointOnObject(g0,g-1)
    c: Horizontal(g0)
    c: Weight(g1) = 1
    c: Coincident(g6,g0)
    c: Equal(g1, g2-g5) x4
    c: Coincident(g6,g0)
    c: InternalAlignment(g1-g5 -> g6) x5
    c: InternalAlignment(g7,g6)
    c: InternalAlignment(g8,g6)
    c: InternalAlignment(g9,g6)
    c: Vertical(g0,g4)
    c: Block(g6)
FEATURE [PartDesign::Revolution] Revolution074  label="R hand main body001"
  Angle = 360
  Angle2 = 60
  Axis = (1,0,0)
  Base = (0,0,0)
  Profile = -> Sketch141
  ReferenceAxis = -> Sketch141 [H_Axis]
  Suppressed = false
  Type = 0
FEATURE [PartDesign::CoordinateSystem] Local_CS073  label="Right Hand/Wrist LCS001"
  AttacherType = Attacher::AttachEngine3D
  AttachmentOffset = pos=(0,0,0) rot=(0,0,1;3.14159rad)
  AttachmentSupport = -> [Revolution074]
  MapMode = 2
  Placement = pos=(0,0,0) rot=(0,0,1;3.14159rad)
FEATURE [Sketcher::SketchObject] Sketch142
  ArcFitTolerance = 0
  AttachmentSupport = -> [XY_Plane045]
  FullyConstrained = true
  MakeInternals = false
  MapMode = 5
  sketch-geometry (2):
    g0: LineSegment StartX=-25 StartY=0 StartZ=0 EndX=25 EndY=0 EndZ=0
    g1: ArcOfCircle CenterX=0 CenterY=0 CenterZ=0 NormalX=0 NormalY=0 NormalZ=1 AngleXU=0 Radius=25 StartAngle=0 EndAngle=3.14159
  constraints (6):
    c: Horizontal(g0)
    c: PointOnObject(g1,g0)
    c: Coincident(g1,g0)
    c: Coincident(g1,g0)
    c: Coincident(g1,g-1)
    c: Radius(g1) = 25
FEATURE [PartDesign::Groove] Groove067  label="wrist cut003"
  Angle = 360
  Angle2 = 60
  Axis = (1,0,0)
  Base = (0,0,0)
  BaseFeature = -> Revolution074
  Profile = -> Sketch142
  ReferenceAxis = -> Sketch142 [H_Axis]
  Reversed = true
  Suppressed = false
  Type = 0
FEATURE [PartDesign::Fillet] Fillet068  label="wrist fillet003"
  Base = -> Groove067 [Edge1]
  BaseFeature = -> Groove067
  Radius = 3
  SupportTransform = false
  Suppressed = false
  UseAllEdges = false
FEATURE [Sketcher::SketchObject] Sketch143
  ArcFitTolerance = 0
  AttachmentSupport = -> [YZ_Plane045]
  FullyConstrained = true
  MakeInternals = false
  MapMode = 5
  Placement = pos=(0,0,0) rot=(0.57735,0.57735,0.57735;2.0944rad)
  sketch-geometry (3):
    g0: ArcOfCircle CenterX=0 CenterY=125.857 CenterZ=0 NormalX=0 NormalY=0 NormalZ=1 AngleXU=0 Radius=99.8092 StartAngle=3.99571 EndAngle=5.39163
    g1: LineSegment StartX=-65.5632 StartY=50.6013 StartZ=0 EndX=0 EndY=125.857 EndZ=0
    g2: LineSegment StartX=0 StartY=125.857 StartZ=0 EndX=62.7007 EndY=48.2002 EndZ=0
  constraints (6):
    c: PointOnObject(g0,g-2)
    c: Coincident(g1,g0)
    c: Coincident(g1,g0)
    c: Coincident(g2,g0)
    c: Coincident(g2,g0)
    c: Block(g0)
FEATURE [PartDesign::Pocket] Pocket025
  BaseFeature = -> Fillet068
  Direction = (1,0,0)
  Length = 5
  Length2 = 5
  Profile = -> Sketch143
  ReferenceAxis = -> Sketch143 [N_Axis]
  Suppressed = false
  Type = 1
  UseCustomVector = true
FEATURE [Sketcher::SketchObject] Sketch144
  ArcFitTolerance = 0
  AttachmentSupport = -> [YZ_Plane045]
  FullyConstrained = true
  MakeInternals = false
  MapMode = 5
  Placement = pos=(0,0,0) rot=(0.57735,0.57735,0.57735;2.0944rad)
  sketch-geometry (4):
    g0: ArcOfCircle CenterX=0 CenterY=78.6838 CenterZ=0 NormalX=0 NormalY=0 NormalZ=1 AngleXU=0 Radius=107.987 StartAngle=3.91888 EndAngle=5.56935
    g1: LineSegment StartX=81.6221 StartY=7.98042 StartZ=0 EndX=81.6221 EndY=-69.912 EndZ=0
    g2: LineSegment StartX=81.6221 StartY=-69.912 StartZ=0 EndX=-76.9748 EndY=-69.912 EndZ=0
    g3: LineSegment StartX=-76.9748 StartY=-69.912 StartZ=0 EndX=-76.9748 EndY=2.94733 EndZ=0
  constraints (10):
    c: PointOnObject(g0,g-2)
    c: Coincident(g0,g1)
    c: Coincident(g1,g2)
    c: Horizontal(g2)
    c: Coincident(g2,g3)
    c: Coincident(g3,g0)
    c: Vertical(g3)
    c: Vertical(g1)
    c: Block(g0)
    c: Block(g2)
FEATURE [PartDesign::Pocket] Pocket026
  BaseFeature = -> Pocket025
  Direction = (1,0,0)
  Length = 5
  Length2 = 5
  Profile = -> Sketch144
  ReferenceAxis = -> Sketch144 [N_Axis]
  Suppressed = false
  Type = 1
  UseCustomVector = true
FEATURE [PartDesign::Body] Body042  label="Right hand001"
  AllowCompound = false
  Group = -> [Sketch141,Revolution074,Sketch142,Groove067,Fillet068,Sketch143,Pocket025,Sketch144,Pocket026,Local_CS073]
  Origin = -> Origin045
  Placement = pos=(-182.19,1980.81,44.9097) rot=(-0.532615,-0.724966,-0.436744;4.45094rad)
  Tip = -> Pocket026
FEATURE [Sketcher::SketchObject] Sketch145
  ArcFitTolerance = 0
  AttachmentSupport = -> [XY_Plane046]
  FullyConstrained = true
  MakeInternals = false
  MapMode = 5
  sketch-geometry (14):
    g0: LineSegment StartX=0 StartY=-29.246 StartZ=0 EndX=0 EndY=-395.97 EndZ=0
    g1-g7: Circle [constr] x7 (B-spline internal-alignment scaffolding for g8; pole/knot coordinates omitted)
    g8: BSplineCurve PolesCount=7 KnotsCount=5 Degree=3 IsPeriodic=0
    g9-g13: GeomPoint [constr] x5 (B-spline internal-alignment scaffolding for g8; pole/knot coordinates omitted)
  constraints (11):
    c: PointOnObject(g0,g-2)
    c: Vertical(g0)
    c: Weight(g1) = 1
    c: Coincident(g8,g0)
    c: Equal(g1, g2-g7) x6
    c: Coincident(g8,g0)
    c: InternalAlignment(g1-g7 -> g8) x7
    c: InternalAlignment(g9-g13 -> g8) x5
    c: Horizontal(g0,g6)
    c: Horizontal(g0,g2)
    c: Block(g8)
FEATURE [PartDesign::Revolution] Revolution075  label="L Thigh main body001"
  Angle = 360
  Angle2 = 60
  Axis = (0,1,0)
  Base = (0,0,0)
  Profile = -> Sketch145
  ReferenceAxis = -> Sketch145 [V_Axis]
  Reversed = true
  Suppressed = false
  Type = 0
FEATURE [PartDesign::CoordinateSystem] Local_CS074  label="Left Thigh/Big joint LCS001"
  AttacherType = Attacher::AttachEngine3D
  AttachmentSupport = -> [Revolution075]
  MapMode = 2
FEATURE [PartDesign::CoordinateSystem] Local_CS075  label="Left Thigh/Knee LCS001"
  AttacherType = Attacher::AttachEngine3D
  AttachmentOffset = pos=(0,-403,0) rot=(0,0,1;0rad)
  AttachmentSupport = -> [Revolution075]
  MapMode = 2
  Placement = pos=(0,-403,0) rot=(0,0,1;0rad)
FEATURE [Sketcher::SketchObject] Sketch146
  ArcFitTolerance = 0
  AttachmentSupport = -> [XY_Plane046]
  FullyConstrained = true
  MakeInternals = false
  MapMode = 5
  sketch-geometry (2):
    g0: LineSegment StartX=1.84e-14 StartY=60 StartZ=0 EndX=1.84e-14 EndY=-60 EndZ=0
    g1: ArcOfCircle CenterX=0 CenterY=0 CenterZ=0 NormalX=0 NormalY=0 NormalZ=1 AngleXU=0 Radius=60 StartAngle=4.71239 EndAngle=7.85398
  constraints (6):
    c: Vertical(g0)
    c: PointOnObject(g1,g0)
    c: Coincident(g1,g0)
    c: Coincident(g1,g0)
    c: Coincident(g1,g-1)
    c: Radius(g1) = 60
FEATURE [PartDesign::Groove] Groove068  label="L Big joint001"
  Angle = 360
  Angle2 = 60
  Axis = (0,1,0)
  Base = (0,0,0)
  BaseFeature = -> Revolution075
  Profile = -> Sketch146
  ReferenceAxis = -> Sketch146 [V_Axis]
  Suppressed = false
  Type = 0
FEATURE [PartDesign::Fillet] Fillet069
  Base = -> Groove068 [Edge1]
  BaseFeature = -> Groove068
  Radius = 6
  SupportTransform = false
  Suppressed = false
  UseAllEdges = false
FEATURE [Sketcher::SketchObject] Sketch147
  ArcFitTolerance = 0
  AttachmentSupport = -> [XY_Plane046]
  FullyConstrained = true
  MakeInternals = false
  MapMode = 5
  sketch-geometry (2):
    g0: LineSegment StartX=-6.4e-15 StartY=-368 StartZ=0 EndX=-6.4e-15 EndY=-438 EndZ=0
    g1: ArcOfCircle CenterX=0 CenterY=-403 CenterZ=0 NormalX=0 NormalY=0 NormalZ=1 AngleXU=0 Radius=35 StartAngle=4.71239 EndAngle=7.85398
  constraints (7):
    c: Vertical(g0)
    c: PointOnObject(g1,g0)
    c: Coincident(g1,g0)
    c: Coincident(g1,g0)
    c: PointOnObject(g1,g-2)
    c: DistanceY(g1,g-1) = 403
    c: Radius(g1) = 35
FEATURE [PartDesign::Groove] Groove069  label="L Knee cut001"
  Angle = 360
  Angle2 = 60
  Axis = (0,1,0)
  Base = (0,0,0)
  BaseFeature = -> Fillet069
  Profile = -> Sketch147
  ReferenceAxis = -> Sketch147 [V_Axis]
  Suppressed = false
  Type = 0
FEATURE [PartDesign::Fillet] Fillet070
  Base = -> Groove069 [Edge1]
  BaseFeature = -> Groove069
  Radius = 3
  SupportTransform = false
  Suppressed = false
  UseAllEdges = false
FEATURE [PartDesign::Revolution] Revolution076  label="L Knee001"
  Angle = 360
  Angle2 = 60
  Axis = (0,1,0)
  Base = (0,0,0)
  BaseFeature = -> Fillet070
  Profile = -> Sketch147
  ReferenceAxis = -> Sketch147 [V_Axis]
  Reversed = true
  Suppressed = false
  Type = 0
FEATURE [PartDesign::Body] Body043  label="Left Thigh001"
  AllowCompound = false
  Group = -> [Sketch145,Revolution075,Sketch146,Groove068,Fillet069,Sketch147,Groove069,Fillet070,Revolution076,Local_CS074,Local_CS075]
  Origin = -> Origin046
  Placement = pos=(75,899.018,0.388141) rot=(1,0,0;0.05236rad)
  Tip = -> Revolution076
FEATURE [Sketcher::SketchObject] Sketch148
  ArcFitTolerance = 0
  AttachmentSupport = -> [XY_Plane047]
  FullyConstrained = true
  MakeInternals = false
  MapMode = 5
  sketch-geometry (14):
    g0: LineSegment StartX=0 StartY=0 StartZ=0 EndX=0 EndY=-428.766 EndZ=0
    g1-g7: Circle [constr] x7 (B-spline internal-alignment scaffolding for g8; pole/knot coordinates omitted)
    g8: BSplineCurve PolesCount=7 KnotsCount=5 Degree=3 IsPeriodic=0
    g9-g13: GeomPoint [constr] x5 (B-spline internal-alignment scaffolding for g8; pole/knot coordinates omitted)
  constraints (9):
    c: Vertical(g0)
    c: PointOnObject(g0,g-2)
    c: Weight(g1) = 1
    c: Coincident(g8,g0)
    c: Equal(g1, g2-g7) x6
    c: Coincident(g8,g0)
    c: InternalAlignment(g1-g7 -> g8) x7
    c: InternalAlignment(g9-g13 -> g8) x5
    c: Block(g8)
FEATURE [PartDesign::Revolution] Revolution077  label="L Shin main body001"
  Angle = 360
  Angle2 = 60
  Axis = (0,1,0)
  Base = (0,0,0)
  Profile = -> Sketch148
  ReferenceAxis = -> Sketch148 [V_Axis]
  Reversed = true
  Suppressed = false
  Type = 0
FEATURE [PartDesign::CoordinateSystem] Local_CS076  label="Left Shin/Knee001"
  AttacherType = Attacher::AttachEngine3D
  AttachmentSupport = -> [Revolution077]
  MapMode = 2
FEATURE [PartDesign::CoordinateSystem] Local_CS077  label="Left Shin/Ankle001"
  AttacherType = Attacher::AttachEngine3D
  AttachmentOffset = pos=(0,-435,0) rot=(0,0,1;0rad)
  AttachmentSupport = -> [Revolution077]
  MapMode = 2
  Placement = pos=(0,-435,0) rot=(0,0,1;0rad)
FEATURE [Sketcher::SketchObject] Sketch149
  ArcFitTolerance = 0
  AttachmentSupport = -> [XY_Plane047]
  FullyConstrained = true
  MakeInternals = false
  MapMode = 5
  sketch-geometry (2):
    g0: LineSegment StartX=0 StartY=35 StartZ=0 EndX=0 EndY=-35 EndZ=0
    g1: ArcOfCircle CenterX=0 CenterY=0 CenterZ=0 NormalX=0 NormalY=0 NormalZ=1 AngleXU=0 Radius=35 StartAngle=4.71239 EndAngle=7.85398
  constraints (6):
    c: PointOnObject(g1,g0)
    c: Coincident(g1,g0)
    c: Coincident(g1,g0)
    c: Vertical(g0)
    c: Coincident(g1,g-1)
    c: Radius(g1) = 35
FEATURE [PartDesign::Groove] Groove070  label="L knee cut001"
  Angle = 360
  Angle2 = 60
  Axis = (0,1,0)
  Base = (0,0,0)
  BaseFeature = -> Revolution077
  Profile = -> Sketch149
  ReferenceAxis = -> Sketch149 [V_Axis]
  Suppressed = false
  Type = 0
FEATURE [PartDesign::Fillet] Fillet071
  Base = -> Groove070 [Edge1]
  BaseFeature = -> Groove070
  Radius = 3
  SupportTransform = false
  Suppressed = false
  UseAllEdges = false
FEATURE [Sketcher::SketchObject] Sketch150
  ArcFitTolerance = 0
  AttachmentSupport = -> [XY_Plane047]
  FullyConstrained = true
  MakeInternals = false
  MapMode = 5
  sketch-geometry (2):
    g0: LineSegment StartX=0 StartY=-410 StartZ=0 EndX=0 EndY=-460 EndZ=0
    g1: ArcOfCircle CenterX=0 CenterY=-435 CenterZ=0 NormalX=0 NormalY=0 NormalZ=1 AngleXU=0 Radius=25 StartAngle=4.71239 EndAngle=7.85398
  constraints (7):
    c: Vertical(g0)
    c: PointOnObject(g1,g0)
    c: Coincident(g1,g0)
    c: Coincident(g1,g0)
    c: PointOnObject(g1,g-2)
    c: DistanceY(g1,g-1) = 435
    c: Radius(g1) = 25
FEATURE [PartDesign::Groove] Groove071  label="L Ankle cut001"
  Angle = 360
  Angle2 = 60
  Axis = (0,1,0)
  Base = (0,0,0)
  BaseFeature = -> Fillet071
  Profile = -> Sketch150
  ReferenceAxis = -> Sketch150 [V_Axis]
  Suppressed = false
  Type = 0
FEATURE [PartDesign::Fillet] Fillet072
  Base = -> Groove071 [Edge3]
  BaseFeature = -> Groove071
  Radius = 3
  SupportTransform = false
  Suppressed = false
  UseAllEdges = false
FEATURE [PartDesign::Revolution] Revolution078  label="L Ankle001"
  Angle = 360
  Angle2 = 60
  Axis = (0,1,0)
  Base = (0,0,0)
  BaseFeature = -> Fillet072
  Profile = -> Sketch150
  ReferenceAxis = -> Sketch150 [V_Axis]
  Reversed = true
  Suppressed = false
  Type = 0
FEATURE [PartDesign::Body] Body044  label="Left Shin001"
  AllowCompound = false
  Group = -> [Sketch148,Revolution077,Sketch149,Groove070,Fillet071,Sketch150,Groove071,Fillet072,Revolution078,Local_CS076,Local_CS077]
  Origin = -> Origin047
  Placement = pos=(75,496.571,-20.7032) rot=(1,0,0;0.10472rad)
  Tip = -> Revolution078
FEATURE [Sketcher::SketchObject] Sketch151
  ArcFitTolerance = 0
  AttachmentSupport = -> [YZ_Plane048]
  FullyConstrained = true
  MakeInternals = false
  MapMode = 5
  Placement = pos=(0,0,0) rot=(0.57735,0.57735,0.57735;2.0944rad)
  sketch-geometry (18):
    g0: LineSegment StartX=-62 StartY=180 StartZ=0 EndX=-62 EndY=-40 EndZ=0
    g1-g9: Circle [constr] x9 (B-spline internal-alignment scaffolding for g10; pole/knot coordinates omitted)
    g10: BSplineCurve PolesCount=9 KnotsCount=7 Degree=3 IsPeriodic=0
    g11-g17: GeomPoint [constr] x7 (B-spline internal-alignment scaffolding for g10; pole/knot coordinates omitted)
  constraints (13):
    c: Vertical(g0)
    c: DistanceX(g0,g-1) = 62
    c: DistanceY(g0,g-1) = 40
    c: DistanceY(g0,g0) = 220
    c: Weight(g1) = 1
    c: Coincident(g10,g0)
    c: Equal(g1, g2-g9) x8
    c: Coincident(g10,g0)
    c: InternalAlignment(g1-g9 -> g10) x9
    c: InternalAlignment(g11-g17 -> g10) x7
    c: Horizontal(g0,g8)
    c: Horizontal(g0,g2)
    c: Block(g10)
FEATURE [PartDesign::Pad] Pad004  label="L foot main body001"
  Direction = (1,0,0)
  Length = 100
  Length2 = 10
  Midplane = true
  Placement = pos=(0,0,0) rot=(1,1,1;2.0944rad)
  Profile = -> Sketch151
  ReferenceAxis = -> Sketch151 [N_Axis]
  Suppressed = false
  Type = 0
FEATURE [PartDesign::Fillet] Fillet073
  Base = -> Pad004 [Edge4,Edge6,Edge1,Edge5,Edge2]
  BaseFeature = -> Pad004
  Placement = pos=(0,0,0) rot=(1,1,1;2.0944rad)
  Radius = 6
  SupportTransform = false
  Suppressed = false
  UseAllEdges = false
FEATURE [PartDesign::CoordinateSystem] Local_CS078  label="Left Foot/Ankle001"
  AttacherType = Attacher::AttachEngine3D
  AttachmentSupport = -> [Pad004]
  MapMode = 2
  Placement = pos=(0,0,0) rot=(0.57735,0.57735,0.57735;2.0944rad)
FEATURE [Sketcher::SketchObject] Sketch152
  ArcFitTolerance = 0
  AttachmentSupport = -> [XY_Plane048]
  FullyConstrained = true
  MakeInternals = false
  MapMode = 5
  sketch-geometry (2):
    g0: LineSegment StartX=7.7e-15 StartY=25 StartZ=0 EndX=7.7e-15 EndY=-25 EndZ=0
    g1: ArcOfCircle CenterX=0 CenterY=0 CenterZ=0 NormalX=0 NormalY=0 NormalZ=1 AngleXU=0 Radius=25 StartAngle=4.71239 EndAngle=7.85398
  constraints (6):
    c: Vertical(g0)
    c: PointOnObject(g1,g0)
    c: Coincident(g1,g0)
    c: Coincident(g1,g0)
    c: Coincident(g1,g-1)
    c: Radius(g1) = 25
FEATURE [PartDesign::Groove] Groove072  label="Ankle cut004"
  Angle = 360
  Angle2 = 60
  Axis = (0,1,0)
  Base = (0,0,0)
  BaseFeature = -> Fillet073
  Placement = pos=(0,0,0) rot=(1,1,1;2.0944rad)
  Profile = -> Sketch152
  ReferenceAxis = -> Sketch152 [V_Axis]
  Suppressed = false
  Type = 0
FEATURE [PartDesign::Fillet] Fillet074
  Base = -> Groove072 [Edge20,Edge19]
  BaseFeature = -> Groove072
  Placement = pos=(0,0,0) rot=(1,1,1;2.0944rad)
  Radius = 3
  SupportTransform = false
  Suppressed = false
  UseAllEdges = false
FEATURE [PartDesign::Body] Body045  label="Left foot001"
  AllowCompound = false
  Group = -> [Sketch151,Pad004,Fillet073,Sketch152,Groove072,Fillet074,Local_CS078]
  Origin = -> Origin048
  Placement = pos=(75,63.9536,-66.1731) rot=(0,0,1;0rad)
  Tip = -> Fillet074
FEATURE [Sketcher::SketchObject] Sketch153
  ArcFitTolerance = 0
  AttachmentSupport = -> [XY_Plane049]
  FullyConstrained = true
  MakeInternals = false
  MapMode = 5
  sketch-geometry (14):
    g0: LineSegment StartX=0 StartY=-29.246 StartZ=0 EndX=0 EndY=-395.97 EndZ=0
    g1-g7: Circle [constr] x7 (B-spline internal-alignment scaffolding for g8; pole/knot coordinates omitted)
    g8: BSplineCurve PolesCount=7 KnotsCount=5 Degree=3 IsPeriodic=0
    g9-g13: GeomPoint [constr] x5 (B-spline internal-alignment scaffolding for g8; pole/knot coordinates omitted)
  constraints (11):
    c: PointOnObject(g0,g-2)
    c: Vertical(g0)
    c: Weight(g1) = 1
    c: Coincident(g8,g0)
    c: Equal(g1, g2-g7) x6
    c: Coincident(g8,g0)
    c: InternalAlignment(g1-g7 -> g8) x7
    c: InternalAlignment(g9-g13 -> g8) x5
    c: Horizontal(g0,g6)
    c: Horizontal(g0,g2)
    c: Block(g8)
FEATURE [PartDesign::Revolution] Revolution079  label="R Thigh main body001"
  Angle = 360
  Angle2 = 60
  Axis = (0,1,0)
  Base = (0,0,0)
  Profile = -> Sketch153
  ReferenceAxis = -> Sketch153 [V_Axis]
  Reversed = true
  Suppressed = false
  Type = 0
FEATURE [PartDesign::CoordinateSystem] Local_CS079  label="Right Thigh/Big joint LCS001"
  AttacherType = Attacher::AttachEngine3D
  AttachmentSupport = -> [Revolution079]
  MapMode = 2
FEATURE [PartDesign::CoordinateSystem] Local_CS080  label="Right Thigh/Knee LCS001"
  AttacherType = Attacher::AttachEngine3D
  AttachmentOffset = pos=(0,-403,0) rot=(0,0,1;0rad)
  AttachmentSupport = -> [Revolution079]
  MapMode = 2
  Placement = pos=(0,-403,0) rot=(0,0,1;0rad)
FEATURE [Sketcher::SketchObject] Sketch154
  ArcFitTolerance = 0
  AttachmentSupport = -> [XY_Plane049]
  FullyConstrained = true
  MakeInternals = false
  MapMode = 5
  sketch-geometry (2):
    g0: LineSegment StartX=1.84e-14 StartY=60 StartZ=0 EndX=1.84e-14 EndY=-60 EndZ=0
    g1: ArcOfCircle CenterX=0 CenterY=0 CenterZ=0 NormalX=0 NormalY=0 NormalZ=1 AngleXU=0 Radius=60 StartAngle=4.71239 EndAngle=7.85398
  constraints (6):
    c: Vertical(g0)
    c: PointOnObject(g1,g0)
    c: Coincident(g1,g0)
    c: Coincident(g1,g0)
    c: Coincident(g1,g-1)
    c: Radius(g1) = 60
FEATURE [PartDesign::Groove] Groove073  label="R Big joint001"
  Angle = 360
  Angle2 = 60
  Axis = (0,1,0)
  Base = (0,0,0)
  BaseFeature = -> Revolution079
  Profile = -> Sketch154
  ReferenceAxis = -> Sketch154 [V_Axis]
  Suppressed = false
  Type = 0
FEATURE [PartDesign::Fillet] Fillet075
  Base = -> Groove073 [Edge1]
  BaseFeature = -> Groove073
  Radius = 6
  SupportTransform = false
  Suppressed = false
  UseAllEdges = false
FEATURE [Sketcher::SketchObject] Sketch155
  ArcFitTolerance = 0
  AttachmentSupport = -> [XY_Plane049]
  FullyConstrained = true
  MakeInternals = false
  MapMode = 5
  sketch-geometry (2):
    g0: LineSegment StartX=1.07e-14 StartY=-368 StartZ=0 EndX=1.07e-14 EndY=-438 EndZ=0
    g1: ArcOfCircle CenterX=0 CenterY=-403 CenterZ=0 NormalX=0 NormalY=0 NormalZ=1 AngleXU=0 Radius=35 StartAngle=4.71239 EndAngle=7.85398
  constraints (7):
    c: Vertical(g0)
    c: PointOnObject(g1,g0)
    c: Coincident(g1,g0)
    c: Coincident(g1,g0)
    c: PointOnObject(g1,g-2)
    c: DistanceY(g1,g-1) = 403
    c: Radius(g1) = 35
FEATURE [PartDesign::Groove] Groove074  label="R Knee cut001"
  Angle = 360
  Angle2 = 60
  Axis = (0,1,0)
  Base = (0,0,0)
  BaseFeature = -> Fillet075
  Profile = -> Sketch155
  ReferenceAxis = -> Sketch155 [V_Axis]
  Suppressed = false
  Type = 0
FEATURE [PartDesign::Fillet] Fillet076
  Base = -> Groove074 [Edge1]
  BaseFeature = -> Groove074
  Radius = 3
  SupportTransform = false
  Suppressed = false
  UseAllEdges = false
FEATURE [PartDesign::Revolution] Revolution080  label="R Knee001"
  Angle = 360
  Angle2 = 60
  Axis = (0,1,0)
  Base = (0,0,0)
  BaseFeature = -> Fillet076
  Profile = -> Sketch155
  ReferenceAxis = -> Sketch155 [V_Axis]
  Reversed = true
  Suppressed = false
  Type = 0
FEATURE [PartDesign::Body] Body046  label="Right Thigh001"
  AllowCompound = false
  Group = -> [Sketch153,Revolution079,Sketch154,Groove073,Fillet075,Sketch155,Groove074,Fillet076,Revolution080,Local_CS079,Local_CS080]
  Origin = -> Origin049
  Placement = pos=(-75,899.018,0.388141) rot=(-1,0,0;0.069813rad)
  Tip = -> Revolution080
FEATURE [Sketcher::SketchObject] Sketch156
  ArcFitTolerance = 0
  AttachmentSupport = -> [XY_Plane050]
  FullyConstrained = true
  MakeInternals = false
  MapMode = 5
  sketch-geometry (14):
    g0: LineSegment StartX=0 StartY=0 StartZ=0 EndX=0 EndY=-428.766 EndZ=0
    g1-g7: Circle [constr] x7 (B-spline internal-alignment scaffolding for g8; pole/knot coordinates omitted)
    g8: BSplineCurve PolesCount=7 KnotsCount=5 Degree=3 IsPeriodic=0
    g9-g13: GeomPoint [constr] x5 (B-spline internal-alignment scaffolding for g8; pole/knot coordinates omitted)
  constraints (9):
    c: Vertical(g0)
    c: PointOnObject(g0,g-2)
    c: Weight(g1) = 1
    c: Coincident(g8,g0)
    c: Equal(g1, g2-g7) x6
    c: Coincident(g8,g0)
    c: InternalAlignment(g1-g7 -> g8) x7
    c: InternalAlignment(g9-g13 -> g8) x5
    c: Block(g8)
FEATURE [PartDesign::Revolution] Revolution081  label="R Shin main body001"
  Angle = 360
  Angle2 = 60
  Axis = (0,1,0)
  Base = (0,0,0)
  Profile = -> Sketch156
  ReferenceAxis = -> Sketch156 [V_Axis]
  Reversed = true
  Suppressed = false
  Type = 0
FEATURE [PartDesign::CoordinateSystem] Local_CS081  label="Right Shin/Knee001"
  AttacherType = Attacher::AttachEngine3D
  AttachmentSupport = -> [Revolution081]
  MapMode = 2
FEATURE [PartDesign::CoordinateSystem] Local_CS082  label="Right Shin/Ankle001"
  AttacherType = Attacher::AttachEngine3D
  AttachmentOffset = pos=(0,-435,0) rot=(0,0,1;0rad)
  AttachmentSupport = -> [Revolution081]
  MapMode = 2
  Placement = pos=(0,-435,0) rot=(0,0,1;0rad)
FEATURE [Sketcher::SketchObject] Sketch157
  ArcFitTolerance = 0
  AttachmentSupport = -> [XY_Plane050]
  FullyConstrained = true
  MakeInternals = false
  MapMode = 5
  sketch-geometry (2):
    g0: LineSegment StartX=1.07e-14 StartY=35 StartZ=0 EndX=1.07e-14 EndY=-35 EndZ=0
    g1: ArcOfCircle CenterX=0 CenterY=0 CenterZ=0 NormalX=0 NormalY=0 NormalZ=1 AngleXU=0 Radius=35 StartAngle=4.71239 EndAngle=7.85398
  constraints (6):
    c: PointOnObject(g1,g0)
    c: Coincident(g1,g0)
    c: Coincident(g1,g0)
    c: Vertical(g0)
    c: Coincident(g1,g-1)
    c: Radius(g1) = 35
FEATURE [PartDesign::Groove] Groove075  label="R knee cut001"
  Angle = 360
  Angle2 = 60
  Axis = (0,1,0)
  Base = (0,0,0)
  BaseFeature = -> Revolution081
  Profile = -> Sketch157
  ReferenceAxis = -> Sketch157 [V_Axis]
  Suppressed = false
  Type = 0
FEATURE [PartDesign::Fillet] Fillet077
  Base = -> Groove075 [Edge1]
  BaseFeature = -> Groove075
  Radius = 3
  SupportTransform = false
  Suppressed = false
  UseAllEdges = false
FEATURE [Sketcher::SketchObject] Sketch158
  ArcFitTolerance = 0
  AttachmentSupport = -> [XY_Plane050]
  FullyConstrained = true
  MakeInternals = false
  MapMode = 5
  sketch-geometry (2):
    g0: LineSegment StartX=-4.6e-15 StartY=-410 StartZ=0 EndX=-4.6e-15 EndY=-460 EndZ=0
    g1: ArcOfCircle CenterX=0 CenterY=-435 CenterZ=0 NormalX=0 NormalY=0 NormalZ=1 AngleXU=0 Radius=25 StartAngle=4.71239 EndAngle=7.85398
  constraints (7):
    c: Vertical(g0)
    c: PointOnObject(g1,g0)
    c: Coincident(g1,g0)
    c: Coincident(g1,g0)
    c: PointOnObject(g1,g-2)
    c: DistanceY(g1,g-1) = 435
    c: Radius(g1) = 25
FEATURE [PartDesign::Groove] Groove076  label="R Ankle cut001"
  Angle = 360
  Angle2 = 60
  Axis = (0,1,0)
  Base = (0,0,0)
  BaseFeature = -> Fillet077
  Profile = -> Sketch158
  ReferenceAxis = -> Sketch158 [V_Axis]
  Suppressed = false
  Type = 0
FEATURE [PartDesign::Fillet] Fillet078
  Base = -> Groove076 [Edge3]
  BaseFeature = -> Groove076
  Radius = 3
  SupportTransform = false
  Suppressed = false
  UseAllEdges = false
FEATURE [PartDesign::Revolution] Revolution082  label="R Ankle001"
  Angle = 360
  Angle2 = 60
  Axis = (0,1,0)
  Base = (0,0,0)
  BaseFeature = -> Fillet078
  Profile = -> Sketch158
  ReferenceAxis = -> Sketch158 [V_Axis]
  Reversed = true
  Suppressed = false
  Type = 0
FEATURE [PartDesign::Body] Body047  label="Right Shin001"
  AllowCompound = false
  Group = -> [Sketch156,Revolution081,Sketch157,Groove075,Fillet077,Sketch158,Groove076,Fillet078,Revolution082,Local_CS081,Local_CS082]
  Origin = -> Origin050
  Placement = pos=(-75,497,28.5) rot=(0,0,1;0rad)
  Tip = -> Revolution082
FEATURE [Sketcher::SketchObject] Sketch159
  ArcFitTolerance = 0
  AttachmentSupport = -> [YZ_Plane051]
  FullyConstrained = true
  MakeInternals = false
  MapMode = 5
  Placement = pos=(0,0,0) rot=(0.57735,0.57735,0.57735;2.0944rad)
  sketch-geometry (18):
    g0: LineSegment StartX=-62 StartY=180 StartZ=0 EndX=-62 EndY=-40 EndZ=0
    g1-g9: Circle [constr] x9 (B-spline internal-alignment scaffolding for g10; pole/knot coordinates omitted)
    g10: BSplineCurve PolesCount=9 KnotsCount=7 Degree=3 IsPeriodic=0
    g11-g17: GeomPoint [constr] x7 (B-spline internal-alignment scaffolding for g10; pole/knot coordinates omitted)
  constraints (13):
    c: Vertical(g0)
    c: DistanceX(g0,g-1) = 62
    c: DistanceY(g0,g-1) = 40
    c: DistanceY(g0,g0) = 220
    c: Weight(g1) = 1
    c: Coincident(g10,g0)
    c: Equal(g1, g2-g9) x8
    c: Coincident(g10,g0)
    c: InternalAlignment(g1-g9 -> g10) x9
    c: InternalAlignment(g11-g17 -> g10) x7
    c: Horizontal(g0,g8)
    c: Horizontal(g0,g2)
    c: Block(g10)
FEATURE [PartDesign::Pad] Pad005  label="R foot main body001"
  Direction = (1,0,0)
  Length = 100
  Length2 = 10
  Midplane = true
  Placement = pos=(0,0,0) rot=(1,1,1;2.0944rad)
  Profile = -> Sketch159
  ReferenceAxis = -> Sketch159 [N_Axis]
  Suppressed = false
  Type = 0
FEATURE [PartDesign::Fillet] Fillet079
  Base = -> Pad005 [Edge4,Edge6,Edge1,Edge5,Edge2]
  BaseFeature = -> Pad005
  Placement = pos=(0,0,0) rot=(1,1,1;2.0944rad)
  Radius = 6
  SupportTransform = false
  Suppressed = false
  UseAllEdges = false
FEATURE [PartDesign::CoordinateSystem] Local_CS083  label="Right Foot/Ankle001"
  AttacherType = Attacher::AttachEngine3D
  AttachmentSupport = -> [Pad005]
  MapMode = 2
  Placement = pos=(0,0,0) rot=(0.57735,0.57735,0.57735;2.0944rad)
FEATURE [Sketcher::SketchObject] Sketch160
  ArcFitTolerance = 0
  AttachmentSupport = -> [XY_Plane051]
  FullyConstrained = true
  MakeInternals = false
  MapMode = 5
  sketch-geometry (2):
    g0: LineSegment StartX=7.7e-15 StartY=25 StartZ=0 EndX=7.7e-15 EndY=-25 EndZ=0
    g1: ArcOfCircle CenterX=0 CenterY=0 CenterZ=0 NormalX=0 NormalY=0 NormalZ=1 AngleXU=0 Radius=25 StartAngle=4.71239 EndAngle=7.85398
  constraints (6):
    c: Vertical(g0)
    c: PointOnObject(g1,g0)
    c: Coincident(g1,g0)
    c: Coincident(g1,g0)
    c: Coincident(g1,g-1)
    c: Radius(g1) = 25
FEATURE [PartDesign::Groove] Groove077  label="Ankle cut001"
  Angle = 360
  Angle2 = 60
  Axis = (0,1,0)
  Base = (0,0,0)
  BaseFeature = -> Fillet079
  Placement = pos=(0,0,0) rot=(1,1,1;2.0944rad)
  Profile = -> Sketch160
  ReferenceAxis = -> Sketch160 [V_Axis]
  Suppressed = false
  Type = 0
FEATURE [PartDesign::Fillet] Fillet080
  Base = -> Groove077 [Edge20,Edge19]
  BaseFeature = -> Groove077
  Placement = pos=(0,0,0) rot=(1,1,1;2.0944rad)
  Radius = 3
  SupportTransform = false
  Suppressed = false
  UseAllEdges = false
FEATURE [PartDesign::Body] Body048  label="Right foot001"
  AllowCompound = false
  Group = -> [Sketch159,Pad005,Fillet079,Sketch160,Groove077,Fillet080,Local_CS083]
  Origin = -> Origin051
  Placement = pos=(-75,62,28.5) rot=(0,0,1;0rad)
  Tip = -> Fillet080
FEATURE [App::Part] Part_003  label="Mannequin_mp-dummy-1850mm-standing-007"
  Group = -> [LCS_001,Body034,Body035,Body036,Body037,Body038,Body039,Body040,Body041,Body042,Body043,Body044,Body045,Body046,Body047,Body048]
  Origin = -> Origin036
  Placement = pos=(-7959.1,16272,-3.6131e-12) rot=(-0.281085,0.678598,0.678598;3.68962rad)
FEATURE [PartDesign::CoordinateSystem] LCS_002
  AttacherType = Attacher::AttachEngine3D
  AttachmentSupport = -> [X_Axis052]
  MapMode = 2
FEATURE [Sketcher::SketchObject] Sketch161
  ArcFitTolerance = 0
  AttachmentSupport = -> [XY_Plane053]
  FullyConstrained = true
  MakeInternals = false
  MapMode = 5
  sketch-geometry (14):
    g0: LineSegment StartX=0 StartY=0 StartZ=0 EndX=0 EndY=296.299 EndZ=0
    g1-g7: Circle [constr] x7 (B-spline internal-alignment scaffolding for g8; pole/knot coordinates omitted)
    g8: BSplineCurve PolesCount=7 KnotsCount=5 Degree=3 IsPeriodic=0
    g9-g13: GeomPoint [constr] x5 (B-spline internal-alignment scaffolding for g8; pole/knot coordinates omitted)
  constraints (12):
    c: Coincident(g0,g-1)
    c: Vertical(g0)
    c: Weight(g1) = 1
    c: Coincident(g8,g0)
    c: Equal(g1, g2-g7) x6
    c: Coincident(g8,g0)
    c: InternalAlignment(g1-g7 -> g8) x7
    c: InternalAlignment(g9-g13 -> g8) x5
    c: Horizontal(g0,g2)
    c: Horizontal(g0,g6)
    c: Block(g0)
    c: Block(g8)
FEATURE [PartDesign::Revolution] Revolution083
  Angle = 360
  Angle2 = 60
  Axis = (0,1,0)
  Base = (0,0,0)
  Profile = -> Sketch161
  ReferenceAxis = -> Sketch161 [V_Axis]
  Reversed = true
  Suppressed = false
  Type = 0
FEATURE [PartDesign::CoordinateSystem] Local_CS089  label="Head/Neck LCS002"
  AttacherType = Attacher::AttachEngine3D
  AttachmentSupport = -> [Revolution083]
  MapMode = 2
FEATURE [Sketcher::SketchObject] Sketch162
  ArcFitTolerance = 0
  AttachmentSupport = -> [XY_Plane054]
  FullyConstrained = true
  MakeInternals = false
  MapMode = 5
  sketch-geometry (18):
    g0: LineSegment StartX=0 StartY=322.019 StartZ=0 EndX=0 EndY=20.3719 EndZ=0
    g1-g9: Circle [constr] x9 (B-spline internal-alignment scaffolding for g10; pole/knot coordinates omitted)
    g10: BSplineCurve PolesCount=9 KnotsCount=7 Degree=3 IsPeriodic=0
    g11-g17: GeomPoint [constr] x7 (B-spline internal-alignment scaffolding for g10; pole/knot coordinates omitted)
  constraints (12):
    c: Vertical(g0)
    c: PointOnObject(g0,g-2)
    c: Weight(g1) = 1
    c: Coincident(g10,g0)
    c: Equal(g1, g2-g9) x8
    c: Coincident(g10,g0)
    c: InternalAlignment(g1-g9 -> g10) x9
    c: InternalAlignment(g11-g17 -> g10) x7
    c: Horizontal(g0,g2)
    c: Horizontal(g0,g8)
    c: Block(g0)
    c: Block(g10)
FEATURE [PartDesign::Revolution] Revolution084  label="Base shape002"
  Angle = 360
  Angle2 = 60
  Axis = (0,1,0)
  Base = (0,0,0)
  Profile = -> Sketch162
  ReferenceAxis = -> Sketch162 [V_Axis]
  Reversed = true
  Suppressed = false
  Type = 0
FEATURE [PartDesign::CoordinateSystem] Local_CS084  label="Chest/Neck LCS002"
  AttacherType = Attacher::AttachEngine3D
  AttachmentOffset = pos=(354,0,0) rot=(0,0,1;0rad)
  AttachmentSupport = -> [Revolution084]
  MapMode = 4
  Placement = pos=(0,354,0) rot=(0.57735,0.57735,0.57735;2.0944rad)
FEATURE [PartDesign::CoordinateSystem] Local_CS085  label="Chest/Waist LCS002"
  AttacherType = Attacher::AttachEngine3D
  AttachmentSupport = -> [Revolution084]
  MapMode = 2
FEATURE [PartDesign::CoordinateSystem] Local_CS086  label="Chest/Left shoulder LCS002"
  AttacherType = Attacher::AttachEngine3D
  AttachmentOffset = pos=(184,257,0) rot=(0,0,1;0rad)
  AttachmentSupport = -> [Revolution084]
  MapMode = 2
  Placement = pos=(184,257,0) rot=(0,0,1;0rad)
FEATURE [PartDesign::CoordinateSystem] Local_CS087  label="Chest/Right shoulder LCS002"
  AttacherType = Attacher::AttachEngine3D
  AttachmentOffset = pos=(-184,257,0) rot=(0,0,1;0rad)
  AttachmentSupport = -> [Revolution084]
  MapMode = 2
  Placement = pos=(-184,257,0) rot=(0,0,1;0rad)
FEATURE [Sketcher::SketchObject] Sketch163
  ArcFitTolerance = 0
  AttachmentSupport = -> [XY_Plane053]
  FullyConstrained = true
  MakeInternals = false
  MapMode = 5
  sketch-geometry (2):
    g0: LineSegment StartX=-1.01e-14 StartY=55 StartZ=0 EndX=-1.01e-14 EndY=-55 EndZ=0
    g1: ArcOfCircle CenterX=0 CenterY=0 CenterZ=0 NormalX=0 NormalY=0 NormalZ=1 AngleXU=0 Radius=55 StartAngle=4.71239 EndAngle=7.85398
  constraints (6):
    c: Vertical(g0)
    c: Coincident(g1,g-1)
    c: Coincident(g1,g0)
    c: Coincident(g1,g0)
    c: PointOnObject(g0,g-2)
    c: Radius(g1) = 55
FEATURE [PartDesign::Groove] Groove078
  Angle = 360
  Angle2 = 60
  Axis = (0,1,0)
  Base = (0,0,0)
  BaseFeature = -> Revolution083
  Profile = -> Sketch163
  ReferenceAxis = -> Sketch163 [V_Axis]
  Suppressed = false
  Type = 0
FEATURE [Sketcher::SketchObject] Sketch164
  ArcFitTolerance = 0
  AttachmentSupport = -> [XZ_Plane053]
  FullyConstrained = true
  MakeInternals = false
  MapMode = 5
  Placement = pos=(0,0,0) rot=(1,0,0;1.5708rad)
  sketch-geometry (5):
    g0: LineSegment StartX=-125 StartY=125 StartZ=0 EndX=125 EndY=125 EndZ=0
    g1: LineSegment StartX=125 StartY=125 StartZ=0 EndX=125 EndY=50 EndZ=0
    g2: LineSegment StartX=125 StartY=50 StartZ=0 EndX=0 EndY=75 EndZ=0
    g3: LineSegment StartX=0 StartY=75 StartZ=0 EndX=-125 EndY=50 EndZ=0
    g4: LineSegment StartX=-125 StartY=50 StartZ=0 EndX=-125 EndY=125 EndZ=0
  constraints (15):
    c: Horizontal(g0)
    c: Coincident(g0,g1)
    c: Vertical(g1)
    c: Coincident(g1,g2)
    c: Coincident(g2,g3)
    c: Coincident(g3,g4)
    c: Coincident(g4,g0)
    c: Vertical(g4)
    c: Horizontal(g3,g1)
    c: PointOnObject(g2,g-2)
    c: DistanceX(g0,g0) = 250
    c: DistanceX(g0,g-1) = 125
    c: DistanceY(g4,g4) = 75
    c: DistanceY(g-1,g2) = 75
    c: DistanceY(g-1,g0) = 125
FEATURE [PartDesign::Pocket] Pocket027
  BaseFeature = -> Groove078
  Direction = (0,1,0.05)
  Length = 300
  Length2 = 5
  Profile = -> Sketch164
  ReferenceAxis = -> Sketch164 [N_Axis]
  Suppressed = false
  Type = 0
  UseCustomVector = true
FEATURE [PartDesign::Fillet] Fillet081
  Base = -> Pocket027 [Edge3]
  BaseFeature = -> Pocket027
  Radius = 3
  SupportTransform = false
  Suppressed = false
  UseAllEdges = false
FEATURE [PartDesign::Body] Body049  label="Head002"
  AllowCompound = false
  Group = -> [Sketch161,Revolution083,Sketch163,Groove078,Sketch164,Pocket027,Fillet081,Local_CS089]
  Origin = -> Origin053
  Placement = pos=(0,1551.02,0.388141) rot=(0,0,1;0rad)
  Tip = -> Fillet081
FEATURE [Sketcher::SketchObject] Sketch165
  ArcFitTolerance = 0
  AttachmentSupport = -> [YZ_Plane054]
  FullyConstrained = true
  MakeInternals = false
  MapMode = 5
  Placement = pos=(0,0,0) rot=(0.57735,0.57735,0.57735;2.0944rad)
  sketch-geometry (6):
    g0: LineSegment StartX=0 StartY=76.0576 StartZ=0 EndX=164.705 EndY=107.04 EndZ=0
    g1: LineSegment StartX=230.198 StartY=103.732 StartZ=0 EndX=327.121 EndY=75.1407 EndZ=0
    g2: LineSegment StartX=327.121 StartY=75.1407 StartZ=0 EndX=327.121 EndY=181.805 EndZ=0
    g3: LineSegment StartX=327.121 StartY=181.805 StartZ=0 EndX=0 EndY=181.805 EndZ=0
    g4: LineSegment StartX=0 StartY=181.805 StartZ=0 EndX=0 EndY=76.0576 EndZ=0
    g5: ArcOfCircle CenterX=190.587 CenterY=-30.5467 CenterZ=0 NormalX=0 NormalY=0 NormalZ=1 AngleXU=0 Radius=140 StartAngle=1.28394 EndAngle=1.75673
  constraints (14):
    c: Coincident(g1,g2)
    c: Vertical(g2)
    c: Coincident(g2,g3)
    c: Horizontal(g3)
    c: Coincident(g3,g4)
    c: Coincident(g4,g0)
    c: Vertical(g4)
    c: PointOnObject(g3,g-2)
    c: Tangent(g1,g5) = 1.5708
    c: Tangent(g0,g5) = 1.5708
    c: Radius(g5) = 140
    c: Block(g0)
    c: Block(g1)
    c: Block(g3)
FEATURE [PartDesign::Pocket] Pocket028  label="Front cut002"
  BaseFeature = -> Revolution084
  Direction = (-1,0,0)
  Length = 5
  Length2 = 5
  Midplane = true
  Profile = -> Sketch165
  ReferenceAxis = -> Sketch165 [N_Axis]
  Suppressed = false
  Type = 1
FEATURE [Sketcher::SketchObject] Sketch166
  ArcFitTolerance = 0
  AttachmentSupport = -> [YZ_Plane054]
  FullyConstrained = true
  MakeInternals = false
  MapMode = 5
  Placement = pos=(0,0,0) rot=(0.57735,0.57735,0.57735;2.0944rad)
  sketch-geometry (8):
    g0: LineSegment StartX=0 StartY=-87.996 StartZ=0 EndX=81.1566 EndY=-77.888 EndZ=0
    g1: LineSegment StartX=139.259 StartY=-78.9913 StartZ=0 EndX=245.223 EndY=-96.2967 EndZ=0
    g2: LineSegment StartX=281.434 StartY=-93.8397 StartZ=0 EndX=341.01 EndY=-75.582 EndZ=0
    g3: LineSegment StartX=341.01 StartY=-75.582 StartZ=0 EndX=341.01 EndY=-197.004 EndZ=0
    g4: LineSegment StartX=341.01 StartY=-197.004 StartZ=0 EndX=0 EndY=-197.004 EndZ=0
    g5: LineSegment StartX=0 StartY=-197.004 StartZ=0 EndX=0 EndY=-87.996 EndZ=0
    g6: ArcOfCircle CenterX=106.373 CenterY=-280.353 CenterZ=0 NormalX=0 NormalY=0 NormalZ=1 AngleXU=0 Radius=204.029 StartAngle=1.40891 EndAngle=1.69471
    g7: ArcOfCircle CenterX=258.073 CenterY=-17.6116 CenterZ=0 NormalX=0 NormalY=0 NormalZ=1 AngleXU=0 Radius=79.7275 StartAngle=4.5505 EndAngle=5.00977
  constraints (16):
    c: Coincident(g2,g3)
    c: Coincident(g3,g4)
    c: Horizontal(g4)
    c: Coincident(g4,g5)
    c: Coincident(g5,g0)
    c: Vertical(g5)
    c: Vertical(g3)
    c: PointOnObject(g4,g-2)
    c: Tangent(g1,g6) = 1.5708
    c: Tangent(g0,g6) = 1.5708
    c: Tangent(g1,g7) = -1.5708
    c: Tangent(g2,g7) = -1.5708
    c: Block(g0)
    c: Block(g2)
    c: Block(g1)
    c: Block(g4)
FEATURE [PartDesign::Pocket] Pocket029  label="Back cut002"
  BaseFeature = -> Pocket028
  Direction = (-1,0,0)
  Length = 5
  Length2 = 5
  Midplane = true
  Profile = -> Sketch166
  ReferenceAxis = -> Sketch166 [N_Axis]
  Suppressed = false
  Type = 1
FEATURE [Sketcher::SketchObject] Sketch167
  ArcFitTolerance = 0
  AttachmentSupport = -> [XY_Plane054]
  FullyConstrained = true
  MakeInternals = false
  MapMode = 5
  sketch-geometry (2):
    g0: LineSegment StartX=1.68e-14 StartY=409 StartZ=0 EndX=1.68e-14 EndY=299 EndZ=0
    g1: ArcOfCircle CenterX=0 CenterY=354 CenterZ=0 NormalX=0 NormalY=0 NormalZ=1 AngleXU=0 Radius=55 StartAngle=4.71239 EndAngle=7.85398
  constraints (7):
    c: Vertical(g0)
    c: PointOnObject(g1,g0)
    c: Coincident(g1,g0)
    c: PointOnObject(g1,g-2)
    c: Coincident(g1,g0)
    c: Radius(g1) = 55
    c: DistanceY(g-1,g1) = 354
FEATURE [PartDesign::Groove] Groove079  label="Neck cut002"
  Angle = 360
  Angle2 = 60
  Axis = (0,1,0)
  Base = (0,0,0)
  BaseFeature = -> Pocket029
  Profile = -> Sketch167
  ReferenceAxis = -> Sketch167 [V_Axis]
  Suppressed = false
  Type = 0
FEATURE [PartDesign::Fillet] Fillet082  label="Neck fillet002"
  Base = -> Groove079 [Edge1]
  BaseFeature = -> Groove079
  Radius = 6
  SupportTransform = false
  Suppressed = false
  UseAllEdges = false
FEATURE [Sketcher::SketchObject] Sketch168
  ArcFitTolerance = 0
  AttachmentSupport = -> [XY_Plane054]
  FullyConstrained = true
  MakeInternals = false
  MapMode = 5
  sketch-geometry (2):
    g0: LineSegment StartX=-1.38e-14 StartY=75 StartZ=0 EndX=-1.38e-14 EndY=-75 EndZ=0
    g1: ArcOfCircle CenterX=0 CenterY=0 CenterZ=0 NormalX=0 NormalY=0 NormalZ=1 AngleXU=0 Radius=75 StartAngle=4.71239 EndAngle=7.85398
  constraints (6):
    c: Vertical(g0)
    c: Coincident(g1,g-1)
    c: Coincident(g1,g0)
    c: Coincident(g1,g0)
    c: PointOnObject(g0,g-2)
    c: Radius(g1) = 75
FEATURE [PartDesign::Groove] Groove080  label="Waist cut002"
  Angle = 360
  Angle2 = 60
  Axis = (0,1,0)
  Base = (0,0,0)
  BaseFeature = -> Fillet082
  Profile = -> Sketch168
  ReferenceAxis = -> Sketch168 [V_Axis]
  Suppressed = false
  Type = 0
FEATURE [PartDesign::Fillet] Fillet083  label="Waist fillet002"
  Base = -> Groove080 [Edge3]
  BaseFeature = -> Groove080
  Radius = 5
  SupportTransform = false
  Suppressed = false
  UseAllEdges = false
FEATURE [Sketcher::SketchObject] Sketch169
  ArcFitTolerance = 0
  AttachmentSupport = -> [XY_Plane054]
  FullyConstrained = true
  MakeInternals = false
  MapMode = 5
  sketch-geometry (4):
    g0: LineSegment StartX=124 StartY=257 StartZ=0 EndX=244 EndY=257 EndZ=0
    g1: ArcOfCircle CenterX=184 CenterY=257 CenterZ=0 NormalX=0 NormalY=0 NormalZ=1 AngleXU=0 Radius=60 StartAngle=0 EndAngle=3.14159
    g2: LineSegment StartX=-244 StartY=257 StartZ=0 EndX=-124 EndY=257 EndZ=0
    g3: ArcOfCircle CenterX=-184 CenterY=257 CenterZ=0 NormalX=0 NormalY=0 NormalZ=1 AngleXU=0 Radius=60 StartAngle=4e-16 EndAngle=3.14159
  constraints (14):
    c: Horizontal(g0)
    c: PointOnObject(g1,g0)
    c: Coincident(g1,g0)
    c: Coincident(g1,g0)
    c: DistanceY(g-1,g1) = 257
    c: Radius(g1) = 60
    c: DistanceX(g-1,g1) = 184
    c: Horizontal(g2)
    c: PointOnObject(g3,g2)
    c: Coincident(g3,g2)
    c: Coincident(g3,g2)
    c: Horizontal(g2,g0)
    c: Radius(g3) = 60
    c: DistanceX(g3,g-1) = 184
FEATURE [PartDesign::Groove] Groove081  label="Shoulders cut002"
  Angle = 360
  Angle2 = 60
  Axis = (1,0,0)
  Base = (124,257,0)
  BaseFeature = -> Fillet083
  Profile = -> Sketch169
  ReferenceAxis = -> Sketch169 [Edge1]
  Suppressed = false
  Type = 0
FEATURE [PartDesign::Fillet] Fillet084  label="Shoulders fillet002"
  Base = -> Groove081 [Edge6,Edge3,Edge12,Edge13]
  BaseFeature = -> Groove081
  Radius = 6
  SupportTransform = false
  Suppressed = false
  UseAllEdges = false
FEATURE [PartDesign::Revolution] Revolution085  label="Neck add002"
  Angle = 360
  Angle2 = 60
  Axis = (0,1,0)
  Base = (0,0,0)
  BaseFeature = -> Fillet084
  Profile = -> Sketch167
  ReferenceAxis = -> Sketch167 [V_Axis]
  Reversed = true
  Suppressed = false
  Type = 0
FEATURE [PartDesign::Revolution] Revolution086  label="waist add002"
  Angle = 360
  Angle2 = 60
  Axis = (0,1,0)
  Base = (0,0,0)
  BaseFeature = -> Revolution085
  Profile = -> Sketch168
  ReferenceAxis = -> Sketch168 [V_Axis]
  Reversed = true
  Suppressed = false
  Type = 0
FEATURE [PartDesign::Revolution] Revolution087  label="Shoulders002"
  Angle = 360
  Angle2 = 60
  Axis = (1,0,0)
  Base = (-244,257,0)
  BaseFeature = -> Revolution086
  Profile = -> Sketch169
  ReferenceAxis = -> Sketch169 [Edge3]
  Suppressed = false
  Type = 0
FEATURE [PartDesign::Body] Body050  label="Chest002"
  AllowCompound = false
  Group = -> [Sketch162,Revolution084,Sketch165,Pocket028,Sketch166,Pocket029,Sketch167,Groove079,Fillet082,Sketch168,Groove080,Fillet083,Sketch169,Groove081,Fillet084,Revolution085,Revolution086,Revolution087,Local_CS084,Local_CS085,Local_CS086,Local_CS087]
  Origin = -> Origin054
  Placement = pos=(0,1197.02,0.388141) rot=(0,0,1;0rad)
  Tip = -> Revolution087
FEATURE [Sketcher::SketchObject] Sketch170
  ArcFitTolerance = 0
  AttachmentSupport = -> [XY_Plane055]
  FullyConstrained = true
  MakeInternals = false
  MapMode = 5
  sketch-geometry (21):
    g0: LineSegment StartX=0 StartY=-29.4305 StartZ=0 EndX=0 EndY=-256.068 EndZ=0
    g1-g7: Circle [constr] x7 (B-spline internal-alignment scaffolding for g8; pole/knot coordinates omitted)
    g8: BSplineCurve PolesCount=7 KnotsCount=5 Degree=3 IsPeriodic=0
    g9-g13: GeomPoint [constr] x5 (B-spline internal-alignment scaffolding for g8; pole/knot coordinates omitted)
    g14-g17: Circle [constr] x4 (B-spline internal-alignment scaffolding for g18; pole/knot coordinates omitted)
    g18: BSplineCurve PolesCount=4 KnotsCount=2 Degree=3 IsPeriodic=0
    g19: GeomPoint [constr] X=118.087 Y=-247.149 Z=0
    g20: GeomPoint [constr] X=0 Y=-256.068 Z=0
  constraints (21):
    c: PointOnObject(g0,g-2)
    c: Vertical(g0)
    c: Weight(g1) = 1
    c: Coincident(g8,g0)
    c: Equal(g1, g2-g7) x6
    c: InternalAlignment(g1-g7 -> g8) x7
    c: InternalAlignment(g9-g13 -> g8) x5
    c: Weight(g14) = 1
    c: Coincident(g18,g8)
    c: Equal(g14,g15)
    c: Equal(g14,g16)
    c: Equal(g14,g17)
    c: Coincident(g18,g0)
    c: InternalAlignment(g14-g17 -> g18) x4
    c: InternalAlignment(g19,g18)
    c: InternalAlignment(g20,g18)
    c: Horizontal(g16,g0)
    c: Horizontal(g0,g2)
    c: Block(g0)
    c: Block(g8)
    c: Block(g18)
FEATURE [PartDesign::Revolution] Revolution088  label="Main body of hip002"
  Angle = 360
  Angle2 = 60
  Axis = (0,1,0)
  Base = (0,0,0)
  Profile = -> Sketch170
  ReferenceAxis = -> Sketch170 [V_Axis]
  Reversed = true
  Suppressed = false
  Type = 0
FEATURE [PartDesign::CoordinateSystem] Local_CS088  label="Hip/Waist LCS002"
  AttacherType = Attacher::AttachEngine3D
  AttachmentSupport = -> [Revolution088]
  MapMode = 2
FEATURE [PartDesign::CoordinateSystem] Local_CS090  label="Hip/Leg joint left002"
  AttacherType = Attacher::AttachEngine3D
  AttachmentOffset = pos=(75,-298,0) rot=(0,0,1;0rad)
  AttachmentSupport = -> [Revolution088]
  MapMode = 2
  Placement = pos=(75,-298,0) rot=(0,0,1;0rad)
FEATURE [PartDesign::CoordinateSystem] Local_CS091  label="Hip/Leg joint right002"
  AttacherType = Attacher::AttachEngine3D
  AttachmentOffset = pos=(-75,-298,0) rot=(0,0,1;0rad)
  AttachmentSupport = -> [Revolution088]
  MapMode = 2
  Placement = pos=(-75,-298,0) rot=(0,0,1;0rad)
FEATURE [Sketcher::SketchObject] Sketch171
  ArcFitTolerance = 0
  AttachmentSupport = -> [XY_Plane055]
  FullyConstrained = true
  MakeInternals = false
  MapMode = 5
  sketch-geometry (2):
    g0: LineSegment StartX=2.3e-14 StartY=75 StartZ=0 EndX=2.3e-14 EndY=-75 EndZ=0
    g1: ArcOfCircle CenterX=0 CenterY=0 CenterZ=0 NormalX=0 NormalY=0 NormalZ=1 AngleXU=0 Radius=75 StartAngle=4.71239 EndAngle=7.85398
  constraints (6):
    c: Vertical(g0)
    c: PointOnObject(g1,g0)
    c: Coincident(g1,g0)
    c: Coincident(g1,g0)
    c: Coincident(g1,g-1)
    c: Radius(g1) = 75
FEATURE [PartDesign::Groove] Groove082  label="Waist cut of hip002"
  Angle = 360
  Angle2 = 60
  Axis = (0,1,0)
  Base = (0,0,0)
  BaseFeature = -> Revolution088
  Profile = -> Sketch171
  ReferenceAxis = -> Sketch171 [V_Axis]
  Suppressed = false
  Type = 0
FEATURE [PartDesign::Fillet] Fillet085  label="waist002"
  Base = -> Groove082 [Edge4]
  BaseFeature = -> Groove082
  Radius = 6
  SupportTransform = false
  Suppressed = false
  UseAllEdges = false
FEATURE [Sketcher::SketchObject] Sketch172
  ArcFitTolerance = 0
  AttachmentSupport = -> [XY_Plane055]
  FullyConstrained = true
  MakeInternals = false
  MapMode = 5
  sketch-geometry (4):
    g0: LineSegment StartX=15 StartY=-298 StartZ=0 EndX=135 EndY=-298 EndZ=0
    g1: ArcOfCircle CenterX=75 CenterY=-298 CenterZ=0 NormalX=0 NormalY=0 NormalZ=1 AngleXU=0 Radius=60 StartAngle=0 EndAngle=3.14159
    g2: LineSegment StartX=-135 StartY=-298 StartZ=0 EndX=-15 EndY=-298 EndZ=0
    g3: ArcOfCircle CenterX=-75 CenterY=-298 CenterZ=0 NormalX=0 NormalY=0 NormalZ=1 AngleXU=0 Radius=60 StartAngle=3e-16 EndAngle=3.14159
  constraints (14):
    c: PointOnObject(g1,g0)
    c: Coincident(g1,g0)
    c: Coincident(g1,g0)
    c: Horizontal(g0)
    c: DistanceX(g-1,g1) = 75
    c: DistanceY(g1,g-1) = 298
    c: Radius(g1) = 60
    c: Horizontal(g2)
    c: PointOnObject(g3,g2)
    c: Coincident(g3,g2)
    c: Coincident(g3,g2)
    c: Horizontal(g2,g0)
    c: Equal(g3,g1)
    c: DistanceX(g3,g-1) = 75
FEATURE [PartDesign::Groove] Groove083  label="Hip joints cuts002"
  Angle = 360
  Angle2 = 60
  Axis = (1,0,0)
  Base = (15,-298,0)
  BaseFeature = -> Fillet085
  Profile = -> Sketch172
  ReferenceAxis = -> Sketch172 [Edge1]
  Suppressed = false
  Type = 0
FEATURE [PartDesign::Revolution] Revolution089  label="Hip joints002"
  Angle = 360
  Angle2 = 60
  Axis = (1,0,0)
  Base = (15,-298,0)
  BaseFeature = -> Groove083
  Profile = -> Sketch172
  ReferenceAxis = -> Sketch172 [Edge1]
  Reversed = true
  Suppressed = false
  Type = 0
FEATURE [Sketcher::SketchObject] Sketch173
  ArcFitTolerance = 0
  AttachmentSupport = -> [YZ_Plane055]
  FullyConstrained = true
  MakeInternals = false
  MapMode = 5
  Placement = pos=(0,0,0) rot=(0.57735,0.57735,0.57735;2.0944rad)
  sketch-geometry (4):
    g0: LineSegment StartX=-309.733 StartY=84.7574 StartZ=0 EndX=-36.256 EndY=111.745 EndZ=0
    g1: LineSegment StartX=-36.256 StartY=111.745 StartZ=0 EndX=-36.256 EndY=192.709 EndZ=0
    g2: LineSegment StartX=-36.256 StartY=192.709 StartZ=0 EndX=-309.733 EndY=192.709 EndZ=0
    g3: LineSegment StartX=-309.733 StartY=192.709 StartZ=0 EndX=-309.733 EndY=84.7574 EndZ=0
  constraints (9):
    c: Coincident(g0,g1)
    c: Coincident(g1,g2)
    c: Horizontal(g2)
    c: Coincident(g2,g3)
    c: Coincident(g3,g0)
    c: Vertical(g3)
    c: Vertical(g1)
    c: Block(g3)
    c: Block(g0)
FEATURE [PartDesign::Pocket] Pocket030  label="front cut002"
  BaseFeature = -> Revolution089
  Direction = (-1,0,0)
  Length = 5
  Length2 = 5
  Midplane = true
  Profile = -> Sketch173
  ReferenceAxis = -> Sketch173 [N_Axis]
  Suppressed = false
  Type = 1
FEATURE [Sketcher::SketchObject] Sketch174
  ArcFitTolerance = 0
  AttachmentSupport = -> [YZ_Plane055]
  FullyConstrained = true
  MakeInternals = false
  MapMode = 5
  Placement = pos=(0,0,0) rot=(0.57735,0.57735,0.57735;2.0944rad)
  sketch-geometry (4):
    g0: LineSegment StartX=-276.336 StartY=-71.4724 StartZ=0 EndX=-109.323 EndY=-126.411 EndZ=0
    g1: LineSegment StartX=-109.323 StartY=-126.411 StartZ=0 EndX=-109.323 EndY=-220.905 EndZ=0
    g2: LineSegment StartX=-109.323 StartY=-220.905 StartZ=0 EndX=-276.336 EndY=-220.905 EndZ=0
    g3: LineSegment StartX=-276.336 StartY=-220.905 StartZ=0 EndX=-276.336 EndY=-71.4724 EndZ=0
  constraints (9):
    c: Coincident(g0,g1)
    c: Coincident(g1,g2)
    c: Horizontal(g2)
    c: Coincident(g2,g3)
    c: Coincident(g3,g0)
    c: Vertical(g3)
    c: Vertical(g1)
    c: Block(g0)
    c: Block(g2)
FEATURE [PartDesign::Pocket] Pocket031  label="rear cut002"
  BaseFeature = -> Pocket030
  Direction = (-1,0,0)
  Length = 5
  Length2 = 5
  Midplane = true
  Profile = -> Sketch174
  ReferenceAxis = -> Sketch174 [N_Axis]
  Suppressed = false
  Type = 1
FEATURE [PartDesign::Body] Body051  label="Hip002"
  AllowCompound = false
  Group = -> [Sketch170,Revolution088,Sketch171,Groove082,Fillet085,Sketch172,Groove083,Revolution089,Sketch173,Pocket030,Sketch174,Pocket031,Local_CS088,Local_CS090,Local_CS091]
  Origin = -> Origin055
  Placement = pos=(0,1197.02,0.388141) rot=(0,0,1;0rad)
  Tip = -> Pocket031
FEATURE [Sketcher::SketchObject] Sketch175
  ArcFitTolerance = 0
  AttachmentSupport = -> [XY_Plane056]
  FullyConstrained = true
  MakeInternals = false
  MapMode = 5
  sketch-geometry (12):
    g0: LineSegment StartX=15.9442 StartY=0 StartZ=0 EndX=306.848 EndY=0 EndZ=0
    g1-g6: Circle [constr] x6 (B-spline internal-alignment scaffolding for g7; pole/knot coordinates omitted)
    g7: BSplineCurve PolesCount=6 KnotsCount=4 Degree=3 IsPeriodic=0
    g8-g11: GeomPoint [constr] x4 (B-spline internal-alignment scaffolding for g7; pole/knot coordinates omitted)
  constraints (9):
    c: PointOnObject(g0,g-1)
    c: Horizontal(g0)
    c: Weight(g1) = 1
    c: Coincident(g7,g0)
    c: Equal(g1, g2-g6) x5
    c: Coincident(g7,g0)
    c: InternalAlignment(g1-g6 -> g7) x6
    c: InternalAlignment(g8-g11 -> g7) x4
    c: Block(g7)
FEATURE [PartDesign::Revolution] Revolution090  label="L Upper limb002"
  Angle = 360
  Angle2 = 60
  Axis = (1,0,0)
  Base = (0,0,0)
  Profile = -> Sketch175
  ReferenceAxis = -> Sketch175 [H_Axis]
  Suppressed = false
  Type = 0
FEATURE [PartDesign::CoordinateSystem] Local_CS092  label="Left upper limb/Shoulder LCS002"
  AttacherType = Attacher::AttachEngine3D
  AttachmentSupport = -> [Revolution090]
  MapMode = 2
FEATURE [PartDesign::CoordinateSystem] Local_CS093  label="Left upper limb/Elbow LCS002"
  AttacherType = Attacher::AttachEngine3D
  AttachmentOffset = pos=(320,0,0) rot=(0,0,1;0rad)
  AttachmentSupport = -> [Revolution090]
  MapMode = 2
  Placement = pos=(320,0,0) rot=(0,0,1;0rad)
FEATURE [Sketcher::SketchObject] Sketch176
  ArcFitTolerance = 0
  AttachmentSupport = -> [XY_Plane056]
  FullyConstrained = true
  MakeInternals = false
  MapMode = 5
  sketch-geometry (2):
    g0: LineSegment StartX=-60 StartY=7.3e-15 StartZ=0 EndX=60 EndY=7.3e-15 EndZ=0
    g1: ArcOfCircle CenterX=0 CenterY=0 CenterZ=0 NormalX=0 NormalY=0 NormalZ=1 AngleXU=0 Radius=60 StartAngle=0 EndAngle=3.14159
  constraints (6):
    c: Horizontal(g0)
    c: PointOnObject(g1,g0)
    c: Coincident(g1,g0)
    c: Coincident(g1,g0)
    c: Coincident(g1,g-1)
    c: Radius(g1) = 60
FEATURE [PartDesign::Groove] Groove084  label="L Sloulder cut002"
  Angle = 360
  Angle2 = 60
  Axis = (1,0,0)
  Base = (0,0,0)
  BaseFeature = -> Revolution090
  Profile = -> Sketch176
  ReferenceAxis = -> Sketch176 [H_Axis]
  Reversed = true
  Suppressed = false
  Type = 0
FEATURE [PartDesign::Fillet] Fillet086  label="L Shoulder fillet002"
  Base = -> Groove084 [Edge2]
  BaseFeature = -> Groove084
  Radius = 6
  SupportTransform = false
  Suppressed = false
  UseAllEdges = false
FEATURE [Sketcher::SketchObject] Sketch177
  ArcFitTolerance = 0
  AttachmentSupport = -> [XY_Plane056]
  FullyConstrained = true
  MakeInternals = false
  MapMode = 5
  sketch-geometry (2):
    g0: LineSegment StartX=285 StartY=0 StartZ=0 EndX=355 EndY=0 EndZ=0
    g1: ArcOfCircle CenterX=320 CenterY=0 CenterZ=0 NormalX=0 NormalY=0 NormalZ=1 AngleXU=0 Radius=35 StartAngle=0 EndAngle=3.14159
  constraints (7):
    c: Horizontal(g0)
    c: PointOnObject(g1,g0)
    c: Coincident(g1,g0)
    c: Coincident(g1,g0)
    c: Horizontal(g1,g-1)
    c: DistanceX(g-1,g1) = 320
    c: Radius(g1) = 35
FEATURE [PartDesign::Groove] Groove085  label="L Elbow cut002"
  Angle = 360
  Angle2 = 60
  Axis = (1,0,0)
  Base = (0,0,0)
  BaseFeature = -> Fillet086
  Profile = -> Sketch177
  ReferenceAxis = -> Sketch177 [H_Axis]
  Reversed = true
  Suppressed = false
  Type = 0
FEATURE [PartDesign::Fillet] Fillet087  label="L Elbow fillet002"
  Base = -> Groove085 [Edge1]
  BaseFeature = -> Groove085
  Radius = 3
  SupportTransform = false
  Suppressed = false
  UseAllEdges = false
FEATURE [PartDesign::Revolution] Revolution091  label="L Elbow002"
  Angle = 360
  Angle2 = 60
  Axis = (1,0,0)
  Base = (0,0,0)
  BaseFeature = -> Fillet087
  Profile = -> Sketch177
  ReferenceAxis = -> Sketch177 [H_Axis]
  Suppressed = false
  Type = 0
FEATURE [PartDesign::Body] Body052  label="Left Upper limb002"
  AllowCompound = false
  Group = -> [Sketch175,Revolution090,Sketch176,Groove084,Fillet086,Sketch177,Groove085,Fillet087,Revolution091,Local_CS092,Local_CS093]
  Origin = -> Origin056
  Placement = pos=(184,1454.02,0.388141) rot=(-0.249074,-0.271817,-0.929558;1.55647rad)
  Tip = -> Revolution091
FEATURE [Sketcher::SketchObject] Sketch178
  ArcFitTolerance = 0
  AttachmentSupport = -> [XY_Plane057]
  FullyConstrained = true
  MakeInternals = false
  MapMode = 5
  sketch-geometry (12):
    g0: LineSegment StartX=5.14795 StartY=0 StartZ=0 EndX=267.265 EndY=0 EndZ=0
    g1-g6: Circle [constr] x6 (B-spline internal-alignment scaffolding for g7; pole/knot coordinates omitted)
    g7: BSplineCurve PolesCount=6 KnotsCount=4 Degree=3 IsPeriodic=0
    g8-g11: GeomPoint [constr] x4 (B-spline internal-alignment scaffolding for g7; pole/knot coordinates omitted)
  constraints (9):
    c: PointOnObject(g0,g-1)
    c: Horizontal(g0)
    c: Weight(g1) = 1
    c: Coincident(g7,g0)
    c: Equal(g1, g2-g6) x5
    c: Coincident(g7,g0)
    c: InternalAlignment(g1-g6 -> g7) x6
    c: InternalAlignment(g8-g11 -> g7) x4
    c: Block(g7)
FEATURE [PartDesign::Revolution] Revolution092  label="Left Forearm main body002"
  Angle = 360
  Angle2 = 60
  Axis = (1,0,0)
  Base = (0,0,0)
  Profile = -> Sketch178
  ReferenceAxis = -> Sketch178 [H_Axis]
  Suppressed = false
  Type = 0
FEATURE [PartDesign::CoordinateSystem] Local_CS094  label="Left Forearm/Elbow002"
  AttacherType = Attacher::AttachEngine3D
  AttachmentSupport = -> [Revolution092]
  MapMode = 2
FEATURE [PartDesign::CoordinateSystem] Local_CS095  label="Left Forearm/Wrist002"
  AttacherType = Attacher::AttachEngine3D
  AttachmentOffset = pos=(253,0,0) rot=(0,0,1;0rad)
  AttachmentSupport = -> [Revolution092]
  MapMode = 2
  Placement = pos=(253,0,0) rot=(0,0,1;0rad)
FEATURE [Sketcher::SketchObject] Sketch179
  ArcFitTolerance = 0
  AttachmentSupport = -> [XY_Plane057]
  FullyConstrained = true
  MakeInternals = false
  MapMode = 5
  sketch-geometry (2):
    g0: LineSegment StartX=-35 StartY=4.3e-15 StartZ=0 EndX=35 EndY=4.3e-15 EndZ=0
    g1: ArcOfCircle CenterX=0 CenterY=0 CenterZ=0 NormalX=0 NormalY=0 NormalZ=1 AngleXU=0 Radius=35 StartAngle=0 EndAngle=3.14159
  constraints (6):
    c: Horizontal(g0)
    c: PointOnObject(g1,g0)
    c: Coincident(g1,g0)
    c: Coincident(g1,g0)
    c: Coincident(g1,g-1)
    c: Radius(g1) = 35
FEATURE [PartDesign::Groove] Groove086  label="Left elbow cut002"
  Angle = 360
  Angle2 = 60
  Axis = (1,0,0)
  Base = (0,0,0)
  BaseFeature = -> Revolution092
  Profile = -> Sketch179
  ReferenceAxis = -> Sketch179 [H_Axis]
  Reversed = true
  Suppressed = false
  Type = 0
FEATURE [PartDesign::Fillet] Fillet088  label="Left elbow fillet002"
  Base = -> Groove086 [Edge2]
  BaseFeature = -> Groove086
  Radius = 3
  SupportTransform = false
  Suppressed = false
  UseAllEdges = false
FEATURE [Sketcher::SketchObject] Sketch180
  ArcFitTolerance = 0
  AttachmentSupport = -> [XY_Plane057]
  FullyConstrained = true
  MakeInternals = false
  MapMode = 5
  sketch-geometry (2):
    g0: LineSegment StartX=228 StartY=0 StartZ=0 EndX=278 EndY=0 EndZ=0
    g1: ArcOfCircle CenterX=253 CenterY=0 CenterZ=0 NormalX=0 NormalY=0 NormalZ=1 AngleXU=0 Radius=25 StartAngle=-9e-16 EndAngle=3.14159
  constraints (7):
    c: Horizontal(g0)
    c: PointOnObject(g1,g0)
    c: Coincident(g1,g0)
    c: Coincident(g1,g0)
    c: Horizontal(g1,g-1)
    c: DistanceX(g-1,g1) = 253
    c: Radius(g1) = 25
FEATURE [PartDesign::Groove] Groove087  label="Left wrist cut002"
  Angle = 360
  Angle2 = 60
  Axis = (1,0,0)
  Base = (0,0,0)
  BaseFeature = -> Fillet088
  Profile = -> Sketch180
  ReferenceAxis = -> Sketch180 [H_Axis]
  Reversed = true
  Suppressed = false
  Type = 0
FEATURE [PartDesign::Fillet] Fillet089  label="Left wrist fillet002"
  Base = -> Groove087 [Edge1]
  BaseFeature = -> Groove087
  Radius = 3
  SupportTransform = false
  Suppressed = false
  UseAllEdges = false
FEATURE [PartDesign::Revolution] Revolution093  label="Left wrist002"
  Angle = 360
  Angle2 = 60
  Axis = (1,0,0)
  Base = (0,0,0)
  BaseFeature = -> Fillet089
  Profile = -> Sketch180
  ReferenceAxis = -> Sketch180 [H_Axis]
  Suppressed = false
  Type = 0
FEATURE [PartDesign::Body] Body053  label="Left Forearm002"
  AllowCompound = false
  Group = -> [Sketch178,Revolution092,Sketch179,Groove086,Fillet088,Sketch180,Groove087,Fillet089,Revolution093,Local_CS094,Local_CS095]
  Origin = -> Origin057
  Placement = pos=(208.153,1177.94,160.388) rot=(0.177175,-0.935113,-0.306876;1.63783rad)
  Tip = -> Revolution093
FEATURE [Sketcher::SketchObject] Sketch181
  ArcFitTolerance = 0
  AttachmentSupport = -> [XY_Plane058]
  FullyConstrained = true
  MakeInternals = false
  MapMode = 5
  sketch-geometry (10):
    g0: LineSegment StartX=6.14917 StartY=0 StartZ=0 EndX=149.382 EndY=0 EndZ=0
    g1-g5: Circle [constr] x5 (B-spline internal-alignment scaffolding for g6; pole/knot coordinates omitted)
    g6: BSplineCurve PolesCount=5 KnotsCount=3 Degree=3 IsPeriodic=0
    g7: GeomPoint [constr] X=6.14917 Y=0 Z=0
    g8: GeomPoint [constr] X=80.1264 Y=42.7238 Z=0
    g9: GeomPoint [constr] X=149.382 Y=0 Z=0
  constraints (12):
    c: PointOnObject(g0,g-1)
    c: Horizontal(g0)
    c: Weight(g1) = 1
    c: Coincident(g6,g0)
    c: Equal(g1, g2-g5) x4
    c: Coincident(g6,g0)
    c: InternalAlignment(g1-g5 -> g6) x5
    c: InternalAlignment(g7,g6)
    c: InternalAlignment(g8,g6)
    c: InternalAlignment(g9,g6)
    c: Vertical(g0,g4)
    c: Block(g6)
FEATURE [PartDesign::Revolution] Revolution094  label="L hand main body002"
  Angle = 360
  Angle2 = 60
  Axis = (1,0,0)
  Base = (0,0,0)
  Profile = -> Sketch181
  ReferenceAxis = -> Sketch181 [H_Axis]
  Suppressed = false
  Type = 0
FEATURE [PartDesign::CoordinateSystem] Local_CS096  label="Left Hand/Wrist LCS002"
  AttacherType = Attacher::AttachEngine3D
  AttachmentSupport = -> [Revolution094]
  MapMode = 2
FEATURE [Sketcher::SketchObject] Sketch182
  ArcFitTolerance = 0
  AttachmentSupport = -> [XY_Plane058]
  FullyConstrained = true
  MakeInternals = false
  MapMode = 5
  sketch-geometry (2):
    g0: LineSegment StartX=-25 StartY=0 StartZ=0 EndX=25 EndY=0 EndZ=0
    g1: ArcOfCircle CenterX=0 CenterY=0 CenterZ=0 NormalX=0 NormalY=0 NormalZ=1 AngleXU=0 Radius=25 StartAngle=0 EndAngle=3.14159
  constraints (6):
    c: Horizontal(g0)
    c: PointOnObject(g1,g0)
    c: Coincident(g1,g0)
    c: Coincident(g1,g0)
    c: Coincident(g1,g-1)
    c: Radius(g1) = 25
FEATURE [PartDesign::Groove] Groove088  label="wrist cut004"
  Angle = 360
  Angle2 = 60
  Axis = (1,0,0)
  Base = (0,0,0)
  BaseFeature = -> Revolution094
  Profile = -> Sketch182
  ReferenceAxis = -> Sketch182 [H_Axis]
  Reversed = true
  Suppressed = false
  Type = 0
FEATURE [PartDesign::Fillet] Fillet090  label="wrist fillet004"
  Base = -> Groove088 [Edge1]
  BaseFeature = -> Groove088
  Radius = 3
  SupportTransform = false
  Suppressed = false
  UseAllEdges = false
FEATURE [Sketcher::SketchObject] Sketch183
  ArcFitTolerance = 0
  AttachmentSupport = -> [YZ_Plane058]
  FullyConstrained = true
  MakeInternals = false
  MapMode = 5
  Placement = pos=(0,0,0) rot=(0.57735,0.57735,0.57735;2.0944rad)
  sketch-geometry (3):
    g0: ArcOfCircle CenterX=0 CenterY=125.857 CenterZ=0 NormalX=0 NormalY=0 NormalZ=1 AngleXU=0 Radius=99.8092 StartAngle=3.99571 EndAngle=5.39163
    g1: LineSegment StartX=-65.5632 StartY=50.6013 StartZ=0 EndX=0 EndY=125.857 EndZ=0
    g2: LineSegment StartX=0 StartY=125.857 StartZ=0 EndX=62.7007 EndY=48.2002 EndZ=0
  constraints (6):
    c: PointOnObject(g0,g-2)
    c: Coincident(g1,g0)
    c: Coincident(g1,g0)
    c: Coincident(g2,g0)
    c: Coincident(g2,g0)
    c: Block(g0)
FEATURE [PartDesign::Pocket] Pocket032
  BaseFeature = -> Fillet090
  Direction = (1,0,0)
  Length = 5
  Length2 = 5
  Profile = -> Sketch183
  ReferenceAxis = -> Sketch183 [N_Axis]
  Suppressed = false
  Type = 1
  UseCustomVector = true
FEATURE [Sketcher::SketchObject] Sketch184
  ArcFitTolerance = 0
  AttachmentSupport = -> [YZ_Plane058]
  FullyConstrained = true
  MakeInternals = false
  MapMode = 5
  Placement = pos=(0,0,0) rot=(0.57735,0.57735,0.57735;2.0944rad)
  sketch-geometry (4):
    g0: ArcOfCircle CenterX=0 CenterY=78.6838 CenterZ=0 NormalX=0 NormalY=0 NormalZ=1 AngleXU=0 Radius=107.987 StartAngle=3.91888 EndAngle=5.56935
    g1: LineSegment StartX=81.6221 StartY=7.98042 StartZ=0 EndX=81.6221 EndY=-69.912 EndZ=0
    g2: LineSegment StartX=81.6221 StartY=-69.912 StartZ=0 EndX=-76.9748 EndY=-69.912 EndZ=0
    g3: LineSegment StartX=-76.9748 StartY=-69.912 StartZ=0 EndX=-76.9748 EndY=2.94733 EndZ=0
  constraints (10):
    c: PointOnObject(g0,g-2)
    c: Coincident(g0,g1)
    c: Coincident(g1,g2)
    c: Horizontal(g2)
    c: Coincident(g2,g3)
    c: Coincident(g3,g0)
    c: Vertical(g3)
    c: Vertical(g1)
    c: Block(g0)
    c: Block(g2)
FEATURE [PartDesign::Pocket] Pocket033
  BaseFeature = -> Pocket032
  Direction = (1,0,0)
  Length = 5
  Length2 = 5
  Profile = -> Sketch184
  ReferenceAxis = -> Sketch184 [N_Axis]
  Suppressed = false
  Type = 1
  UseCustomVector = true
FEATURE [PartDesign::Body] Body054  label="Left hand002"
  AllowCompound = false
  Group = -> [Sketch181,Revolution094,Sketch182,Groove088,Fillet090,Sketch183,Pocket032,Sketch184,Pocket033,Local_CS096]
  Origin = -> Origin058
  Placement = pos=(199.679,1055.76,381.763) rot=(-0.313147,-0.71674,-0.623075;1.84806rad)
  Tip = -> Pocket033
FEATURE [Sketcher::SketchObject] Sketch185
  ArcFitTolerance = 0
  AttachmentSupport = -> [XY_Plane059]
  FullyConstrained = true
  MakeInternals = false
  MapMode = 5
  sketch-geometry (12):
    g0: LineSegment StartX=15.9442 StartY=0 StartZ=0 EndX=306.848 EndY=0 EndZ=0
    g1-g6: Circle [constr] x6 (B-spline internal-alignment scaffolding for g7; pole/knot coordinates omitted)
    g7: BSplineCurve PolesCount=6 KnotsCount=4 Degree=3 IsPeriodic=0
    g8-g11: GeomPoint [constr] x4 (B-spline internal-alignment scaffolding for g7; pole/knot coordinates omitted)
  constraints (9):
    c: PointOnObject(g0,g-1)
    c: Horizontal(g0)
    c: Weight(g1) = 1
    c: Coincident(g7,g0)
    c: Equal(g1, g2-g6) x5
    c: Coincident(g7,g0)
    c: InternalAlignment(g1-g6 -> g7) x6
    c: InternalAlignment(g8-g11 -> g7) x4
    c: Block(g7)
FEATURE [PartDesign::Revolution] Revolution095  label="R Upper limb002"
  Angle = 360
  Angle2 = 60
  Axis = (1,0,0)
  Base = (0,0,0)
  Profile = -> Sketch185
  ReferenceAxis = -> Sketch185 [H_Axis]
  Suppressed = false
  Type = 0
FEATURE [PartDesign::CoordinateSystem] Local_CS097  label="Right upper limb/Shoulder LCS002"
  AttacherType = Attacher::AttachEngine3D
  AttachmentOffset = pos=(0,0,0) rot=(0,0,1;3.14159rad)
  AttachmentSupport = -> [Revolution095]
  MapMode = 2
  Placement = pos=(0,0,0) rot=(0,0,1;3.14159rad)
FEATURE [PartDesign::CoordinateSystem] Local_CS098  label="Right upper limb/Elbow LCS002"
  AttacherType = Attacher::AttachEngine3D
  AttachmentOffset = pos=(320,0,0) rot=(0,0,1;3.14159rad)
  AttachmentSupport = -> [Revolution095]
  MapMode = 2
  Placement = pos=(320,0,0) rot=(0,0,1;3.14159rad)
FEATURE [Sketcher::SketchObject] Sketch186
  ArcFitTolerance = 0
  AttachmentSupport = -> [XY_Plane059]
  FullyConstrained = true
  MakeInternals = false
  MapMode = 5
  sketch-geometry (2):
    g0: LineSegment StartX=-60 StartY=0 StartZ=0 EndX=60 EndY=0 EndZ=0
    g1: ArcOfCircle CenterX=0 CenterY=0 CenterZ=0 NormalX=0 NormalY=0 NormalZ=1 AngleXU=0 Radius=60 StartAngle=0 EndAngle=3.14159
  constraints (6):
    c: Horizontal(g0)
    c: PointOnObject(g1,g0)
    c: Coincident(g1,g0)
    c: Coincident(g1,g0)
    c: Coincident(g1,g-1)
    c: Radius(g1) = 60
FEATURE [PartDesign::Groove] Groove089  label="R Sloulder cut002"
  Angle = 360
  Angle2 = 60
  Axis = (1,0,0)
  Base = (0,0,0)
  BaseFeature = -> Revolution095
  Profile = -> Sketch186
  ReferenceAxis = -> Sketch186 [H_Axis]
  Reversed = true
  Suppressed = false
  Type = 0
FEATURE [PartDesign::Fillet] Fillet091  label="R Shoulder fillet002"
  Base = -> Groove089 [Edge2]
  BaseFeature = -> Groove089
  Radius = 6
  SupportTransform = false
  Suppressed = false
  UseAllEdges = false
FEATURE [Sketcher::SketchObject] Sketch187
  ArcFitTolerance = 0
  AttachmentSupport = -> [XY_Plane059]
  FullyConstrained = true
  MakeInternals = false
  MapMode = 5
  sketch-geometry (2):
    g0: LineSegment StartX=285 StartY=4.3e-15 StartZ=0 EndX=355 EndY=4.3e-15 EndZ=0
    g1: ArcOfCircle CenterX=320 CenterY=0 CenterZ=0 NormalX=0 NormalY=0 NormalZ=1 AngleXU=0 Radius=35 StartAngle=0 EndAngle=3.14159
  constraints (7):
    c: Horizontal(g0)
    c: PointOnObject(g1,g0)
    c: Coincident(g1,g0)
    c: Coincident(g1,g0)
    c: Horizontal(g1,g-1)
    c: DistanceX(g-1,g1) = 320
    c: Radius(g1) = 35
FEATURE [PartDesign::Groove] Groove090  label="R Elbow cut002"
  Angle = 360
  Angle2 = 60
  Axis = (1,0,0)
  Base = (0,0,0)
  BaseFeature = -> Fillet091
  Profile = -> Sketch187
  ReferenceAxis = -> Sketch187 [H_Axis]
  Reversed = true
  Suppressed = false
  Type = 0
FEATURE [PartDesign::Fillet] Fillet092  label="R Elbow fillet002"
  Base = -> Groove090 [Edge1]
  BaseFeature = -> Groove090
  Radius = 3
  SupportTransform = false
  Suppressed = false
  UseAllEdges = false
FEATURE [PartDesign::Revolution] Revolution096  label="R Elbow002"
  Angle = 360
  Angle2 = 60
  Axis = (1,0,0)
  Base = (0,0,0)
  BaseFeature = -> Fillet092
  Profile = -> Sketch187
  ReferenceAxis = -> Sketch187 [H_Axis]
  Suppressed = false
  Type = 0
FEATURE [PartDesign::Body] Body055  label="Right Upper limb002"
  AllowCompound = false
  Group = -> [Sketch185,Revolution095,Sketch186,Groove089,Fillet091,Sketch187,Groove090,Fillet092,Revolution096,Local_CS097,Local_CS098]
  Origin = -> Origin059
  Placement = pos=(-184,1454.02,0.388141) rot=(0.150211,0.140074,-0.978681;1.73173rad)
  Tip = -> Revolution096
FEATURE [Sketcher::SketchObject] Sketch188
  ArcFitTolerance = 0
  AttachmentSupport = -> [XY_Plane060]
  FullyConstrained = true
  MakeInternals = false
  MapMode = 5
  sketch-geometry (12):
    g0: LineSegment StartX=5.14795 StartY=0 StartZ=0 EndX=267.265 EndY=0 EndZ=0
    g1-g6: Circle [constr] x6 (B-spline internal-alignment scaffolding for g7; pole/knot coordinates omitted)
    g7: BSplineCurve PolesCount=6 KnotsCount=4 Degree=3 IsPeriodic=0
    g8-g11: GeomPoint [constr] x4 (B-spline internal-alignment scaffolding for g7; pole/knot coordinates omitted)
  constraints (9):
    c: PointOnObject(g0,g-1)
    c: Horizontal(g0)
    c: Weight(g1) = 1
    c: Coincident(g7,g0)
    c: Equal(g1, g2-g6) x5
    c: Coincident(g7,g0)
    c: InternalAlignment(g1-g6 -> g7) x6
    c: InternalAlignment(g8-g11 -> g7) x4
    c: Block(g7)
FEATURE [PartDesign::Revolution] Revolution097  label="Right Forearm main body002"
  Angle = 360
  Angle2 = 60
  Axis = (1,0,0)
  Base = (0,0,0)
  Profile = -> Sketch188
  ReferenceAxis = -> Sketch188 [H_Axis]
  Suppressed = false
  Type = 0
FEATURE [PartDesign::CoordinateSystem] Local_CS099  label="Right Forearm/Elbow002"
  AttacherType = Attacher::AttachEngine3D
  AttachmentOffset = pos=(0,0,0) rot=(0,0,1;3.14159rad)
  AttachmentSupport = -> [Revolution097]
  MapMode = 2
  Placement = pos=(0,0,0) rot=(0,0,1;3.14159rad)
FEATURE [PartDesign::CoordinateSystem] Local_CS100  label="Right Forearm/Wrist002"
  AttacherType = Attacher::AttachEngine3D
  AttachmentOffset = pos=(253,0,0) rot=(0,0,1;3.14159rad)
  AttachmentSupport = -> [Revolution097]
  MapMode = 2
  Placement = pos=(253,0,0) rot=(0,0,1;3.14159rad)
FEATURE [Sketcher::SketchObject] Sketch189
  ArcFitTolerance = 0
  AttachmentSupport = -> [XY_Plane060]
  FullyConstrained = true
  MakeInternals = false
  MapMode = 5
  sketch-geometry (2):
    g0: LineSegment StartX=-35 StartY=4.3e-15 StartZ=0 EndX=35 EndY=4.3e-15 EndZ=0
    g1: ArcOfCircle CenterX=0 CenterY=0 CenterZ=0 NormalX=0 NormalY=0 NormalZ=1 AngleXU=0 Radius=35 StartAngle=0 EndAngle=3.14159
  constraints (6):
    c: Horizontal(g0)
    c: PointOnObject(g1,g0)
    c: Coincident(g1,g0)
    c: Coincident(g1,g0)
    c: Coincident(g1,g-1)
    c: Radius(g1) = 35
FEATURE [PartDesign::Groove] Groove091  label="Right elbow cut002"
  Angle = 360
  Angle2 = 60
  Axis = (1,0,0)
  Base = (0,0,0)
  BaseFeature = -> Revolution097
  Profile = -> Sketch189
  ReferenceAxis = -> Sketch189 [H_Axis]
  Reversed = true
  Suppressed = false
  Type = 0
FEATURE [PartDesign::Fillet] Fillet093  label="Right elbow fillet002"
  Base = -> Groove091 [Edge2]
  BaseFeature = -> Groove091
  Radius = 3
  SupportTransform = false
  Suppressed = false
  UseAllEdges = false
FEATURE [Sketcher::SketchObject] Sketch190
  ArcFitTolerance = 0
  AttachmentSupport = -> [XY_Plane060]
  FullyConstrained = true
  MakeInternals = false
  MapMode = 5
  sketch-geometry (2):
    g0: LineSegment StartX=228 StartY=0 StartZ=0 EndX=278 EndY=0 EndZ=0
    g1: ArcOfCircle CenterX=253 CenterY=0 CenterZ=0 NormalX=0 NormalY=0 NormalZ=1 AngleXU=0 Radius=25 StartAngle=-9e-16 EndAngle=3.14159
  constraints (7):
    c: Horizontal(g0)
    c: PointOnObject(g1,g0)
    c: Coincident(g1,g0)
    c: Coincident(g1,g0)
    c: Horizontal(g1,g-1)
    c: DistanceX(g-1,g1) = 253
    c: Radius(g1) = 25
FEATURE [PartDesign::Groove] Groove092  label="Right wrist cut002"
  Angle = 360
  Angle2 = 60
  Axis = (1,0,0)
  Base = (0,0,0)
  BaseFeature = -> Fillet093
  Profile = -> Sketch190
  ReferenceAxis = -> Sketch190 [H_Axis]
  Reversed = true
  Suppressed = false
  Type = 0
FEATURE [PartDesign::Fillet] Fillet094  label="Right wrist fillet002"
  Base = -> Groove092 [Edge1]
  BaseFeature = -> Groove092
  Radius = 3
  SupportTransform = false
  Suppressed = false
  UseAllEdges = false
FEATURE [PartDesign::Revolution] Revolution098  label="Right wrist002"
  Angle = 360
  Angle2 = 60
  Axis = (1,0,0)
  Base = (0,0,0)
  BaseFeature = -> Fillet094
  Profile = -> Sketch190
  ReferenceAxis = -> Sketch190 [H_Axis]
  Suppressed = false
  Type = 0
FEATURE [PartDesign::Body] Body056  label="Right Forearm002"
  AllowCompound = false
  Group = -> [Sketch188,Revolution097,Sketch189,Groove091,Fillet093,Sketch190,Groove092,Fillet094,Revolution098,Local_CS099,Local_CS100]
  Origin = -> Origin060
  Placement = pos=(-226.899,1152.7,-98.4371) rot=(0.649604,-0.34652,0.676712;3.40001rad)
  Tip = -> Revolution098
FEATURE [Sketcher::SketchObject] Sketch191
  ArcFitTolerance = 0
  AttachmentSupport = -> [XY_Plane061]
  FullyConstrained = true
  MakeInternals = false
  MapMode = 5
  sketch-geometry (10):
    g0: LineSegment StartX=6.14917 StartY=0 StartZ=0 EndX=149.382 EndY=0 EndZ=0
    g1-g5: Circle [constr] x5 (B-spline internal-alignment scaffolding for g6; pole/knot coordinates omitted)
    g6: BSplineCurve PolesCount=5 KnotsCount=3 Degree=3 IsPeriodic=0
    g7: GeomPoint [constr] X=6.14917 Y=0 Z=0
    g8: GeomPoint [constr] X=80.1264 Y=42.7238 Z=0
    g9: GeomPoint [constr] X=149.382 Y=0 Z=0
  constraints (12):
    c: PointOnObject(g0,g-1)
    c: Horizontal(g0)
    c: Weight(g1) = 1
    c: Coincident(g6,g0)
    c: Equal(g1, g2-g5) x4
    c: Coincident(g6,g0)
    c: InternalAlignment(g1-g5 -> g6) x5
    c: InternalAlignment(g7,g6)
    c: InternalAlignment(g8,g6)
    c: InternalAlignment(g9,g6)
    c: Vertical(g0,g4)
    c: Block(g6)
FEATURE [PartDesign::Revolution] Revolution099  label="R hand main body002"
  Angle = 360
  Angle2 = 60
  Axis = (1,0,0)
  Base = (0,0,0)
  Profile = -> Sketch191
  ReferenceAxis = -> Sketch191 [H_Axis]
  Suppressed = false
  Type = 0
FEATURE [PartDesign::CoordinateSystem] Local_CS101  label="Right Hand/Wrist LCS002"
  AttacherType = Attacher::AttachEngine3D
  AttachmentOffset = pos=(0,0,0) rot=(0,0,1;3.14159rad)
  AttachmentSupport = -> [Revolution099]
  MapMode = 2
  Placement = pos=(0,0,0) rot=(0,0,1;3.14159rad)
FEATURE [Sketcher::SketchObject] Sketch192
  ArcFitTolerance = 0
  AttachmentSupport = -> [XY_Plane061]
  FullyConstrained = true
  MakeInternals = false
  MapMode = 5
  sketch-geometry (2):
    g0: LineSegment StartX=-25 StartY=3.1e-15 StartZ=0 EndX=25 EndY=3.1e-15 EndZ=0
    g1: ArcOfCircle CenterX=0 CenterY=0 CenterZ=0 NormalX=0 NormalY=0 NormalZ=1 AngleXU=0 Radius=25 StartAngle=0 EndAngle=3.14159
  constraints (6):
    c: Horizontal(g0)
    c: PointOnObject(g1,g0)
    c: Coincident(g1,g0)
    c: Coincident(g1,g0)
    c: Coincident(g1,g-1)
    c: Radius(g1) = 25
FEATURE [PartDesign::Groove] Groove093  label="wrist cut005"
  Angle = 360
  Angle2 = 60
  Axis = (1,0,0)
  Base = (0,0,0)
  BaseFeature = -> Revolution099
  Profile = -> Sketch192
  ReferenceAxis = -> Sketch192 [H_Axis]
  Reversed = true
  Suppressed = false
  Type = 0
FEATURE [PartDesign::Fillet] Fillet095  label="wrist fillet005"
  Base = -> Groove093 [Edge1]
  BaseFeature = -> Groove093
  Radius = 3
  SupportTransform = false
  Suppressed = false
  UseAllEdges = false
FEATURE [Sketcher::SketchObject] Sketch193
  ArcFitTolerance = 0
  AttachmentSupport = -> [YZ_Plane061]
  FullyConstrained = true
  MakeInternals = false
  MapMode = 5
  Placement = pos=(0,0,0) rot=(0.57735,0.57735,0.57735;2.0944rad)
  sketch-geometry (3):
    g0: ArcOfCircle CenterX=0 CenterY=125.857 CenterZ=0 NormalX=0 NormalY=0 NormalZ=1 AngleXU=0 Radius=99.8092 StartAngle=3.99571 EndAngle=5.39163
    g1: LineSegment StartX=-65.5632 StartY=50.6013 StartZ=0 EndX=0 EndY=125.857 EndZ=0
    g2: LineSegment StartX=0 StartY=125.857 StartZ=0 EndX=62.7007 EndY=48.2002 EndZ=0
  constraints (6):
    c: PointOnObject(g0,g-2)
    c: Coincident(g1,g0)
    c: Coincident(g1,g0)
    c: Coincident(g2,g0)
    c: Coincident(g2,g0)
    c: Block(g0)
FEATURE [PartDesign::Pocket] Pocket034
  BaseFeature = -> Fillet095
  Direction = (1,0,0)
  Length = 5
  Length2 = 5
  Profile = -> Sketch193
  ReferenceAxis = -> Sketch193 [N_Axis]
  Suppressed = false
  Type = 1
  UseCustomVector = true
FEATURE [Sketcher::SketchObject] Sketch194
  ArcFitTolerance = 0
  AttachmentSupport = -> [YZ_Plane061]
  FullyConstrained = true
  MakeInternals = false
  MapMode = 5
  Placement = pos=(0,0,0) rot=(0.57735,0.57735,0.57735;2.0944rad)
  sketch-geometry (4):
    g0: ArcOfCircle CenterX=0 CenterY=78.6838 CenterZ=0 NormalX=0 NormalY=0 NormalZ=1 AngleXU=0 Radius=107.987 StartAngle=3.91888 EndAngle=5.56935
    g1: LineSegment StartX=81.6221 StartY=7.98042 StartZ=0 EndX=81.6221 EndY=-69.912 EndZ=0
    g2: LineSegment StartX=81.6221 StartY=-69.912 StartZ=0 EndX=-76.9748 EndY=-69.912 EndZ=0
    g3: LineSegment StartX=-76.9748 StartY=-69.912 StartZ=0 EndX=-76.9748 EndY=2.94733 EndZ=0
  constraints (10):
    c: PointOnObject(g0,g-2)
    c: Coincident(g0,g1)
    c: Coincident(g1,g2)
    c: Horizontal(g2)
    c: Coincident(g2,g3)
    c: Coincident(g3,g0)
    c: Vertical(g3)
    c: Vertical(g1)
    c: Block(g0)
    c: Block(g2)
FEATURE [PartDesign::Pocket] Pocket035
  BaseFeature = -> Pocket034
  Direction = (1,0,0)
  Length = 5
  Length2 = 5
  Profile = -> Sketch194
  ReferenceAxis = -> Sketch194 [N_Axis]
  Suppressed = false
  Type = 1
  UseCustomVector = true
FEATURE [PartDesign::Body] Body057  label="Right hand002"
  AllowCompound = false
  Group = -> [Sketch191,Revolution099,Sketch192,Groove093,Fillet095,Sketch193,Pocket034,Sketch194,Pocket035,Local_CS101]
  Origin = -> Origin061
  Placement = pos=(-261.519,996.937,97.9008) rot=(0.654,-0.009822,0.756431;3.48846rad)
  Tip = -> Pocket035
FEATURE [Sketcher::SketchObject] Sketch195
  ArcFitTolerance = 0
  AttachmentSupport = -> [XY_Plane062]
  FullyConstrained = true
  MakeInternals = false
  MapMode = 5
  sketch-geometry (14):
    g0: LineSegment StartX=0 StartY=-29.246 StartZ=0 EndX=0 EndY=-395.97 EndZ=0
    g1-g7: Circle [constr] x7 (B-spline internal-alignment scaffolding for g8; pole/knot coordinates omitted)
    g8: BSplineCurve PolesCount=7 KnotsCount=5 Degree=3 IsPeriodic=0
    g9-g13: GeomPoint [constr] x5 (B-spline internal-alignment scaffolding for g8; pole/knot coordinates omitted)
  constraints (11):
    c: PointOnObject(g0,g-2)
    c: Vertical(g0)
    c: Weight(g1) = 1
    c: Coincident(g8,g0)
    c: Equal(g1, g2-g7) x6
    c: Coincident(g8,g0)
    c: InternalAlignment(g1-g7 -> g8) x7
    c: InternalAlignment(g9-g13 -> g8) x5
    c: Horizontal(g0,g6)
    c: Horizontal(g0,g2)
    c: Block(g8)
FEATURE [PartDesign::Revolution] Revolution100  label="L Thigh main body002"
  Angle = 360
  Angle2 = 60
  Axis = (0,1,0)
  Base = (0,0,0)
  Profile = -> Sketch195
  ReferenceAxis = -> Sketch195 [V_Axis]
  Reversed = true
  Suppressed = false
  Type = 0
FEATURE [PartDesign::CoordinateSystem] Local_CS102  label="Left Thigh/Big joint LCS002"
  AttacherType = Attacher::AttachEngine3D
  AttachmentSupport = -> [Revolution100]
  MapMode = 2
FEATURE [PartDesign::CoordinateSystem] Local_CS103  label="Left Thigh/Knee LCS002"
  AttacherType = Attacher::AttachEngine3D
  AttachmentOffset = pos=(0,-403,0) rot=(0,0,1;0rad)
  AttachmentSupport = -> [Revolution100]
  MapMode = 2
  Placement = pos=(0,-403,0) rot=(0,0,1;0rad)
FEATURE [Sketcher::SketchObject] Sketch196
  ArcFitTolerance = 0
  AttachmentSupport = -> [XY_Plane062]
  FullyConstrained = true
  MakeInternals = false
  MapMode = 5
  sketch-geometry (2):
    g0: LineSegment StartX=1.84e-14 StartY=60 StartZ=0 EndX=1.84e-14 EndY=-60 EndZ=0
    g1: ArcOfCircle CenterX=0 CenterY=0 CenterZ=0 NormalX=0 NormalY=0 NormalZ=1 AngleXU=0 Radius=60 StartAngle=4.71239 EndAngle=7.85398
  constraints (6):
    c: Vertical(g0)
    c: PointOnObject(g1,g0)
    c: Coincident(g1,g0)
    c: Coincident(g1,g0)
    c: Coincident(g1,g-1)
    c: Radius(g1) = 60
FEATURE [PartDesign::Groove] Groove094  label="L Big joint002"
  Angle = 360
  Angle2 = 60
  Axis = (0,1,0)
  Base = (0,0,0)
  BaseFeature = -> Revolution100
  Profile = -> Sketch196
  ReferenceAxis = -> Sketch196 [V_Axis]
  Suppressed = false
  Type = 0
FEATURE [PartDesign::Fillet] Fillet096
  Base = -> Groove094 [Edge1]
  BaseFeature = -> Groove094
  Radius = 6
  SupportTransform = false
  Suppressed = false
  UseAllEdges = false
FEATURE [Sketcher::SketchObject] Sketch197
  ArcFitTolerance = 0
  AttachmentSupport = -> [XY_Plane062]
  FullyConstrained = true
  MakeInternals = false
  MapMode = 5
  sketch-geometry (2):
    g0: LineSegment StartX=-6.4e-15 StartY=-368 StartZ=0 EndX=-6.4e-15 EndY=-438 EndZ=0
    g1: ArcOfCircle CenterX=0 CenterY=-403 CenterZ=0 NormalX=0 NormalY=0 NormalZ=1 AngleXU=0 Radius=35 StartAngle=4.71239 EndAngle=7.85398
  constraints (7):
    c: Vertical(g0)
    c: PointOnObject(g1,g0)
    c: Coincident(g1,g0)
    c: Coincident(g1,g0)
    c: PointOnObject(g1,g-2)
    c: DistanceY(g1,g-1) = 403
    c: Radius(g1) = 35
FEATURE [PartDesign::Groove] Groove095  label="L Knee cut002"
  Angle = 360
  Angle2 = 60
  Axis = (0,1,0)
  Base = (0,0,0)
  BaseFeature = -> Fillet096
  Profile = -> Sketch197
  ReferenceAxis = -> Sketch197 [V_Axis]
  Suppressed = false
  Type = 0
FEATURE [PartDesign::Fillet] Fillet097
  Base = -> Groove095 [Edge1]
  BaseFeature = -> Groove095
  Radius = 3
  SupportTransform = false
  Suppressed = false
  UseAllEdges = false
FEATURE [PartDesign::Revolution] Revolution101  label="L Knee002"
  Angle = 360
  Angle2 = 60
  Axis = (0,1,0)
  Base = (0,0,0)
  BaseFeature = -> Fillet097
  Profile = -> Sketch197
  ReferenceAxis = -> Sketch197 [V_Axis]
  Reversed = true
  Suppressed = false
  Type = 0
FEATURE [PartDesign::Body] Body058  label="Left Thigh002"
  AllowCompound = false
  Group = -> [Sketch195,Revolution100,Sketch196,Groove094,Fillet096,Sketch197,Groove095,Fillet097,Revolution101,Local_CS102,Local_CS103]
  Origin = -> Origin062
  Placement = pos=(75,899.018,0.388141) rot=(1,0,0;0.05236rad)
  Tip = -> Revolution101
FEATURE [Sketcher::SketchObject] Sketch198
  ArcFitTolerance = 0
  AttachmentSupport = -> [XY_Plane063]
  FullyConstrained = true
  MakeInternals = false
  MapMode = 5
  sketch-geometry (14):
    g0: LineSegment StartX=0 StartY=0 StartZ=0 EndX=0 EndY=-428.766 EndZ=0
    g1-g7: Circle [constr] x7 (B-spline internal-alignment scaffolding for g8; pole/knot coordinates omitted)
    g8: BSplineCurve PolesCount=7 KnotsCount=5 Degree=3 IsPeriodic=0
    g9-g13: GeomPoint [constr] x5 (B-spline internal-alignment scaffolding for g8; pole/knot coordinates omitted)
  constraints (9):
    c: Vertical(g0)
    c: PointOnObject(g0,g-2)
    c: Weight(g1) = 1
    c: Coincident(g8,g0)
    c: Equal(g1, g2-g7) x6
    c: Coincident(g8,g0)
    c: InternalAlignment(g1-g7 -> g8) x7
    c: InternalAlignment(g9-g13 -> g8) x5
    c: Block(g8)
FEATURE [PartDesign::Revolution] Revolution102  label="L Shin main body002"
  Angle = 360
  Angle2 = 60
  Axis = (0,1,0)
  Base = (0,0,0)
  Profile = -> Sketch198
  ReferenceAxis = -> Sketch198 [V_Axis]
  Reversed = true
  Suppressed = false
  Type = 0
FEATURE [PartDesign::CoordinateSystem] Local_CS104  label="Left Shin/Knee002"
  AttacherType = Attacher::AttachEngine3D
  AttachmentSupport = -> [Revolution102]
  MapMode = 2
FEATURE [PartDesign::CoordinateSystem] Local_CS105  label="Left Shin/Ankle002"
  AttacherType = Attacher::AttachEngine3D
  AttachmentOffset = pos=(0,-435,0) rot=(0,0,1;0rad)
  AttachmentSupport = -> [Revolution102]
  MapMode = 2
  Placement = pos=(0,-435,0) rot=(0,0,1;0rad)
FEATURE [Sketcher::SketchObject] Sketch199
  ArcFitTolerance = 0
  AttachmentSupport = -> [XY_Plane063]
  FullyConstrained = true
  MakeInternals = false
  MapMode = 5
  sketch-geometry (2):
    g0: LineSegment StartX=0 StartY=35 StartZ=0 EndX=0 EndY=-35 EndZ=0
    g1: ArcOfCircle CenterX=0 CenterY=0 CenterZ=0 NormalX=0 NormalY=0 NormalZ=1 AngleXU=0 Radius=35 StartAngle=4.71239 EndAngle=7.85398
  constraints (6):
    c: PointOnObject(g1,g0)
    c: Coincident(g1,g0)
    c: Coincident(g1,g0)
    c: Vertical(g0)
    c: Coincident(g1,g-1)
    c: Radius(g1) = 35
FEATURE [PartDesign::Groove] Groove096  label="L knee cut002"
  Angle = 360
  Angle2 = 60
  Axis = (0,1,0)
  Base = (0,0,0)
  BaseFeature = -> Revolution102
  Profile = -> Sketch199
  ReferenceAxis = -> Sketch199 [V_Axis]
  Suppressed = false
  Type = 0
FEATURE [PartDesign::Fillet] Fillet098
  Base = -> Groove096 [Edge1]
  BaseFeature = -> Groove096
  Radius = 3
  SupportTransform = false
  Suppressed = false
  UseAllEdges = false
FEATURE [Sketcher::SketchObject] Sketch200
  ArcFitTolerance = 0
  AttachmentSupport = -> [XY_Plane063]
  FullyConstrained = true
  MakeInternals = false
  MapMode = 5
  sketch-geometry (2):
    g0: LineSegment StartX=-4.6e-15 StartY=-410 StartZ=0 EndX=-4.6e-15 EndY=-460 EndZ=0
    g1: ArcOfCircle CenterX=0 CenterY=-435 CenterZ=0 NormalX=0 NormalY=0 NormalZ=1 AngleXU=0 Radius=25 StartAngle=4.71239 EndAngle=7.85398
  constraints (7):
    c: Vertical(g0)
    c: PointOnObject(g1,g0)
    c: Coincident(g1,g0)
    c: Coincident(g1,g0)
    c: PointOnObject(g1,g-2)
    c: DistanceY(g1,g-1) = 435
    c: Radius(g1) = 25
FEATURE [PartDesign::Groove] Groove097  label="L Ankle cut002"
  Angle = 360
  Angle2 = 60
  Axis = (0,1,0)
  Base = (0,0,0)
  BaseFeature = -> Fillet098
  Profile = -> Sketch200
  ReferenceAxis = -> Sketch200 [V_Axis]
  Suppressed = false
  Type = 0
FEATURE [PartDesign::Fillet] Fillet099
  Base = -> Groove097 [Edge3]
  BaseFeature = -> Groove097
  Radius = 3
  SupportTransform = false
  Suppressed = false
  UseAllEdges = false
FEATURE [PartDesign::Revolution] Revolution103  label="L Ankle002"
  Angle = 360
  Angle2 = 60
  Axis = (0,1,0)
  Base = (0,0,0)
  BaseFeature = -> Fillet099
  Profile = -> Sketch200
  ReferenceAxis = -> Sketch200 [V_Axis]
  Reversed = true
  Suppressed = false
  Type = 0
FEATURE [PartDesign::Body] Body059  label="Left Shin002"
  AllowCompound = false
  Group = -> [Sketch198,Revolution102,Sketch199,Groove096,Fillet098,Sketch200,Groove097,Fillet099,Revolution103,Local_CS104,Local_CS105]
  Origin = -> Origin063
  Placement = pos=(75,496.571,-20.7032) rot=(1,0,0;0.10472rad)
  Tip = -> Revolution103
FEATURE [Sketcher::SketchObject] Sketch201
  ArcFitTolerance = 0
  AttachmentSupport = -> [YZ_Plane064]
  FullyConstrained = true
  MakeInternals = false
  MapMode = 5
  Placement = pos=(0,0,0) rot=(0.57735,0.57735,0.57735;2.0944rad)
  sketch-geometry (18):
    g0: LineSegment StartX=-62 StartY=180 StartZ=0 EndX=-62 EndY=-40 EndZ=0
    g1-g9: Circle [constr] x9 (B-spline internal-alignment scaffolding for g10; pole/knot coordinates omitted)
    g10: BSplineCurve PolesCount=9 KnotsCount=7 Degree=3 IsPeriodic=0
    g11-g17: GeomPoint [constr] x7 (B-spline internal-alignment scaffolding for g10; pole/knot coordinates omitted)
  constraints (13):
    c: Vertical(g0)
    c: DistanceX(g0,g-1) = 62
    c: DistanceY(g0,g-1) = 40
    c: DistanceY(g0,g0) = 220
    c: Weight(g1) = 1
    c: Coincident(g10,g0)
    c: Equal(g1, g2-g9) x8
    c: Coincident(g10,g0)
    c: InternalAlignment(g1-g9 -> g10) x9
    c: InternalAlignment(g11-g17 -> g10) x7
    c: Horizontal(g0,g8)
    c: Horizontal(g0,g2)
    c: Block(g10)
FEATURE [PartDesign::Pad] Pad006  label="L foot main body002"
  Direction = (1,0,0)
  Length = 100
  Length2 = 10
  Midplane = true
  Placement = pos=(0,0,0) rot=(1,1,1;2.0944rad)
  Profile = -> Sketch201
  ReferenceAxis = -> Sketch201 [N_Axis]
  Suppressed = false
  Type = 0
FEATURE [PartDesign::Fillet] Fillet100
  Base = -> Pad006 [Edge4,Edge6,Edge1,Edge5,Edge2]
  BaseFeature = -> Pad006
  Placement = pos=(0,0,0) rot=(1,1,1;2.0944rad)
  Radius = 6
  SupportTransform = false
  Suppressed = false
  UseAllEdges = false
FEATURE [PartDesign::CoordinateSystem] Local_CS106  label="Left Foot/Ankle002"
  AttacherType = Attacher::AttachEngine3D
  AttachmentSupport = -> [Pad006]
  MapMode = 2
  Placement = pos=(0,0,0) rot=(0.57735,0.57735,0.57735;2.0944rad)
FEATURE [Sketcher::SketchObject] Sketch202
  ArcFitTolerance = 0
  AttachmentSupport = -> [XY_Plane064]
  FullyConstrained = true
  MakeInternals = false
  MapMode = 5
  sketch-geometry (2):
    g0: LineSegment StartX=7.7e-15 StartY=25 StartZ=0 EndX=7.7e-15 EndY=-25 EndZ=0
    g1: ArcOfCircle CenterX=0 CenterY=0 CenterZ=0 NormalX=0 NormalY=0 NormalZ=1 AngleXU=0 Radius=25 StartAngle=4.71239 EndAngle=7.85398
  constraints (6):
    c: Vertical(g0)
    c: PointOnObject(g1,g0)
    c: Coincident(g1,g0)
    c: Coincident(g1,g0)
    c: Coincident(g1,g-1)
    c: Radius(g1) = 25
FEATURE [PartDesign::Groove] Groove098  label="Ankle cut005"
  Angle = 360
  Angle2 = 60
  Axis = (0,1,0)
  Base = (0,0,0)
  BaseFeature = -> Fillet100
  Placement = pos=(0,0,0) rot=(1,1,1;2.0944rad)
  Profile = -> Sketch202
  ReferenceAxis = -> Sketch202 [V_Axis]
  Suppressed = false
  Type = 0
FEATURE [PartDesign::Fillet] Fillet101
  Base = -> Groove098 [Edge20,Edge19]
  BaseFeature = -> Groove098
  Placement = pos=(0,0,0) rot=(1,1,1;2.0944rad)
  Radius = 3
  SupportTransform = false
  Suppressed = false
  UseAllEdges = false
FEATURE [PartDesign::Body] Body060  label="Left foot002"
  AllowCompound = false
  Group = -> [Sketch201,Pad006,Fillet100,Sketch202,Groove098,Fillet101,Local_CS106]
  Origin = -> Origin064
  Placement = pos=(75,63.9536,-66.1731) rot=(0,0,1;0rad)
  Tip = -> Fillet101
FEATURE [Sketcher::SketchObject] Sketch203
  ArcFitTolerance = 0
  AttachmentSupport = -> [XY_Plane065]
  FullyConstrained = true
  MakeInternals = false
  MapMode = 5
  sketch-geometry (14):
    g0: LineSegment StartX=0 StartY=-29.246 StartZ=0 EndX=0 EndY=-395.97 EndZ=0
    g1-g7: Circle [constr] x7 (B-spline internal-alignment scaffolding for g8; pole/knot coordinates omitted)
    g8: BSplineCurve PolesCount=7 KnotsCount=5 Degree=3 IsPeriodic=0
    g9-g13: GeomPoint [constr] x5 (B-spline internal-alignment scaffolding for g8; pole/knot coordinates omitted)
  constraints (11):
    c: PointOnObject(g0,g-2)
    c: Vertical(g0)
    c: Weight(g1) = 1
    c: Coincident(g8,g0)
    c: Equal(g1, g2-g7) x6
    c: Coincident(g8,g0)
    c: InternalAlignment(g1-g7 -> g8) x7
    c: InternalAlignment(g9-g13 -> g8) x5
    c: Horizontal(g0,g6)
    c: Horizontal(g0,g2)
    c: Block(g8)
FEATURE [PartDesign::Revolution] Revolution104  label="R Thigh main body002"
  Angle = 360
  Angle2 = 60
  Axis = (0,1,0)
  Base = (0,0,0)
  Profile = -> Sketch203
  ReferenceAxis = -> Sketch203 [V_Axis]
  Reversed = true
  Suppressed = false
  Type = 0
FEATURE [PartDesign::CoordinateSystem] Local_CS107  label="Right Thigh/Big joint LCS002"
  AttacherType = Attacher::AttachEngine3D
  AttachmentSupport = -> [Revolution104]
  MapMode = 2
FEATURE [PartDesign::CoordinateSystem] Local_CS108  label="Right Thigh/Knee LCS002"
  AttacherType = Attacher::AttachEngine3D
  AttachmentOffset = pos=(0,-403,0) rot=(0,0,1;0rad)
  AttachmentSupport = -> [Revolution104]
  MapMode = 2
  Placement = pos=(0,-403,0) rot=(0,0,1;0rad)
FEATURE [Sketcher::SketchObject] Sketch204
  ArcFitTolerance = 0
  AttachmentSupport = -> [XY_Plane065]
  FullyConstrained = true
  MakeInternals = false
  MapMode = 5
  sketch-geometry (2):
    g0: LineSegment StartX=-1.1e-14 StartY=60 StartZ=0 EndX=-1.1e-14 EndY=-60 EndZ=0
    g1: ArcOfCircle CenterX=0 CenterY=0 CenterZ=0 NormalX=0 NormalY=0 NormalZ=1 AngleXU=0 Radius=60 StartAngle=4.71239 EndAngle=7.85398
  constraints (6):
    c: Vertical(g0)
    c: PointOnObject(g1,g0)
    c: Coincident(g1,g0)
    c: Coincident(g1,g0)
    c: Coincident(g1,g-1)
    c: Radius(g1) = 60
FEATURE [PartDesign::Groove] Groove099  label="R Big joint002"
  Angle = 360
  Angle2 = 60
  Axis = (0,1,0)
  Base = (0,0,0)
  BaseFeature = -> Revolution104
  Profile = -> Sketch204
  ReferenceAxis = -> Sketch204 [V_Axis]
  Suppressed = false
  Type = 0
FEATURE [PartDesign::Fillet] Fillet102
  Base = -> Groove099 [Edge1]
  BaseFeature = -> Groove099
  Radius = 6
  SupportTransform = false
  Suppressed = false
  UseAllEdges = false
FEATURE [Sketcher::SketchObject] Sketch205
  ArcFitTolerance = 0
  AttachmentSupport = -> [XY_Plane065]
  FullyConstrained = true
  MakeInternals = false
  MapMode = 5
  sketch-geometry (2):
    g0: LineSegment StartX=-6.4e-15 StartY=-368 StartZ=0 EndX=-6.4e-15 EndY=-438 EndZ=0
    g1: ArcOfCircle CenterX=0 CenterY=-403 CenterZ=0 NormalX=0 NormalY=0 NormalZ=1 AngleXU=0 Radius=35 StartAngle=4.71239 EndAngle=7.85398
  constraints (7):
    c: Vertical(g0)
    c: PointOnObject(g1,g0)
    c: Coincident(g1,g0)
    c: Coincident(g1,g0)
    c: PointOnObject(g1,g-2)
    c: DistanceY(g1,g-1) = 403
    c: Radius(g1) = 35
FEATURE [PartDesign::Groove] Groove100  label="R Knee cut002"
  Angle = 360
  Angle2 = 60
  Axis = (0,1,0)
  Base = (0,0,0)
  BaseFeature = -> Fillet102
  Profile = -> Sketch205
  ReferenceAxis = -> Sketch205 [V_Axis]
  Suppressed = false
  Type = 0
FEATURE [PartDesign::Fillet] Fillet103
  Base = -> Groove100 [Edge1]
  BaseFeature = -> Groove100
  Radius = 3
  SupportTransform = false
  Suppressed = false
  UseAllEdges = false
FEATURE [PartDesign::Revolution] Revolution105  label="R Knee002"
  Angle = 360
  Angle2 = 60
  Axis = (0,1,0)
  Base = (0,0,0)
  BaseFeature = -> Fillet103
  Profile = -> Sketch205
  ReferenceAxis = -> Sketch205 [V_Axis]
  Reversed = true
  Suppressed = false
  Type = 0
FEATURE [PartDesign::Body] Body061  label="Right Thigh002"
  AllowCompound = false
  Group = -> [Sketch203,Revolution104,Sketch204,Groove099,Fillet102,Sketch205,Groove100,Fillet103,Revolution105,Local_CS107,Local_CS108]
  Origin = -> Origin065
  Placement = pos=(-75,899.018,0.388141) rot=(-1,0,0;0.069813rad)
  Tip = -> Revolution105
FEATURE [Sketcher::SketchObject] Sketch206
  ArcFitTolerance = 0
  AttachmentSupport = -> [XY_Plane066]
  FullyConstrained = true
  MakeInternals = false
  MapMode = 5
  sketch-geometry (14):
    g0: LineSegment StartX=0 StartY=0 StartZ=0 EndX=0 EndY=-428.766 EndZ=0
    g1-g7: Circle [constr] x7 (B-spline internal-alignment scaffolding for g8; pole/knot coordinates omitted)
    g8: BSplineCurve PolesCount=7 KnotsCount=5 Degree=3 IsPeriodic=0
    g9-g13: GeomPoint [constr] x5 (B-spline internal-alignment scaffolding for g8; pole/knot coordinates omitted)
  constraints (9):
    c: Vertical(g0)
    c: PointOnObject(g0,g-2)
    c: Weight(g1) = 1
    c: Coincident(g8,g0)
    c: Equal(g1, g2-g7) x6
    c: Coincident(g8,g0)
    c: InternalAlignment(g1-g7 -> g8) x7
    c: InternalAlignment(g9-g13 -> g8) x5
    c: Block(g8)
FEATURE [PartDesign::Revolution] Revolution106  label="R Shin main body002"
  Angle = 360
  Angle2 = 60
  Axis = (0,1,0)
  Base = (0,0,0)
  Profile = -> Sketch206
  ReferenceAxis = -> Sketch206 [V_Axis]
  Reversed = true
  Suppressed = false
  Type = 0
FEATURE [PartDesign::CoordinateSystem] Local_CS109  label="Right Shin/Knee002"
  AttacherType = Attacher::AttachEngine3D
  AttachmentSupport = -> [Revolution106]
  MapMode = 2
FEATURE [PartDesign::CoordinateSystem] Local_CS110  label="Right Shin/Ankle002"
  AttacherType = Attacher::AttachEngine3D
  AttachmentOffset = pos=(0,-435,0) rot=(0,0,1;0rad)
  AttachmentSupport = -> [Revolution106]
  MapMode = 2
  Placement = pos=(0,-435,0) rot=(0,0,1;0rad)
FEATURE [Sketcher::SketchObject] Sketch207
  ArcFitTolerance = 0
  AttachmentSupport = -> [XY_Plane066]
  FullyConstrained = true
  MakeInternals = false
  MapMode = 5
  sketch-geometry (2):
    g0: LineSegment StartX=-6.4e-15 StartY=35 StartZ=0 EndX=-6.4e-15 EndY=-35 EndZ=0
    g1: ArcOfCircle CenterX=0 CenterY=0 CenterZ=0 NormalX=0 NormalY=0 NormalZ=1 AngleXU=0 Radius=35 StartAngle=4.71239 EndAngle=7.85398
  constraints (6):
    c: PointOnObject(g1,g0)
    c: Coincident(g1,g0)
    c: Coincident(g1,g0)
    c: Vertical(g0)
    c: Coincident(g1,g-1)
    c: Radius(g1) = 35
FEATURE [PartDesign::Groove] Groove101  label="R knee cut002"
  Angle = 360
  Angle2 = 60
  Axis = (0,1,0)
  Base = (0,0,0)
  BaseFeature = -> Revolution106
  Profile = -> Sketch207
  ReferenceAxis = -> Sketch207 [V_Axis]
  Suppressed = false
  Type = 0
FEATURE [PartDesign::Fillet] Fillet104
  Base = -> Groove101 [Edge1]
  BaseFeature = -> Groove101
  Radius = 3
  SupportTransform = false
  Suppressed = false
  UseAllEdges = false
FEATURE [Sketcher::SketchObject] Sketch208
  ArcFitTolerance = 0
  AttachmentSupport = -> [XY_Plane066]
  FullyConstrained = true
  MakeInternals = false
  MapMode = 5
  sketch-geometry (2):
    g0: LineSegment StartX=0 StartY=-410 StartZ=0 EndX=0 EndY=-460 EndZ=0
    g1: ArcOfCircle CenterX=0 CenterY=-435 CenterZ=0 NormalX=0 NormalY=0 NormalZ=1 AngleXU=0 Radius=25 StartAngle=4.71239 EndAngle=7.85398
  constraints (7):
    c: Vertical(g0)
    c: PointOnObject(g1,g0)
    c: Coincident(g1,g0)
    c: Coincident(g1,g0)
    c: PointOnObject(g1,g-2)
    c: DistanceY(g1,g-1) = 435
    c: Radius(g1) = 25
FEATURE [PartDesign::Groove] Groove102  label="R Ankle cut002"
  Angle = 360
  Angle2 = 60
  Axis = (0,1,0)
  Base = (0,0,0)
  BaseFeature = -> Fillet104
  Profile = -> Sketch208
  ReferenceAxis = -> Sketch208 [V_Axis]
  Suppressed = false
  Type = 0
FEATURE [PartDesign::Fillet] Fillet105
  Base = -> Groove102 [Edge3]
  BaseFeature = -> Groove102
  Radius = 3
  SupportTransform = false
  Suppressed = false
  UseAllEdges = false
FEATURE [PartDesign::Revolution] Revolution107  label="R Ankle002"
  Angle = 360
  Angle2 = 60
  Axis = (0,1,0)
  Base = (0,0,0)
  BaseFeature = -> Fillet105
  Profile = -> Sketch208
  ReferenceAxis = -> Sketch208 [V_Axis]
  Reversed = true
  Suppressed = false
  Type = 0
FEATURE [PartDesign::Body] Body062  label="Right Shin002"
  AllowCompound = false
  Group = -> [Sketch206,Revolution106,Sketch207,Groove101,Fillet104,Sketch208,Groove102,Fillet105,Revolution107,Local_CS109,Local_CS110]
  Origin = -> Origin066
  Placement = pos=(-75,497,28.5) rot=(0,0,1;0rad)
  Tip = -> Revolution107
FEATURE [Sketcher::SketchObject] Sketch209
  ArcFitTolerance = 0
  AttachmentSupport = -> [YZ_Plane067]
  FullyConstrained = true
  MakeInternals = false
  MapMode = 5
  Placement = pos=(0,0,0) rot=(0.57735,0.57735,0.57735;2.0944rad)
  sketch-geometry (18):
    g0: LineSegment StartX=-62 StartY=180 StartZ=0 EndX=-62 EndY=-40 EndZ=0
    g1-g9: Circle [constr] x9 (B-spline internal-alignment scaffolding for g10; pole/knot coordinates omitted)
    g10: BSplineCurve PolesCount=9 KnotsCount=7 Degree=3 IsPeriodic=0
    g11-g17: GeomPoint [constr] x7 (B-spline internal-alignment scaffolding for g10; pole/knot coordinates omitted)
  constraints (13):
    c: Vertical(g0)
    c: DistanceX(g0,g-1) = 62
    c: DistanceY(g0,g-1) = 40
    c: DistanceY(g0,g0) = 220
    c: Weight(g1) = 1
    c: Coincident(g10,g0)
    c: Equal(g1, g2-g9) x8
    c: Coincident(g10,g0)
    c: InternalAlignment(g1-g9 -> g10) x9
    c: InternalAlignment(g11-g17 -> g10) x7
    c: Horizontal(g0,g8)
    c: Horizontal(g0,g2)
    c: Block(g10)
FEATURE [PartDesign::Pad] Pad007  label="R foot main body002"
  Direction = (1,0,0)
  Length = 100
  Length2 = 10
  Midplane = true
  Placement = pos=(0,0,0) rot=(1,1,1;2.0944rad)
  Profile = -> Sketch209
  ReferenceAxis = -> Sketch209 [N_Axis]
  Suppressed = false
  Type = 0
FEATURE [PartDesign::Fillet] Fillet106
  Base = -> Pad007 [Edge4,Edge6,Edge1,Edge5,Edge2]
  BaseFeature = -> Pad007
  Placement = pos=(0,0,0) rot=(1,1,1;2.0944rad)
  Radius = 6
  SupportTransform = false
  Suppressed = false
  UseAllEdges = false
FEATURE [PartDesign::CoordinateSystem] Local_CS111  label="Right Foot/Ankle002"
  AttacherType = Attacher::AttachEngine3D
  AttachmentSupport = -> [Pad007]
  MapMode = 2
  Placement = pos=(0,0,0) rot=(0.57735,0.57735,0.57735;2.0944rad)
FEATURE [Sketcher::SketchObject] Sketch210
  ArcFitTolerance = 0
  AttachmentSupport = -> [XY_Plane067]
  FullyConstrained = true
  MakeInternals = false
  MapMode = 5
  sketch-geometry (2):
    g0: LineSegment StartX=7.7e-15 StartY=25 StartZ=0 EndX=7.7e-15 EndY=-25 EndZ=0
    g1: ArcOfCircle CenterX=0 CenterY=0 CenterZ=0 NormalX=0 NormalY=0 NormalZ=1 AngleXU=0 Radius=25 StartAngle=4.71239 EndAngle=7.85398
  constraints (6):
    c: Vertical(g0)
    c: PointOnObject(g1,g0)
    c: Coincident(g1,g0)
    c: Coincident(g1,g0)
    c: Coincident(g1,g-1)
    c: Radius(g1) = 25
FEATURE [PartDesign::Groove] Groove103  label="Ankle cut006"
  Angle = 360
  Angle2 = 60
  Axis = (0,1,0)
  Base = (0,0,0)
  BaseFeature = -> Fillet106
  Placement = pos=(0,0,0) rot=(1,1,1;2.0944rad)
  Profile = -> Sketch210
  ReferenceAxis = -> Sketch210 [V_Axis]
  Suppressed = false
  Type = 0
FEATURE [PartDesign::Fillet] Fillet107
  Base = -> Groove103 [Edge20,Edge19]
  BaseFeature = -> Groove103
  Placement = pos=(0,0,0) rot=(1,1,1;2.0944rad)
  Radius = 3
  SupportTransform = false
  Suppressed = false
  UseAllEdges = false
FEATURE [PartDesign::Body] Body063  label="Right foot002"
  AllowCompound = false
  Group = -> [Sketch209,Pad007,Fillet106,Sketch210,Groove103,Fillet107,Local_CS111]
  Origin = -> Origin067
  Placement = pos=(-75,62,28.5) rot=(0,0,1;0rad)
  Tip = -> Fillet107
FEATURE [App::Part] Part_004  label="Mannequin_mp-dummy-1850mm-standing-001"
  Group = -> [LCS_002,Body049,Body050,Body051,Body052,Body053,Body054,Body055,Body056,Body057,Body058,Body059,Body060,Body061,Body062,Body063]
  Origin = -> Origin052
  Placement = pos=(-7999.3,15863.2,-3.5223e-12) rot=(-0.983106,0.129428,0.129428;4.69535rad)
FEATURE [App::Link] Assembly001
  LinkedObject = -> <external shed_shelves.FCStd>#Assembly
FEATURE [App::FeaturePython] GroundedJoint  # Assembly grounded joint (typed FeaturePython)
  ObjectToGround = -> Assembly001
FEATURE [Assembly::JointGroup] Joints
  Group = -> [GroundedJoint]
FEATURE [Assembly::AssemblyObject] Assembly
  Group = -> [Joints,Assembly001,GroundedJoint]
  Origin = -> Origin
  Placement = pos=(-8457.6,16726.7,1900) rot=(0,0,1;0rad)
  Type = Assembly
note: 1 file-system path scrubbed to <path> (originals preserved in the JSON sidecar)

RESOLVED EXTERNAL PARTS (link-assembly join: the EXTERNAL_REF files above that resolve inside this repo's crawl, each included once):
---- part shed_shelves.FCStd = doc fcstd_24dc352d4699 ----
FCSTD DOCUMENT  (FreeCAD 1.0R39109 (Git))
Label: shed_shelves
License: All rights reserved
LicenseURL: https://en.wikipedia.org/wiki/All_rights_reserved
objects: App::FeaturePython×9, App::Link×7, App::Part×5, Sketcher::SketchObject×4, PartDesign::Pad×4, PartDesign::Body×4, Part::Box×2, PartDesign::Chamfer×2, App::DocumentObjectGroup×1, Assembly::JointGroup×1, Assembly::AssemblyObject×1
note: 32 computed .brp shape members not serialized (recipe doc carries the construction recipe); baked Part::Feature solids carry a one-line shape summary decoded from their .brp

FEATURE [Sketcher::SketchObject] Sketch
  ArcFitTolerance = 1e-06
  AttachmentSupport = -> [XY_Plane]
  FullyConstrained = true
  MakeInternals = false
  MapMode = 5
  sketch-geometry (4):
    g0: LineSegment StartX=0 StartY=0 StartZ=0 EndX=400 EndY=0 EndZ=0
    g1: LineSegment StartX=400 StartY=0 StartZ=0 EndX=400 EndY=2000 EndZ=0
    g2: LineSegment StartX=400 StartY=2000 StartZ=0 EndX=0 EndY=2000 EndZ=0
    g3: LineSegment StartX=0 StartY=2000 StartZ=0 EndX=0 EndY=0 EndZ=0
  constraints (11):
    c: Coincident(g0,g1)
    c: Coincident(g1,g2)
    c: Coincident(g2,g3)
    c: Coincident(g3,g0)
    c: Horizontal(g0)
    c: Horizontal(g2)
    c: Vertical(g1)
    c: Vertical(g3)
    c: Distance(g1,g3) = 400
    c: Distance(g0,g2) = 2000
    c: Coincident(g0,g-1)
FEATURE [PartDesign::Pad] Pad
  Direction = (0,0,1)
  Length = 18
  Length2 = 10
  Profile = -> Sketch
  ReferenceAxis = -> Sketch [N_Axis]
  Refine = true
  Suppressed = false
  Type = 0
FEATURE [Sketcher::SketchObject] Sketch001
  ArcFitTolerance = 1e-06
  AttachmentSupport = -> [XY_Plane002]
  FullyConstrained = true
  MakeInternals = false
  MapMode = 5
  sketch-geometry (4):
    g0: LineSegment StartX=0 StartY=0 StartZ=0 EndX=300 EndY=0 EndZ=0
    g1: LineSegment StartX=300 StartY=0 StartZ=0 EndX=300 EndY=800 EndZ=0
    g2: LineSegment StartX=300 StartY=800 StartZ=0 EndX=0 EndY=800 EndZ=0
    g3: LineSegment StartX=0 StartY=800 StartZ=0 EndX=0 EndY=0 EndZ=0
  constraints (11):
    c: Coincident(g0,g1)
    c: Coincident(g1,g2)
    c: Coincident(g2,g3)
    c: Coincident(g3,g0)
    c: Horizontal(g0)
    c: Horizontal(g2)
    c: Vertical(g1)
    c: Vertical(g3)
    c: Distance(g1,g3) = 300
    c: Distance(g0,g2) = 800
    c: Coincident(g0,g-1)
FEATURE [PartDesign::Pad] Pad001
  Direction = (0,0,1)
  Length = 18
  Length2 = 10
  Profile = -> Sketch001
  ReferenceAxis = -> Sketch001 [N_Axis]
  Refine = true
  Suppressed = false
  Type = 0
FEATURE [PartDesign::Body] Body001
  AllowCompound = false
  Group = -> [Sketch001,Pad001]
  Origin = -> Origin002
  Tip = -> Pad001
FEATURE [App::Part] Part001  label="Part_800x400x18"
  Group = -> [Body001]
  Origin = -> Origin003
FEATURE [Sketcher::SketchObject] Sketch002
  ArcFitTolerance = 1e-06
  AttachmentSupport = -> [XY_Plane004]
  FullyConstrained = true
  MakeInternals = false
  MapMode = 5
  sketch-geometry (4):
    g0: LineSegment StartX=0 StartY=0 StartZ=0 EndX=300 EndY=0 EndZ=0
    g1: LineSegment StartX=300 StartY=0 StartZ=0 EndX=300 EndY=800 EndZ=0
    g2: LineSegment StartX=300 StartY=800 StartZ=0 EndX=0 EndY=800 EndZ=0
    g3: LineSegment StartX=0 StartY=800 StartZ=0 EndX=0 EndY=0 EndZ=0
  constraints (11):
    c: Coincident(g0,g1)
    c: Coincident(g1,g2)
    c: Coincident(g2,g3)
    c: Coincident(g3,g0)
    c: Horizontal(g0)
    c: Horizontal(g2)
    c: Vertical(g1)
    c: Vertical(g3)
    c: Distance(g1,g3) = 300
    c: Distance(g0,g2) = 800
    c: Coincident(g0,g-1)
FEATURE [PartDesign::Pad] Pad002
  Direction = (0,0,1)
  Length = 18
  Length2 = 10
  Profile = -> Sketch002
  ReferenceAxis = -> Sketch002 [N_Axis]
  Refine = true
  Suppressed = false
  Type = 0
FEATURE [App::Link] Part_800x30x18  label="Part_800x30x019"
  LinkPlacement = pos=(0,0,0) rot=(0,0,1;4.71239rad)
  LinkedObject = -> Part002
  Placement = pos=(0,0,0) rot=(0,0,1;4.71239rad)
FEATURE [App::FeaturePython] GroundedJoint  # Assembly grounded joint (typed FeaturePython)
  ObjectToGround = -> Part_800x30x18
  Placement = pos=(0,0,0) rot=(0,0,1;4.71239rad)
FEATURE [App::Link] Part_800x400x18  label="Part_800x400x019"
  LinkPlacement = pos=(-300,-800,0) rot=(0,0,1;0rad)
  LinkedObject = -> Part001
  Placement = pos=(-300,-800,0) rot=(0,0,1;0rad)
FEATURE [App::Link] Part_2000x400x18  label="Part_2000x400x019"
  LinkPlacement = pos=(-300,-2800,0) rot=(0,0,1;0rad)
  LinkedObject = -> Part
  Placement = pos=(-300,-2800,0) rot=(0,0,1;0rad)
FEATURE [Part::Box] Box  label="Cube"
  AttacherType = Attacher::AttachEngine3D
  Height = 300
  Length = 300
  Placement = pos=(384.2,340,0) rot=(0,0,1;0rad)
  Width = 300
FEATURE [Part::Box] Box001  label="Cube001"
  AttacherType = Attacher::AttachEngine3D
  Height = 400
  Length = 400
  Placement = pos=(35,-666.1,0) rot=(0,0,1;0rad)
  Width = 400
FEATURE [App::Part] Part003
  Group = -> [Box,Box001]
  Origin = -> Origin007
  Placement = pos=(-336.4,-642.4,18) rot=(0,0,1;0rad)
FEATURE [PartDesign::Chamfer] Chamfer
  Angle = 45
  Base = -> Pad [Edge5]
  BaseFeature = -> Pad
  ChamferType = 0
  FlipDirection = false
  Refine = true
  Size = 100
  Size2 = 1
  SupportTransform = false
  Suppressed = false
  UseAllEdges = false
FEATURE [PartDesign::Body] Body
  AllowCompound = false
  Group = -> [Sketch,Pad,Chamfer]
  Origin = -> Origin
  Tip = -> Chamfer
FEATURE [App::Part] Part  label="Part_2000x400x18"
  Group = -> [Body]
  Origin = -> Origin001
FEATURE [PartDesign::Chamfer] Chamfer001
  Angle = 45
  Base = -> Pad002 [Edge5]
  BaseFeature = -> Pad002
  ChamferType = 0
  FlipDirection = false
  Refine = true
  Size = 100
  Size2 = 1
  SupportTransform = false
  Suppressed = false
  UseAllEdges = false
FEATURE [PartDesign::Body] Body002
  AllowCompound = false
  Group = -> [Sketch002,Pad002,Chamfer001]
  Origin = -> Origin004
  Tip = -> Chamfer001
FEATURE [App::Part] Part002  label="Part_800x30x18"
  Group = -> [Body002]
  Origin = -> Origin005
FEATURE [App::DocumentObjectGroup] Group  label="ShelvePlates"
  Group = -> [Part002,Part001,Part]
FEATURE [Sketcher::SketchObject] Sketch003
  ArcFitTolerance = 1e-06
  AttachmentSupport = -> [XZ_Plane009]
  FullyConstrained = true
  MakeInternals = false
  MapMode = 5
  Placement = pos=(0,0,0) rot=(1,0,0;1.5708rad)
  expr: Constraints[52] = .Constraints.edgeradii
  expr: Constraints[53] = .Constraints.edgeradii
  expr: Constraints[54] = .Constraints.wood_thinckness
  expr: Constraints[66] = .Constraints.wood_thinckness
  sketch-geometry (32):
    g0: LineSegment StartX=-43 StartY=80 StartZ=0 EndX=-43 EndY=-343 EndZ=0
    g1: LineSegment StartX=-43 StartY=-343 StartZ=0 EndX=-30 EndY=-343 EndZ=0
    g2: LineSegment StartX=0 StartY=-313 StartZ=0 EndX=0 EndY=50 EndZ=0
    g3: LineSegment StartX=-30 StartY=80 StartZ=0 EndX=-43 EndY=80 EndZ=0
    g4: LineSegment StartX=0 StartY=0 StartZ=0 EndX=0 EndY=-43 EndZ=0
    g5: LineSegment StartX=0 StartY=-43 StartZ=0 EndX=270 EndY=-43 EndZ=0
    g6: LineSegment StartX=300 StartY=-13 StartZ=0 EndX=300 EndY=0 EndZ=0
    g7: LineSegment StartX=300 StartY=0 StartZ=0 EndX=0 EndY=0 EndZ=0
    g8: LineSegment [constr] StartX=0 StartY=0 StartZ=0 EndX=400 EndY=0 EndZ=0
    g9: LineSegment [constr] StartX=400 StartY=0 StartZ=0 EndX=400 EndY=18 EndZ=0
    g10: LineSegment [constr] StartX=400 StartY=18 StartZ=0 EndX=0 EndY=18 EndZ=0
    g11: LineSegment [constr] StartX=0 StartY=18 StartZ=0 EndX=0 EndY=0 EndZ=0
    g12: LineSegment [constr] StartX=-43 StartY=-343 StartZ=0 EndX=300 EndY=0 EndZ=0
    g13: ArcOfCircle [constr] CenterX=-30 CenterY=50 CenterZ=0 NormalX=0 NormalY=0 NormalZ=1 AngleXU=0 Radius=30 StartAngle=0 EndAngle=1.5708
    g14: GeomPoint [constr] X=0 Y=80 Z=0
    g15: LineSegment StartX=0 StartY=50 StartZ=0 EndX=-30 EndY=80 EndZ=0
    g16: ArcOfCircle [constr] CenterX=270 CenterY=-13 CenterZ=0 NormalX=0 NormalY=0 NormalZ=1 AngleXU=0 Radius=30 StartAngle=4.71239 EndAngle=6.28319
    g17: GeomPoint [constr] X=300 Y=-43 Z=0
    g18: LineSegment StartX=270 StartY=-43 StartZ=0 EndX=300 EndY=-13 EndZ=0
    g19: ArcOfCircle [constr] CenterX=-30 CenterY=-313 CenterZ=0 NormalX=0 NormalY=0 NormalZ=1 AngleXU=0 Radius=30 StartAngle=4.71239 EndAngle=6.28319
    g20: GeomPoint [constr] X=0 Y=-343 Z=0
    g21: LineSegment StartX=-30 StartY=-343 StartZ=0 EndX=0 EndY=-313 EndZ=0
    g22: LineSegment StartX=3.6e-15 StartY=-293 StartZ=0 EndX=250 EndY=-43 EndZ=0
    g23: LineSegment [constr] StartX=-30.4056 StartY=-262.594 StartZ=0 EndX=219.594 EndY=-12.5944 EndZ=0
    g24: LineSegment [constr] StartX=-30.4056 StartY=-262.594 StartZ=0 EndX=3.6e-15 EndY=-293 EndZ=0
    g25: LineSegment [constr] StartX=219.594 StartY=-12.5944 StartZ=0 EndX=250 EndY=-43 EndZ=0
    g26: LineSegment StartX=3.6e-15 StartY=-293 StartZ=0 EndX=3.6e-15 EndY=-232.189 EndZ=0
    g27: LineSegment StartX=3.6e-15 StartY=-232.189 StartZ=0 EndX=189.189 EndY=-43 EndZ=0
    g28: LineSegment StartX=189.189 StartY=-43 StartZ=0 EndX=250 EndY=-43 EndZ=0
    g29: LineSegment [constr] StartX=-30 StartY=-343 StartZ=0 EndX=-43 EndY=-356 EndZ=0
    g30: LineSegment [constr] StartX=-30 StartY=80 StartZ=0 EndX=-43 EndY=93 EndZ=0
    g31: LineSegment [constr] StartX=-43 StartY=93 StartZ=0 EndX=-43 EndY=-356 EndZ=0
  constraints (88):
    c: Coincident(g3,g0)
    c: Vertical(g0)
    c: Vertical(g2)
    c: Horizontal(g1)
    c: Horizontal(g3)
    c: Coincident(g4,g5)
    c: Coincident(g6,g7)
    c: Coincident(g7,g4)
    c: Vertical(g4)
    c: Vertical(g6)
    c: Horizontal(g5)
    c: Horizontal(g7)
    c: PointOnObject(g4,g2)
    c: Distance(g17,g6) = 43  'wood_thinckness'
    c: Distance(g14,g4) = 80
    c: Coincident(g8,g9)
    c: Coincident(g9,g10)
    c: Coincident(g10,g11)
    c: Coincident(g11,g8)
    c: Horizontal(g8)
    c: Horizontal(g10)
    c: Vertical(g9)
    c: Vertical(g11)
    c: Coincident(g8,g-1)
    c: DistanceX(g10,g10) = 400
    c: Distance(g9,g9) = 18
    c: Coincident(g1,g0)
    c: Coincident(g4,g8)
    c: Coincident(g12,g0)
    c: Coincident(g12,g6)
    c: Angle(g10,g12) = 0.785398
    c: DistanceY(g0,g0) = 423
    c: Distance(g8,g6) = 100
    c: PointOnObject(g14,g2)
    c: PointOnObject(g14,g3)
    c: Tangent(g2,g13) = -1.5708
    c: Tangent(g3,g13) = -1.5708
    c: Coincident(g15,g2)
    c: Coincident(g15,g3)
    c: PointOnObject(g17,g5)
    c: PointOnObject(g17,g6)
    c: Tangent(g5,g16) = -1.5708
    c: Tangent(g6,g16) = -1.5708
    c: Coincident(g18,g5)
    c: Coincident(g18,g6)
    c: PointOnObject(g20,g1)
    c: PointOnObject(g20,g2)
    c: Tangent(g1,g19) = -1.5708
    c: Tangent(g2,g19) = -1.5708
    c: Coincident(g21,g1)
    c: Coincident(g21,g2)
    c: Radius(g16) = 30  'edgeradii'
    c: Radius(g19) = 30
    c: Radius(g13) = 30
    c: Distance(g0,g2) = 43
    c: DistanceX(g7,g7) = 300
    c: PointOnObject(g22,g2)
    c: PointOnObject(g22,g5)
    c: Parallel(g23,g22)
    c: Coincident(g24,g23)
    c: Coincident(g24,g22)
    c: Coincident(g25,g22)
    c: Coincident(g23,g25)
    c: Parallel(g24,g25)
    c: Perpendicular(g25,g23,g23) = 1.5708
    c: Parallel(g22,g12)
    c: Distance(g25,g25) = 43
    c: Coincident(g22,g26)
    c: PointOnObject(g26,g23)
    c: Vertical(g26)
    c: Coincident(g26,g27)
    c: Coincident(g28,g22)
    c: Coincident(g28,g27)
    c: PointOnObject(g27,g23)
    c: PointOnObject(g27,g5)
    c: Distance(g22,g22) = 353.553
    c: Distance(g2,g4) = 50
    c: Distance(g2,g22) = 20
    c: Coincident(g29,g1)
    c: Coincident(g30,g3)
    c: Parallel(g15,g30)
    c: Parallel(g29,g21)
    c: Coincident(g31,g30)
    c: Coincident(g31,g29)
    c: Vertical(g31)
    c: Vertical(g29,g0)
    c: DistanceY(g29,g30) = 449
    c: DistanceY(g29,g22) = 63
FEATURE [PartDesign::Pad] Pad003
  Direction = (0,-1,2e-16)
  Length = 43
  Length2 = 10
  Placement = pos=(0,0,0) rot=(1,0,0;1.5708rad)
  Profile = -> Sketch003
  ReferenceAxis = -> Sketch003 [N_Axis]
  Refine = true
  Suppressed = false
  Type = 0
FEATURE [PartDesign::Body] Body003
  AllowCompound = false
  Group = -> [Sketch003,Pad003]
  Origin = -> Origin009
  Tip = -> Pad003
FEATURE [App::Part] Part004  label="shelf_boy"
  Group = -> [Body003]
  Origin = -> Origin008
FEATURE [App::Link] shelf_boy  label="shelf_boy001"
  LinkPlacement = pos=(-300,-2688.5,-4.8e-15) rot=(0,0,1;0rad)
  LinkedObject = -> Part004
  Placement = pos=(-300,-2688.5,-4.8e-15) rot=(0,0,1;0rad)
FEATURE [App::Link] shelf_boy001  label="shelf_boy002"
  LinkPlacement = pos=(-300,-778.5,-4.8e-15) rot=(0,0,1;0rad)
  LinkedObject = -> Part004
  Placement = pos=(-300,-778.5,-4.8e-15) rot=(0,0,1;0rad)
FEATURE [App::Link] shelf_boy002  label="shelf_boy003"
  LinkPlacement = pos=(21.5,-1.11e-14,-7) rot=(0,0,1;4.71239rad)
  LinkedObject = -> Part004
  Placement = pos=(21.5,-1.11e-14,-7) rot=(0,0,1;4.71239rad)
FEATURE [App::Link] shelf_boy003  label="shelf_boy004"
  LinkPlacement = pos=(621.5,-0.000104777,-4.8e-15) rot=(0,0,1;4.71239rad)
  LinkedObject = -> Part004
  Placement = pos=(621.5,-0.000104777,-4.8e-15) rot=(0,0,1;4.71239rad)
FEATURE [App::FeaturePython] Parallel002  # Assembly joint (typed FeaturePython)
  Activated = true
  AngleMax = 0
  AngleMin = 0
  Detach1 = false
  Detach2 = false
  Distance = 0
  Distance2 = 0
  EnableAngleMax = false
  EnableAngleMin = false
  EnableLengthMax = false
  EnableLengthMin = false
  JointType = 6 (Parallel)
  LengthMax = 0
  LengthMin = 0
  Placement1 = pos=(0,-43,9.5e-15) rot=(0,1,0;3.14159rad)
  Placement2 = pos=(0,800,0) rot=(0,0,1;0rad)
  Reference1 = -> Assembly [shelf_boy002.Body003.Face8,shelf_boy002.Body003.Vertex10]
  Reference2 = -> Assembly [Part_800x400x18.Body001.Face5,Part_800x400x18.Body001.Vertex7]
FEATURE [App::FeaturePython] GroundedJoint001  # Assembly grounded joint (typed FeaturePython)
  ObjectToGround = -> Part_800x400x18
  Placement = pos=(-300,-800,0) rot=(0,0,1;0rad)
FEATURE [App::FeaturePython] GroundedJoint002  # Assembly grounded joint (typed FeaturePython)
  ObjectToGround = -> Part_2000x400x18
  Placement = pos=(-300,-2800,0) rot=(0,0,1;0rad)
FEATURE [App::FeaturePython] Fixed  # Assembly joint (typed FeaturePython)
  Activated = true
  AngleMax = 0
  AngleMin = 0
  Detach1 = false
  Detach2 = false
  Distance = 0
  Distance2 = 0
  EnableAngleMax = false
  EnableAngleMin = false
  EnableLengthMax = false
  EnableLengthMin = false
  JointType = 0 (Fixed)
  LengthMax = 0
  LengthMin = 0
  Placement1 = pos=(0,-21.5,25) rot=(-0.57735,0.57735,-0.57735;2.0944rad)
  Placement2 = pos=(300,800,18) rot=(0,-0.707107,0.707107;3.14159rad)
  Reference1 = -> Assembly [shelf_boy002.Body003.Face4,shelf_boy002.Body003.Face4]
  Reference2 = -> Assembly [Part_800x400x18.Body001.Face3,Part_800x400x18.Body001.Vertex6]
FEATURE [App::FeaturePython] Fixed001  # Assembly joint (typed FeaturePython)
  Activated = true
  AngleMax = 0
  AngleMin = 0
  Detach1 = false
  Detach2 = false
  Distance = 0
  Distance2 = 0
  EnableAngleMax = false
  EnableAngleMin = false
  EnableLengthMax = false
  EnableLengthMin = false
  JointType = 0 (Fixed)
  LengthMax = 0
  LengthMin = 0
  Placement1 = pos=(0,2000,0) rot=(-0.57735,-0.57735,0.57735;4.18879rad)
  Placement2 = pos=(0,-21.5,4.8e-15) rot=(-0.57735,-0.57735,0.57735;4.18879rad)
  Reference1 = -> Assembly [Part_2000x400x18.Body.Edge8,Part_2000x400x18.Body.Vertex7]
  Reference2 = -> Assembly [shelf_boy001.Body003.Edge12,shelf_boy001.Body003.Edge12]
FEATURE [App::FeaturePython] Fixed002  # Assembly joint (typed FeaturePython)
  Activated = true
  AngleMax = 0
  AngleMin = 0
  Detach1 = false
  Detach2 = false
  Distance = 0
  Distance2 = 0
  EnableAngleMax = false
  EnableAngleMin = false
  EnableLengthMax = false
  EnableLengthMin = false
  JointType = 0 (Fixed)
  LengthMax = 0
  LengthMin = 0
  Offset2 = pos=(0,0,-90) rot=(0,0,1;0rad)
  Placement1 = pos=(0,-21.5,4.8e-15) rot=(-0.57735,-0.57735,0.57735;4.18879rad)
  Placement2 = pos=(0,90,0) rot=(-0.57735,-0.57735,0.57735;4.18879rad)
  Reference1 = -> Assembly [shelf_boy.Body003.Edge12,shelf_boy.Body003.Edge12]
  Reference2 = -> Assembly [Part_2000x400x18.Body.Edge8,Part_2000x400x18.Body.Vertex6]
FEATURE [App::FeaturePython] Parallel  # Assembly joint (typed FeaturePython)
  Activated = true
  AngleMax = 0
  AngleMin = 0
  Detach1 = false
  Detach2 = false
  Distance = 0
  Distance2 = 0
  EnableAngleMax = false
  EnableAngleMin = false
  EnableLengthMax = false
  EnableLengthMin = false
  JointType = 6 (Parallel)
  LengthMax = 0
  LengthMin = 0
  Placement1 = pos=(0,800,0) rot=(0,0,1;0rad)
  Placement2 = pos=(0,0,0) rot=(0,1,0;3.14159rad)
  Reference1 = -> Assembly [Part_800x30x18.Body002.Face2,Part_800x30x18.Body002.Vertex7]
  Reference2 = -> Assembly [shelf_boy003.Body003.Face8,shelf_boy003.Body003.Vertex9]
FEATURE [App::FeaturePython] Fixed003  # Assembly joint (typed FeaturePython)
  Activated = true
  AngleMax = 0
  AngleMin = 0
  Detach1 = false
  Detach2 = false
  Distance = 0
  Distance2 = 0
  EnableAngleMax = false
  EnableAngleMin = false
  EnableLengthMax = false
  EnableLengthMin = false
  JointType = 0 (Fixed)
  LengthMax = 0
  LengthMin = 0
  Offset2 = pos=(0,0,200) rot=(0,0,1;0rad)
  Placement1 = pos=(0,-21.5,4.8e-15) rot=(-0.57735,-0.57735,0.57735;4.18879rad)
  Placement2 = pos=(0,600,0) rot=(-0.57735,-0.57735,0.57735;4.18879rad)
  Reference1 = -> Assembly [shelf_boy003.Body003.Edge12,shelf_boy003.Body003.Edge12]
  Reference2 = -> Assembly [Part_800x30x18.Body002.Edge8,Part_800x30x18.Body002.Vertex7]
FEATURE [Assembly::JointGroup] Joints
  Group = -> [GroundedJoint,Parallel002,GroundedJoint001,GroundedJoint002,Fixed,Fixed001,Fixed002,Parallel,Fixed003]
FEATURE [Assembly::AssemblyObject] Assembly
  Group = -> [Joints,Part_800x30x18,GroundedJoint,Part_800x400x18,Part_2000x400x18,Part003,shelf_boy,shelf_boy001,shelf_boy002,shelf_boy003,Parallel002,GroundedJoint001,GroundedJoint002,Fixed,Fixed001,Fixed002,Parallel,Fixed003]
  Origin = -> Origin006
  Type = Assembly
